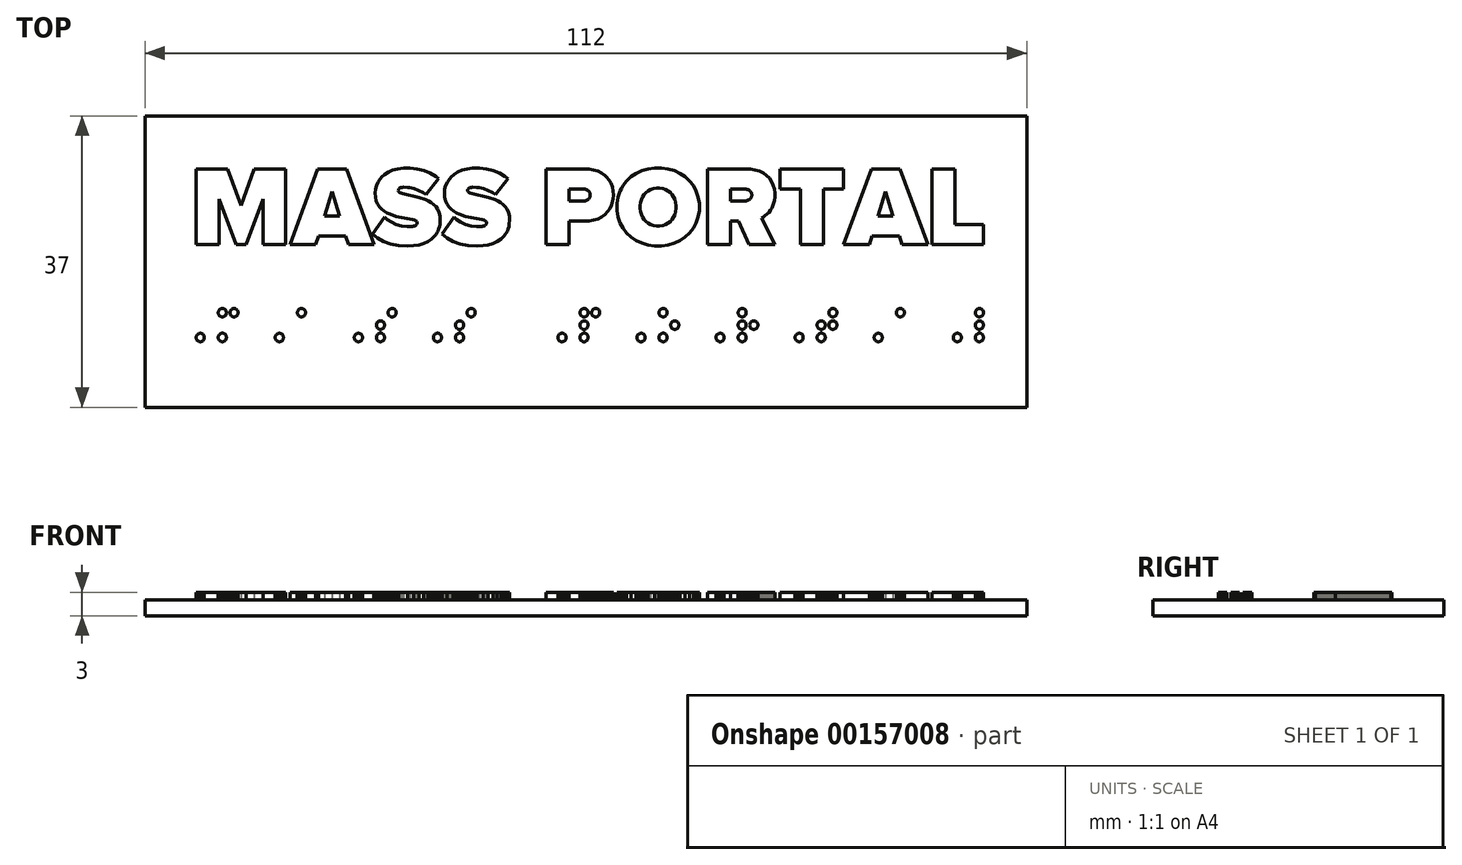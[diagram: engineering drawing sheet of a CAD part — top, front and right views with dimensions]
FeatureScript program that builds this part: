
annotation { "Feature Type Name" : "Feature", "Feature Type Description" : "" }
export const myFeature = defineFeature(function(context is Context, id is Id, definition is map)
    precondition{}
    {
        {
            var Q0;
            Q0=qCreatedBy(makeId("Top.planeOp"),FACE);
            var sketch = newSketch(context, id + "F0", { "sketchPlane" : qUnion([Q0])});
            skLineSegment(sketch, "E0", {"start": v(-10.6, -3.27) * mm, "end": v(-10.74, -3.5) * mm});
            skLineSegment(sketch, "E1", {"start": v(-31.01, -3.66) * mm, "end": v(-30.67, -4.78) * mm});
            skLineSegment(sketch, "E2", {"start": v(-34.46, -3.66) * mm, "end": v(-31.01, -3.66) * mm});
            skLineSegment(sketch, "E3", {"start": v(-45.99, 4.8) * mm, "end": v(-44.3, 0.2) * mm});
            skLineSegment(sketch, "E4", {"start": v(-50, -4.78) * mm, "end": v(-47.1, -4.78) * mm});
            skLineSegment(sketch, "E5", {"start": v(-14.08, 2.45) * mm, "end": v(-14.37, 2.49) * mm});
            skLineSegment(sketch, "E6", {"start": v(-45.99, 4.8) * mm, "end": v(-50, 4.8) * mm});
            skLineSegment(sketch, "E7", {"start": v(-10.74, -3.5) * mm, "end": v(-10.9, -3.7) * mm});
            skLineSegment(sketch, "E8", {"start": v(-17.97, 3.4) * mm, "end": v(-18.1, 3.18) * mm});
            skLineSegment(sketch, "E9", {"start": v(1.93, 4) * mm, "end": v(2.11, 3.84) * mm});
            skLineSegment(sketch, "E10", {"start": v(-47.1, 0.98) * mm, "end": v(-44.95, -4.78) * mm});
            skLineSegment(sketch, "E11", {"start": v(10.46, 1.57) * mm, "end": v(10.66, 1.28) * mm});
            skLineSegment(sketch, "E12", {"start": v(-11.08, -3.9) * mm, "end": v(-11.29, -4.08) * mm});
            skLineSegment(sketch, "E13", {"start": v(-24, 1.76) * mm, "end": v(-23.77, 1.69) * mm});
            skLineSegment(sketch, "E14", {"start": v(-20.87, 0.96) * mm, "end": v(-20.5, 0.79) * mm});
            skLineSegment(sketch, "E15", {"start": v(-20.15, 0.58) * mm, "end": v(-19.83, 0.34) * mm});
            skLineSegment(sketch, "E16", {"start": v(-47.1, 0.98) * mm, "end": v(-47.1, -4.78) * mm});
            skLineSegment(sketch, "E17", {"start": v(-33.69, -1.13) * mm, "end": v(-31.79, -1.13) * mm});
            skLineSegment(sketch, "E18", {"start": v(-20.5, 0.79) * mm, "end": v(-20.15, 0.58) * mm});
            skLineSegment(sketch, "E19", {"start": v(-44.3, 0.2) * mm, "end": v(-42.63, 4.8) * mm});
            skLineSegment(sketch, "E20", {"start": v(19.98, 2.23) * mm, "end": v(20.11, 2.2) * mm});
            skLineSegment(sketch, "E21", {"start": v(-14.37, -2.5) * mm, "end": v(-14.02, -2.5) * mm});
            skLineSegment(sketch, "E22", {"start": v(-26.95, 0.37) * mm, "end": v(-26.72, 0.02) * mm});
            skLineSegment(sketch, "E23", {"start": v(-30.91, 4.8) * mm, "end": v(-34.56, 4.8) * mm});
            skLineSegment(sketch, "E24", {"start": v(-19.83, 0.34) * mm, "end": v(-19.55, 0.05) * mm});
            skLineSegment(sketch, "E25", {"start": v(23.3, 2.79) * mm, "end": v(23.44, 2.3) * mm});
            skLineSegment(sketch, "E26", {"start": v(-32.74, 1.96) * mm, "end": v(-33.69, -1.13) * mm});
            skLineSegment(sketch, "E27", {"start": v(-50, -4.78) * mm, "end": v(-50, 4.8) * mm});
            skLineSegment(sketch, "E28", {"start": v(-32.74, 1.96) * mm, "end": v(-31.79, -1.13) * mm});
            skLineSegment(sketch, "E29", {"start": v(-17.36, -4.36) * mm, "end": v(-16.48, -4.68) * mm});
            skLineSegment(sketch, "E30", {"start": v(-30.91, 4.8) * mm, "end": v(-27.38, -4.78) * mm});
            skLineSegment(sketch, "E31", {"start": v(-38.1, -4.78) * mm, "end": v(-34.56, 4.8) * mm});
            skLineSegment(sketch, "E32", {"start": v(2.11, 3.84) * mm, "end": v(2.43, 3.45) * mm});
            skLineSegment(sketch, "E33", {"start": v(13.77, 1.27) * mm, "end": v(13.9, 0.44) * mm});
            skLineSegment(sketch, "E34", {"start": v(20.23, 2.13) * mm, "end": v(20.34, 2.06) * mm});
            skLineSegment(sketch, "E35", {"start": v(10.81, 0.95) * mm, "end": v(10.91, 0.59) * mm});
            skLineSegment(sketch, "E36", {"start": v(3.58, 1.27) * mm, "end": v(3.45, 0.44) * mm});
            skLineSegment(sketch, "E37", {"start": v(-24.32, 2.18) * mm, "end": v(-24.32, 2.15) * mm});
            skLineSegment(sketch, "E38", {"start": v(-38.1, -4.78) * mm, "end": v(-34.8, -4.78) * mm});
            skLineSegment(sketch, "E39", {"start": v(2.43, 3.45) * mm, "end": v(2.68, 3.02) * mm});
            skLineSegment(sketch, "E40", {"start": v(-27.24, 1.24) * mm, "end": v(-27.12, 0.78) * mm});
            skLineSegment(sketch, "E41", {"start": v(6.89, 1.57) * mm, "end": v(6.69, 1.28) * mm});
            skLineSegment(sketch, "E42", {"start": v(-10.9, -3.7) * mm, "end": v(-11.08, -3.9) * mm});
            skLineSegment(sketch, "E43", {"start": v(-13.7, -2.47) * mm, "end": v(-14.02, -2.5) * mm});
            skLineSegment(sketch, "E44", {"start": v(-24.3, 2.22) * mm, "end": v(-24.32, 2.18) * mm});
            skLineSegment(sketch, "E45", {"start": v(-18.3, 2.73) * mm, "end": v(-18.42, 2.26) * mm});
            skLineSegment(sketch, "E46", {"start": v(20.11, 2.2) * mm, "end": v(20.23, 2.13) * mm});
            skLineSegment(sketch, "E47", {"start": v(-14.37, 2.49) * mm, "end": v(-14.87, 2.5) * mm});
            skLineSegment(sketch, "E48", {"start": v(-0.75, 2.28) * mm, "end": v(-0.61, 2.26) * mm});
            skLineSegment(sketch, "E49", {"start": v(-19.14, -0.67) * mm, "end": v(-19.03, -1.11) * mm});
            skLineSegment(sketch, "E50", {"start": v(-19.03, -1.11) * mm, "end": v(-19, -1.62) * mm});
            skLineSegment(sketch, "E51", {"start": v(-0.25, 2.13) * mm, "end": v(-0.2, 2.1) * mm});
            skLineSegment(sketch, "E52", {"start": v(20.55, 1.74) * mm, "end": v(20.56, 1.68) * mm});
            skLineSegment(sketch, "E53", {"start": v(23.44, 2.3) * mm, "end": v(23.51, 1.78) * mm});
            skLineSegment(sketch, "E54", {"start": v(14.96, -4.78) * mm, "end": v(17.86, -4.78) * mm});
            skLineSegment(sketch, "E55", {"start": v(-25.77, -0.74) * mm, "end": v(-25.4, -0.92) * mm});
            skLineSegment(sketch, "E56", {"start": v(20.56, 1.68) * mm, "end": v(20.57, 1.6) * mm});
            skLineSegment(sketch, "E57", {"start": v(-13.57, -2.43) * mm, "end": v(-13.7, -2.47) * mm});
            skLineSegment(sketch, "E58", {"start": v(-0.16, 2.05) * mm, "end": v(-0.12, 2) * mm});
            skLineSegment(sketch, "E59", {"start": v(-15.1, -2.41) * mm, "end": v(-14.37, -2.5) * mm});
            skLineSegment(sketch, "E60", {"start": v(-26.12, -0.53) * mm, "end": v(-25.77, -0.74) * mm});
            skLineSegment(sketch, "E61", {"start": v(-0.12, 4.8) * mm, "end": v(0.49, 4.71) * mm});
            skLineSegment(sketch, "E62", {"start": v(20.58, 1.53) * mm, "end": v(20.57, 1.45) * mm});
            skLineSegment(sketch, "E63", {"start": v(-15.33, 2.4) * mm, "end": v(-15.37, 2.38) * mm});
            skLineSegment(sketch, "E64", {"start": v(-0.48, 2.23) * mm, "end": v(-0.36, 2.19) * mm});
            skLineSegment(sketch, "E65", {"start": v(-19.55, 0.05) * mm, "end": v(-19.32, -0.29) * mm});
            skLineSegment(sketch, "E66", {"start": v(-15.25, 2.45) * mm, "end": v(-15.33, 2.4) * mm});
            skLineSegment(sketch, "E67", {"start": v(-0.61, 2.26) * mm, "end": v(-0.48, 2.23) * mm});
            skLineSegment(sketch, "E68", {"start": v(0.49, 4.71) * mm, "end": v(1.03, 4.55) * mm});
            skLineSegment(sketch, "E69", {"start": v(-26.72, 0.02) * mm, "end": v(-26.44, -0.28) * mm});
            skLineSegment(sketch, "E70", {"start": v(23.51, 1.78) * mm, "end": v(23.52, 1.27) * mm});
            skLineSegment(sketch, "E71", {"start": v(-24.32, 2.15) * mm, "end": v(-24.33, 2.08) * mm});
            skLineSegment(sketch, "E72", {"start": v(-0.2, 2.1) * mm, "end": v(-0.16, 2.05) * mm});
            skLineSegment(sketch, "E73", {"start": v(-27.38, -4.78) * mm, "end": v(-30.67, -4.78) * mm});
            skLineSegment(sketch, "E74", {"start": v(-27.27, 1.78) * mm, "end": v(-27.24, 1.24) * mm});
            skLineSegment(sketch, "E75", {"start": v(-24.29, 1.95) * mm, "end": v(-24.18, 1.85) * mm});
            skLineSegment(sketch, "E76", {"start": v(-15.45, 2.3) * mm, "end": v(-15.47, 2.28) * mm});
            skLineSegment(sketch, "E77", {"start": v(20.57, 1.6) * mm, "end": v(20.58, 1.53) * mm});
            skLineSegment(sketch, "E78", {"start": v(-10.75, 3.87) * mm, "end": v(-10.41, 3.62) * mm});
            skLineSegment(sketch, "E79", {"start": v(-15.42, 2.33) * mm, "end": v(-15.45, 2.3) * mm});
            skLineSegment(sketch, "E80", {"start": v(1.51, 4.31) * mm, "end": v(1.93, 4) * mm});
            skLineSegment(sketch, "E81", {"start": v(20.55, 1.31) * mm, "end": v(20.52, 1.25) * mm});
            skLineSegment(sketch, "E82", {"start": v(-24.33, 2.08) * mm, "end": v(-24.29, 1.95) * mm});
            skLineSegment(sketch, "E83", {"start": v(21.01, 4.71) * mm, "end": v(21.56, 4.55) * mm});
            skLineSegment(sketch, "E84", {"start": v(-21.1, -4.63) * mm, "end": v(-21.72, -4.8) * mm});
            skLineSegment(sketch, "E85", {"start": v(-24.18, 1.85) * mm, "end": v(-24, 1.76) * mm});
            skLineSegment(sketch, "E86", {"start": v(-15.37, 2.38) * mm, "end": v(-15.4, 2.36) * mm});
            skLineSegment(sketch, "E87", {"start": v(-11.29, -4.08) * mm, "end": v(-11.76, -4.39) * mm});
            skLineSegment(sketch, "E88", {"start": v(-19.32, -0.29) * mm, "end": v(-19.14, -0.67) * mm});
            skLineSegment(sketch, "E89", {"start": v(20.56, 1.38) * mm, "end": v(20.55, 1.31) * mm});
            skLineSegment(sketch, "E90", {"start": v(20.57, 1.45) * mm, "end": v(20.56, 1.38) * mm});
            skLineSegment(sketch, "E91", {"start": v(6.69, 1.28) * mm, "end": v(6.54, 0.95) * mm});
            skLineSegment(sketch, "E92", {"start": v(-18.1, 3.18) * mm, "end": v(-18.3, 2.73) * mm});
            skLineSegment(sketch, "E93", {"start": v(-15.4, 2.36) * mm, "end": v(-15.42, 2.33) * mm});
            skLineSegment(sketch, "E94", {"start": v(-0.36, 2.19) * mm, "end": v(-0.25, 2.13) * mm});
            skLineSegment(sketch, "E95", {"start": v(10.66, 1.28) * mm, "end": v(10.81, 0.95) * mm});
            skLineSegment(sketch, "E96", {"start": v(-18.12, -3.94) * mm, "end": v(-17.36, -4.36) * mm});
            skLineSegment(sketch, "E97", {"start": v(7.73, 2.22) * mm, "end": v(7.4, 2.05) * mm});
            skLineSegment(sketch, "E98", {"start": v(-26.44, -0.28) * mm, "end": v(-26.12, -0.53) * mm});
            skLineSegment(sketch, "E99", {"start": v(-13.5, 2.32) * mm, "end": v(-14.08, 2.45) * mm});
            skLineSegment(sketch, "E100", {"start": v(1.03, 4.55) * mm, "end": v(1.51, 4.31) * mm});
            skLineSegment(sketch, "E101", {"start": v(19.7, 2.28) * mm, "end": v(19.84, 2.26) * mm});
            skLineSegment(sketch, "E102", {"start": v(9.62, 2.22) * mm, "end": v(9.94, 2.05) * mm});
            skLineSegment(sketch, "E103", {"start": v(-25.3, -4.68) * mm, "end": v(-24.28, -4.88) * mm});
            skLineSegment(sketch, "E104", {"start": v(20.4, 4.8) * mm, "end": v(21.01, 4.71) * mm});
            skLineSegment(sketch, "E105", {"start": v(-13.2, -2.23) * mm, "end": v(-13.24, -2.27) * mm});
            skLineSegment(sketch, "E106", {"start": v(-15.78, -2.21) * mm, "end": v(-15.1, -2.41) * mm});
            skLineSegment(sketch, "E107", {"start": v(2.96, 1) * mm, "end": v(2.92, 0.74) * mm});
            skLineSegment(sketch, "E108", {"start": v(3.45, -0.43) * mm, "end": v(3.58, -1.25) * mm});
            skLineSegment(sketch, "E109", {"start": v(6.38, -0.2) * mm, "end": v(6.43, -0.57) * mm});
            skLineSegment(sketch, "E110", {"start": v(-13.15, -2.14) * mm, "end": v(-13.17, -2.19) * mm});
            skLineSegment(sketch, "E111", {"start": v(20.34, 0.99) * mm, "end": v(20.23, 0.92) * mm});
            skLineSegment(sketch, "E112", {"start": v(-17.25, 4.14) * mm, "end": v(-17.65, 3.79) * mm});
            skLineSegment(sketch, "E113", {"start": v(-16.77, 4.45) * mm, "end": v(-17.25, 4.14) * mm});
            skLineSegment(sketch, "E114", {"start": v(11.47, -4.26) * mm, "end": v(10.74, -4.6) * mm});
            skLineSegment(sketch, "E115", {"start": v(-13.13, -2.1) * mm, "end": v(-13.15, -2.14) * mm});
            skLineSegment(sketch, "E116", {"start": v(-5.57, -4.78) * mm, "end": v(-2.67, -4.78) * mm});
            skLineSegment(sketch, "E117", {"start": v(-22.48, -1.6) * mm, "end": v(-22.25, -1.68) * mm});
            skLineSegment(sketch, "E118", {"start": v(-15.47, -4.88) * mm, "end": v(-14.32, -4.95) * mm});
            skLineSegment(sketch, "E119", {"start": v(20.38, 1.03) * mm, "end": v(20.34, 0.99) * mm});
            skLineSegment(sketch, "E120", {"start": v(20.43, 1.08) * mm, "end": v(20.38, 1.03) * mm});
            skLineSegment(sketch, "E121", {"start": v(-23.83, 2.5) * mm, "end": v(-23.95, 2.48) * mm});
            skLineSegment(sketch, "E122", {"start": v(20.23, 0.92) * mm, "end": v(20.11, 0.86) * mm});
            skLineSegment(sketch, "E123", {"start": v(13.9, -0.43) * mm, "end": v(13.77, -1.25) * mm});
            skLineSegment(sketch, "E124", {"start": v(10.97, -0.2) * mm, "end": v(10.91, -0.57) * mm});
            skLineSegment(sketch, "E125", {"start": v(-0.12, 1.04) * mm, "end": v(-0.16, 1) * mm});
            skLineSegment(sketch, "E126", {"start": v(20.52, 1.25) * mm, "end": v(20.5, 1.19) * mm});
            skLineSegment(sketch, "E127", {"start": v(-23.95, 2.48) * mm, "end": v(-24.06, 2.45) * mm});
            skLineSegment(sketch, "E128", {"start": v(12.12, -3.83) * mm, "end": v(11.47, -4.26) * mm});
            skLineSegment(sketch, "E129", {"start": v(-12.9, -4.8) * mm, "end": v(-13.58, -4.92) * mm});
            skLineSegment(sketch, "E130", {"start": v(-13.33, -2.33) * mm, "end": v(-13.44, -2.39) * mm});
            skLineSegment(sketch, "E131", {"start": v(-24.06, 2.45) * mm, "end": v(-24.14, 2.4) * mm});
            skLineSegment(sketch, "E132", {"start": v(-19.1, -2.5) * mm, "end": v(-19.18, -2.77) * mm});
            skLineSegment(sketch, "E133", {"start": v(-27.23, 2.26) * mm, "end": v(-27.27, 1.78) * mm});
            skLineSegment(sketch, "E134", {"start": v(-13.17, -2.19) * mm, "end": v(-13.2, -2.23) * mm});
            skLineSegment(sketch, "E135", {"start": v(-25.4, -0.92) * mm, "end": v(-24.6, -1.18) * mm});
            skLineSegment(sketch, "E136", {"start": v(20.46, 1.13) * mm, "end": v(20.43, 1.08) * mm});
            skLineSegment(sketch, "E137", {"start": v(21.56, 4.55) * mm, "end": v(22.04, 4.31) * mm});
            skLineSegment(sketch, "E138", {"start": v(-0.16, 1) * mm, "end": v(-0.25, 0.92) * mm});
            skLineSegment(sketch, "E139", {"start": v(19.98, 0.81) * mm, "end": v(19.84, 0.79) * mm});
            skLineSegment(sketch, "E140", {"start": v(20.11, 0.86) * mm, "end": v(19.98, 0.81) * mm});
            skLineSegment(sketch, "E141", {"start": v(-13.44, -2.39) * mm, "end": v(-13.57, -2.43) * mm});
            skLineSegment(sketch, "E142", {"start": v(-11.48, 4.3) * mm, "end": v(-10.75, 3.87) * mm});
            skLineSegment(sketch, "E143", {"start": v(23.52, 1.27) * mm, "end": v(23.46, 0.82) * mm});
            skLineSegment(sketch, "E144", {"start": v(5.23, -3.83) * mm, "end": v(5.88, -4.26) * mm});
            skLineSegment(sketch, "E145", {"start": v(-15.14, 2.48) * mm, "end": v(-15.25, 2.45) * mm});
            skLineSegment(sketch, "E146", {"start": v(20.5, 1.19) * mm, "end": v(20.46, 1.13) * mm});
            skLineSegment(sketch, "E147", {"start": v(10.91, -0.57) * mm, "end": v(10.81, -0.93) * mm});
            skLineSegment(sketch, "E148", {"start": v(-24.3, 2.25) * mm, "end": v(-24.3, 2.22) * mm});
            skLineSegment(sketch, "E149", {"start": v(-24.28, 2.28) * mm, "end": v(-24.3, 2.25) * mm});
            skLineSegment(sketch, "E150", {"start": v(-21.72, -4.8) * mm, "end": v(-22.4, -4.92) * mm});
            skLineSegment(sketch, "E151", {"start": v(-24.26, 2.3) * mm, "end": v(-24.28, 2.28) * mm});
            skLineSegment(sketch, "E152", {"start": v(-0.48, 0.82) * mm, "end": v(-0.61, 0.79) * mm});
            skLineSegment(sketch, "E153", {"start": v(13.15, -2.7) * mm, "end": v(12.68, -3.3) * mm});
            skLineSegment(sketch, "E154", {"start": v(7.4, 2.05) * mm, "end": v(7.13, 1.83) * mm});
            skLineSegment(sketch, "E155", {"start": v(-18.14, 0.37) * mm, "end": v(-17.9, 0.02) * mm});
            skLineSegment(sketch, "E156", {"start": v(-0.36, 0.86) * mm, "end": v(-0.48, 0.82) * mm});
            skLineSegment(sketch, "E157", {"start": v(22.04, 4.31) * mm, "end": v(22.46, 4) * mm});
            skLineSegment(sketch, "E158", {"start": v(-12.3, -4.63) * mm, "end": v(-12.9, -4.8) * mm});
            skLineSegment(sketch, "E159", {"start": v(-11.02, 0.34) * mm, "end": v(-10.74, 0.05) * mm});
            skLineSegment(sketch, "E160", {"start": v(9.94, 2.05) * mm, "end": v(10.22, 1.83) * mm});
            skLineSegment(sketch, "E161", {"start": v(-15.02, 2.5) * mm, "end": v(-15.14, 2.48) * mm});
            skLineSegment(sketch, "E162", {"start": v(-17.9, 0.02) * mm, "end": v(-17.63, -0.28) * mm});
            skLineSegment(sketch, "E163", {"start": v(-11.76, -4.39) * mm, "end": v(-12.3, -4.63) * mm});
            skLineSegment(sketch, "E164", {"start": v(6.6, 4.6) * mm, "end": v(5.88, 4.27) * mm});
            skLineSegment(sketch, "E165", {"start": v(-24.18, 2.38) * mm, "end": v(-24.2, 2.36) * mm});
            skLineSegment(sketch, "E166", {"start": v(-24.14, 2.4) * mm, "end": v(-24.18, 2.38) * mm});
            skLineSegment(sketch, "E167", {"start": v(-0.25, 0.92) * mm, "end": v(-0.36, 0.86) * mm});
            skLineSegment(sketch, "E168", {"start": v(-0.61, 0.79) * mm, "end": v(-0.75, 0.77) * mm});
            skLineSegment(sketch, "E169", {"start": v(22.46, 4) * mm, "end": v(22.8, 3.65) * mm});
            skLineSegment(sketch, "E170", {"start": v(23.46, 0.82) * mm, "end": v(23.36, 0.42) * mm});
            skLineSegment(sketch, "E171", {"start": v(-24.6, -1.18) * mm, "end": v(-22.48, -1.6) * mm});
            skLineSegment(sketch, "E172", {"start": v(-17.3, -0.53) * mm, "end": v(-16.96, -0.74) * mm});
            skLineSegment(sketch, "E173", {"start": v(-17.63, -0.28) * mm, "end": v(-17.3, -0.53) * mm});
            skLineSegment(sketch, "E174", {"start": v(-22.52, -2.47) * mm, "end": v(-22.83, -2.5) * mm});
            skLineSegment(sketch, "E175", {"start": v(-16.21, 4.68) * mm, "end": v(-16.77, 4.45) * mm});
            skLineSegment(sketch, "E176", {"start": v(-10.74, 0.05) * mm, "end": v(-10.5, -0.29) * mm});
            skLineSegment(sketch, "E177", {"start": v(4.67, -3.3) * mm, "end": v(5.23, -3.83) * mm});
            skLineSegment(sketch, "E178", {"start": v(6.54, -0.93) * mm, "end": v(6.69, -1.26) * mm});
            skLineSegment(sketch, "E179", {"start": v(6.43, -0.57) * mm, "end": v(6.54, -0.93) * mm});
            skLineSegment(sketch, "E180", {"start": v(-13.29, -2.3) * mm, "end": v(-13.33, -2.33) * mm});
            skLineSegment(sketch, "E181", {"start": v(-13.24, -2.27) * mm, "end": v(-13.29, -2.3) * mm});
            skLineSegment(sketch, "E182", {"start": v(7.13, 1.83) * mm, "end": v(6.89, 1.57) * mm});
            skLineSegment(sketch, "E183", {"start": v(-27.6, -3.43) * mm, "end": v(-26.08, -1.27) * mm});
            skLineSegment(sketch, "E184", {"start": v(-24.2, 2.36) * mm, "end": v(-24.24, 2.33) * mm});
            skLineSegment(sketch, "E185", {"start": v(-14.87, 2.5) * mm, "end": v(-15.02, 2.5) * mm});
            skLineSegment(sketch, "E186", {"start": v(-12.27, 4.62) * mm, "end": v(-11.48, 4.3) * mm});
            skLineSegment(sketch, "E187", {"start": v(12.68, -3.3) * mm, "end": v(12.12, -3.83) * mm});
            skLineSegment(sketch, "E188", {"start": v(23.09, 3.24) * mm, "end": v(23.3, 2.79) * mm});
            skLineSegment(sketch, "E189", {"start": v(-16.48, -4.68) * mm, "end": v(-15.47, -4.88) * mm});
            skLineSegment(sketch, "E190", {"start": v(-22.4, -4.92) * mm, "end": v(-23.13, -4.95) * mm});
            skLineSegment(sketch, "E191", {"start": v(-26.08, -1.27) * mm, "end": v(-25.73, -1.57) * mm});
            skLineSegment(sketch, "E192", {"start": v(4.2, -2.7) * mm, "end": v(4.67, -3.3) * mm});
            skLineSegment(sketch, "E193", {"start": v(22.8, 3.65) * mm, "end": v(23.09, 3.24) * mm});
            skLineSegment(sketch, "E194", {"start": v(10.74, 4.6) * mm, "end": v(11.47, 4.27) * mm});
            skLineSegment(sketch, "E195", {"start": v(-24.28, -4.88) * mm, "end": v(-23.13, -4.95) * mm});
            skLineSegment(sketch, "E196", {"start": v(-10.5, -0.29) * mm, "end": v(-10.33, -0.67) * mm});
            skLineSegment(sketch, "E197", {"start": v(10.81, -0.93) * mm, "end": v(10.66, -1.26) * mm});
            skLineSegment(sketch, "E198", {"start": v(10.22, 1.83) * mm, "end": v(10.46, 1.57) * mm});
            skLineSegment(sketch, "E199", {"start": v(7.4, 4.83) * mm, "end": v(6.6, 4.6) * mm});
            skLineSegment(sketch, "E200", {"start": v(-24.24, 2.33) * mm, "end": v(-24.26, 2.3) * mm});
            skLineSegment(sketch, "E201", {"start": v(-19.56, 3.87) * mm, "end": v(-19.23, 3.62) * mm});
            skLineSegment(sketch, "E202", {"start": v(23.54, -4.78) * mm, "end": v(20.23, -4.78) * mm});
            skLineSegment(sketch, "E203", {"start": v(-22.14, -2.33) * mm, "end": v(-22.25, -2.39) * mm});
            skLineSegment(sketch, "E204", {"start": v(1.51, -1.26) * mm, "end": v(1.03, -1.5) * mm});
            skLineSegment(sketch, "E205", {"start": v(-22.25, -2.39) * mm, "end": v(-22.38, -2.43) * mm});
            skLineSegment(sketch, "E206", {"start": v(1.93, -0.96) * mm, "end": v(1.51, -1.26) * mm});
            skLineSegment(sketch, "E207", {"start": v(18.9, -1.76) * mm, "end": v(20.23, -4.78) * mm});
            skLineSegment(sketch, "E208", {"start": v(-10.33, -0.67) * mm, "end": v(-10.22, -1.11) * mm});
            skLineSegment(sketch, "E209", {"start": v(-22.38, -2.43) * mm, "end": v(-22.52, -2.47) * mm});
            skLineSegment(sketch, "E210", {"start": v(2.28, -0.6) * mm, "end": v(1.93, -0.96) * mm});
            skLineSegment(sketch, "E211", {"start": v(1.03, -1.5) * mm, "end": v(0.49, -1.66) * mm});
            skLineSegment(sketch, "E212", {"start": v(21.8, -1.39) * mm, "end": v(23.54, -4.78) * mm});
            skLineSegment(sketch, "E213", {"start": v(2.92, 0.74) * mm, "end": v(2.77, 0.25) * mm});
            skLineSegment(sketch, "E214", {"start": v(-19.23, 3.62) * mm, "end": v(-20.78, 1.56) * mm});
            skLineSegment(sketch, "E215", {"start": v(-26.06, 4.14) * mm, "end": v(-26.46, 3.79) * mm});
            skLineSegment(sketch, "E216", {"start": v(9.11, 4.95) * mm, "end": v(8.24, 4.95) * mm});
            skLineSegment(sketch, "E217", {"start": v(-23.92, -2.41) * mm, "end": v(-23.18, -2.5) * mm});
            skLineSegment(sketch, "E218", {"start": v(9.96, 4.83) * mm, "end": v(10.74, 4.6) * mm});
            skLineSegment(sketch, "E219", {"start": v(-15.79, -1.18) * mm, "end": v(-13.67, -1.6) * mm});
            skLineSegment(sketch, "E220", {"start": v(46.36, 4.8) * mm, "end": v(43.46, 4.8) * mm});
            skLineSegment(sketch, "E221", {"start": v(-22.02, -2.23) * mm, "end": v(-22.05, -2.27) * mm});
            skLineSegment(sketch, "E222", {"start": v(8.24, 4.95) * mm, "end": v(7.4, 4.83) * mm});
            skLineSegment(sketch, "E223", {"start": v(-16.96, -0.74) * mm, "end": v(-16.58, -0.92) * mm});
            skLineSegment(sketch, "E224", {"start": v(46.36, 4.8) * mm, "end": v(46.36, -2.25) * mm});
            skLineSegment(sketch, "E225", {"start": v(-20.29, 4.3) * mm, "end": v(-19.56, 3.87) * mm});
            skLineSegment(sketch, "E226", {"start": v(-21.99, -2.19) * mm, "end": v(-22.02, -2.23) * mm});
            skLineSegment(sketch, "E227", {"start": v(9.94, -2.04) * mm, "end": v(9.62, -2.2) * mm});
            skLineSegment(sketch, "E228", {"start": v(43.46, -4.78) * mm, "end": v(43.46, 4.8) * mm});
            skLineSegment(sketch, "E229", {"start": v(-10.29, -2.5) * mm, "end": v(-10.37, -2.77) * mm});
            skLineSegment(sketch, "E230", {"start": v(-10.22, -1.11) * mm, "end": v(-10.18, -1.62) * mm});
            skLineSegment(sketch, "E231", {"start": v(7.4, -2.04) * mm, "end": v(7.73, -2.2) * mm});
            skLineSegment(sketch, "E232", {"start": v(22.27, -1.1) * mm, "end": v(22.03, -1.26) * mm});
            skLineSegment(sketch, "E233", {"start": v(-16.58, -0.92) * mm, "end": v(-15.79, -1.18) * mm});
            skLineSegment(sketch, "E234", {"start": v(-22.3, 2.32) * mm, "end": v(-21.72, 2.1) * mm});
            skLineSegment(sketch, "E235", {"start": v(-11.34, 0.58) * mm, "end": v(-11.02, 0.34) * mm});
            skLineSegment(sketch, "E236", {"start": v(-14.87, 4.94) * mm, "end": v(-14.02, 4.94) * mm});
            skLineSegment(sketch, "E237", {"start": v(8.47, -2.39) * mm, "end": v(8.88, -2.39) * mm});
            skLineSegment(sketch, "E238", {"start": v(46.36, -2.25) * mm, "end": v(50, -2.25) * mm});
            skLineSegment(sketch, "E239", {"start": v(-17.27, -1.27) * mm, "end": v(-16.92, -1.57) * mm});
            skLineSegment(sketch, "E240", {"start": v(9.11, 4.95) * mm, "end": v(9.96, 4.83) * mm});
            skLineSegment(sketch, "E241", {"start": v(-10.23, -2.22) * mm, "end": v(-10.29, -2.5) * mm});
            skLineSegment(sketch, "E242", {"start": v(43.46, -4.78) * mm, "end": v(50, -4.78) * mm});
            skLineSegment(sketch, "E243", {"start": v(22.03, -1.26) * mm, "end": v(21.8, -1.39) * mm});
            skLineSegment(sketch, "E244", {"start": v(17.86, 2.28) * mm, "end": v(19.7, 2.28) * mm});
            skLineSegment(sketch, "E245", {"start": v(-12.06, 0.96) * mm, "end": v(-11.69, 0.79) * mm});
            skLineSegment(sketch, "E246", {"start": v(10.66, -1.26) * mm, "end": v(10.46, -1.56) * mm});
            skLineSegment(sketch, "E247", {"start": v(-25.02, 4.68) * mm, "end": v(-25.58, 4.45) * mm});
            skLineSegment(sketch, "E248", {"start": v(-14.87, 4.94) * mm, "end": v(-15.58, 4.85) * mm});
            skLineSegment(sketch, "E249", {"start": v(-11.69, 0.79) * mm, "end": v(-11.34, 0.58) * mm});
            skLineSegment(sketch, "E250", {"start": v(37.58, 1.96) * mm, "end": v(38.53, -1.13) * mm});
            skLineSegment(sketch, "E251", {"start": v(32.22, -4.78) * mm, "end": v(35.76, 4.8) * mm});
            skLineSegment(sketch, "E252", {"start": v(-19.18, -2.77) * mm, "end": v(-19.28, -3.03) * mm});
            skLineSegment(sketch, "E253", {"start": v(-15.58, 4.85) * mm, "end": v(-16.21, 4.68) * mm});
            skLineSegment(sketch, "E254", {"start": v(10.46, -1.56) * mm, "end": v(10.22, -1.82) * mm});
            skLineSegment(sketch, "E255", {"start": v(11.47, 4.27) * mm, "end": v(12.12, 3.84) * mm});
            skLineSegment(sketch, "E256", {"start": v(37.58, 1.96) * mm, "end": v(36.63, -1.13) * mm});
            skLineSegment(sketch, "E257", {"start": v(-23.18, -2.5) * mm, "end": v(-22.83, -2.5) * mm});
            skLineSegment(sketch, "E258", {"start": v(6.89, -1.56) * mm, "end": v(7.13, -1.82) * mm});
            skLineSegment(sketch, "E259", {"start": v(-13.12, 4.83) * mm, "end": v(-12.27, 4.62) * mm});
            skLineSegment(sketch, "E260", {"start": v(-26.46, 3.79) * mm, "end": v(-26.78, 3.4) * mm});
            skLineSegment(sketch, "E261", {"start": v(-10.18, -1.62) * mm, "end": v(-10.23, -2.22) * mm});
            skLineSegment(sketch, "E262", {"start": v(-19.55, -3.5) * mm, "end": v(-19.71, -3.7) * mm});
            skLineSegment(sketch, "E263", {"start": v(42.94, -4.78) * mm, "end": v(39.65, -4.78) * mm});
            skLineSegment(sketch, "E264", {"start": v(39.4, 4.8) * mm, "end": v(35.76, 4.8) * mm});
            skLineSegment(sketch, "E265", {"start": v(23.3, 0.23) * mm, "end": v(23.14, -0.11) * mm});
            skLineSegment(sketch, "E266", {"start": v(50, -2.25) * mm, "end": v(50, -4.78) * mm});
            skLineSegment(sketch, "E267", {"start": v(-14.02, 4.94) * mm, "end": v(-13.12, 4.83) * mm});
            skLineSegment(sketch, "E268", {"start": v(17.86, 2.28) * mm, "end": v(17.86, 0.77) * mm});
            skLineSegment(sketch, "E269", {"start": v(-21.17, 1.82) * mm, "end": v(-20.78, 1.56) * mm});
            skLineSegment(sketch, "E270", {"start": v(-13.12, -2) * mm, "end": v(-13.12, -2.04) * mm});
            skLineSegment(sketch, "E271", {"start": v(36.63, -1.13) * mm, "end": v(38.53, -1.13) * mm});
            skLineSegment(sketch, "E272", {"start": v(5.88, 4.27) * mm, "end": v(5.23, 3.84) * mm});
            skLineSegment(sketch, "E273", {"start": v(-18.31, 0.78) * mm, "end": v(-18.14, 0.37) * mm});
            skLineSegment(sketch, "E274", {"start": v(23.36, 0.42) * mm, "end": v(23.3, 0.23) * mm});
            skLineSegment(sketch, "E275", {"start": v(-2.67, 2.28) * mm, "end": v(-2.67, 0.77) * mm});
            skLineSegment(sketch, "E276", {"start": v(-0.08, 1.08) * mm, "end": v(-0.12, 1.04) * mm});
            skLineSegment(sketch, "E277", {"start": v(9.62, -2.2) * mm, "end": v(9.27, -2.32) * mm});
            skLineSegment(sketch, "E278", {"start": v(13.77, -1.25) * mm, "end": v(13.52, -2.01) * mm});
            skLineSegment(sketch, "E279", {"start": v(7.73, -2.2) * mm, "end": v(8.08, -2.32) * mm});
            skLineSegment(sketch, "E280", {"start": v(12.12, 3.84) * mm, "end": v(12.68, 3.32) * mm});
            skLineSegment(sketch, "E281", {"start": v(-22.05, -2.27) * mm, "end": v(-22.1, -2.3) * mm});
            skLineSegment(sketch, "E282", {"start": v(2.77, 0.25) * mm, "end": v(2.56, -0.2) * mm});
            skLineSegment(sketch, "E283", {"start": v(9.27, -2.32) * mm, "end": v(8.88, -2.39) * mm});
            skLineSegment(sketch, "E284", {"start": v(-2.67, -1.76) * mm, "end": v(-2.67, -4.78) * mm});
            skLineSegment(sketch, "E285", {"start": v(-0.05, 1.13) * mm, "end": v(-0.08, 1.08) * mm});
            skLineSegment(sketch, "E286", {"start": v(-25.58, 4.45) * mm, "end": v(-26.06, 4.14) * mm});
            skLineSegment(sketch, "E287", {"start": v(-21.08, 4.62) * mm, "end": v(-20.29, 4.3) * mm});
            skLineSegment(sketch, "E288", {"start": v(-22.25, -1.68) * mm, "end": v(-22.08, -1.76) * mm});
            skLineSegment(sketch, "E289", {"start": v(19.84, 0.79) * mm, "end": v(19.7, 0.77) * mm});
            skLineSegment(sketch, "E290", {"start": v(-18.78, -3.43) * mm, "end": v(-17.27, -1.27) * mm});
            skLineSegment(sketch, "E291", {"start": v(32.22, -4.78) * mm, "end": v(35.51, -4.78) * mm});
            skLineSegment(sketch, "E292", {"start": v(-22.1, -2.3) * mm, "end": v(-22.14, -2.33) * mm});
            skLineSegment(sketch, "E293", {"start": v(39.4, 4.8) * mm, "end": v(42.94, -4.78) * mm});
            skLineSegment(sketch, "E294", {"start": v(5.23, 3.84) * mm, "end": v(4.67, 3.32) * mm});
            skLineSegment(sketch, "E295", {"start": v(-19.4, -3.27) * mm, "end": v(-19.55, -3.5) * mm});
            skLineSegment(sketch, "E296", {"start": v(-24.6, -2.21) * mm, "end": v(-23.92, -2.41) * mm});
            skLineSegment(sketch, "E297", {"start": v(-12.85, 1.23) * mm, "end": v(-12.06, 0.96) * mm});
            skLineSegment(sketch, "E298", {"start": v(3.58, -1.25) * mm, "end": v(3.83, -2.01) * mm});
            skLineSegment(sketch, "E299", {"start": v(-0.02, 1.19) * mm, "end": v(-0.05, 1.13) * mm});
            skLineSegment(sketch, "E300", {"start": v(6.69, -1.26) * mm, "end": v(6.89, -1.56) * mm});
            skLineSegment(sketch, "E301", {"start": v(-13.12, -2.04) * mm, "end": v(-13.13, -2.1) * mm});
            skLineSegment(sketch, "E302", {"start": v(-21.72, 2.1) * mm, "end": v(-21.17, 1.82) * mm});
            skLineSegment(sketch, "E303", {"start": v(2.56, -0.2) * mm, "end": v(2.28, -0.6) * mm});
            skLineSegment(sketch, "E304", {"start": v(-19, -1.62) * mm, "end": v(-19.04, -2.22) * mm});
            skLineSegment(sketch, "E305", {"start": v(8.08, -2.32) * mm, "end": v(8.47, -2.39) * mm});
            skLineSegment(sketch, "E306", {"start": v(-18.46, 1.78) * mm, "end": v(-18.42, 1.24) * mm});
            skLineSegment(sketch, "E307", {"start": v(-19.28, -3.03) * mm, "end": v(-19.4, -3.27) * mm});
            skLineSegment(sketch, "E308", {"start": v(-15.48, 1.95) * mm, "end": v(-15.37, 1.85) * mm});
            skLineSegment(sketch, "E309", {"start": v(-15.52, 2.08) * mm, "end": v(-15.48, 1.95) * mm});
            skLineSegment(sketch, "E310", {"start": v(-18.42, 1.24) * mm, "end": v(-18.31, 0.78) * mm});
            skLineSegment(sketch, "E311", {"start": v(5.88, -4.26) * mm, "end": v(6.6, -4.6) * mm});
            skLineSegment(sketch, "E312", {"start": v(-13.58, -4.92) * mm, "end": v(-14.32, -4.95) * mm});
            skLineSegment(sketch, "E313", {"start": v(26.76, -4.78) * mm, "end": v(29.66, -4.78) * mm});
            skLineSegment(sketch, "E314", {"start": v(8.47, 2.4) * mm, "end": v(8.88, 2.4) * mm});
            skLineSegment(sketch, "E315", {"start": v(-23.68, 2.5) * mm, "end": v(-23.83, 2.5) * mm});
            skLineSegment(sketch, "E316", {"start": v(-15.5, 2.18) * mm, "end": v(-15.51, 2.15) * mm});
            skLineSegment(sketch, "E317", {"start": v(0, 1.25) * mm, "end": v(-0.02, 1.19) * mm});
            skLineSegment(sketch, "E318", {"start": v(4.2, 2.71) * mm, "end": v(4, 2.38) * mm});
            skLineSegment(sketch, "E319", {"start": v(17.86, -1.76) * mm, "end": v(18.9, -1.76) * mm});
            skLineSegment(sketch, "E320", {"start": v(-23.18, 2.49) * mm, "end": v(-23.68, 2.5) * mm});
            skLineSegment(sketch, "E321", {"start": v(10.74, -4.6) * mm, "end": v(9.96, -4.82) * mm});
            skLineSegment(sketch, "E322", {"start": v(0.05, 1.6) * mm, "end": v(0.05, 1.44) * mm});
            skLineSegment(sketch, "E323", {"start": v(29.66, 2.28) * mm, "end": v(29.66, -4.78) * mm});
            skLineSegment(sketch, "E324", {"start": v(17.86, -1.76) * mm, "end": v(17.86, -4.78) * mm});
            skLineSegment(sketch, "E325", {"start": v(-15.2, 1.76) * mm, "end": v(-14.96, 1.69) * mm});
            skLineSegment(sketch, "E326", {"start": v(-15.37, 1.85) * mm, "end": v(-15.2, 1.76) * mm});
            skLineSegment(sketch, "E327", {"start": v(3.83, 2.03) * mm, "end": v(3.58, 1.27) * mm});
            skLineSegment(sketch, "E328", {"start": v(-27.6, -3.43) * mm, "end": v(-26.93, -3.94) * mm});
            skLineSegment(sketch, "E329", {"start": v(12.68, 3.32) * mm, "end": v(13.15, 2.71) * mm});
            skLineSegment(sketch, "E330", {"start": v(14.96, -4.78) * mm, "end": v(14.96, 4.8) * mm});
            skLineSegment(sketch, "E331", {"start": v(-2.67, 0.77) * mm, "end": v(-0.75, 0.77) * mm});
            skLineSegment(sketch, "E332", {"start": v(-15.51, 2.15) * mm, "end": v(-15.52, 2.08) * mm});
            skLineSegment(sketch, "E333", {"start": v(-17.65, 3.79) * mm, "end": v(-17.97, 3.4) * mm});
            skLineSegment(sketch, "E334", {"start": v(32.22, 2.28) * mm, "end": v(29.66, 2.28) * mm});
            skLineSegment(sketch, "E335", {"start": v(14.96, 4.8) * mm, "end": v(20.4, 4.8) * mm});
            skLineSegment(sketch, "E336", {"start": v(-10.41, 3.62) * mm, "end": v(-11.97, 1.56) * mm});
            skLineSegment(sketch, "E337", {"start": v(-2.67, 2.28) * mm, "end": v(-0.75, 2.28) * mm});
            skLineSegment(sketch, "E338", {"start": v(-15.47, 2.28) * mm, "end": v(-15.48, 2.25) * mm});
            skLineSegment(sketch, "E339", {"start": v(0.03, 1.3) * mm, "end": v(0, 1.25) * mm});
            skLineSegment(sketch, "E340", {"start": v(26.76, 2.28) * mm, "end": v(26.76, -4.78) * mm});
            skLineSegment(sketch, "E341", {"start": v(-26.93, -3.94) * mm, "end": v(-26.17, -4.36) * mm});
            skLineSegment(sketch, "E342", {"start": v(-22.08, -1.76) * mm, "end": v(-21.97, -1.87) * mm});
            skLineSegment(sketch, "E343", {"start": v(13.52, 2.03) * mm, "end": v(13.77, 1.27) * mm});
            skLineSegment(sketch, "E344", {"start": v(-19.9, -3.9) * mm, "end": v(-20.1, -4.08) * mm});
            skLineSegment(sketch, "E345", {"start": v(-18.42, 2.26) * mm, "end": v(-18.46, 1.78) * mm});
            skLineSegment(sketch, "E346", {"start": v(8.08, 2.34) * mm, "end": v(7.73, 2.22) * mm});
            skLineSegment(sketch, "E347", {"start": v(-16.39, -1.93) * mm, "end": v(-15.78, -2.21) * mm});
            skLineSegment(sketch, "E348", {"start": v(-25.73, -1.57) * mm, "end": v(-25.2, -1.93) * mm});
            skLineSegment(sketch, "E349", {"start": v(-15.48, 2.25) * mm, "end": v(-15.5, 2.22) * mm});
            skLineSegment(sketch, "E350", {"start": v(-0.08, 1.96) * mm, "end": v(-0.05, 1.9) * mm});
            skLineSegment(sketch, "E351", {"start": v(6.38, 0.2) * mm, "end": v(6.38, -0.2) * mm});
            skLineSegment(sketch, "E352", {"start": v(9.27, 2.34) * mm, "end": v(9.62, 2.22) * mm});
            skLineSegment(sketch, "E353", {"start": v(-20.57, -4.39) * mm, "end": v(-21.1, -4.63) * mm});
            skLineSegment(sketch, "E354", {"start": v(-13.16, -1.87) * mm, "end": v(-13.12, -2) * mm});
            skLineSegment(sketch, "E355", {"start": v(-15.5, 2.22) * mm, "end": v(-15.5, 2.18) * mm});
            skLineSegment(sketch, "E356", {"start": v(39.3, -3.66) * mm, "end": v(39.65, -4.78) * mm});
            skLineSegment(sketch, "E357", {"start": v(-23.68, 4.94) * mm, "end": v(-22.83, 4.94) * mm});
            skLineSegment(sketch, "E358", {"start": v(-26.17, -4.36) * mm, "end": v(-25.3, -4.68) * mm});
            skLineSegment(sketch, "E359", {"start": v(-21.97, -1.87) * mm, "end": v(-21.93, -2) * mm});
            skLineSegment(sketch, "E360", {"start": v(-0.12, 2) * mm, "end": v(-0.08, 1.96) * mm});
            skLineSegment(sketch, "E361", {"start": v(6.6, -4.6) * mm, "end": v(7.4, -4.82) * mm});
            skLineSegment(sketch, "E362", {"start": v(-19.71, -3.7) * mm, "end": v(-19.9, -3.9) * mm});
            skLineSegment(sketch, "E363", {"start": v(-23.68, 4.94) * mm, "end": v(-24.4, 4.85) * mm});
            skLineSegment(sketch, "E364", {"start": v(-27.11, 2.73) * mm, "end": v(-27.23, 2.26) * mm});
            skLineSegment(sketch, "E365", {"start": v(-14.96, 1.69) * mm, "end": v(-12.85, 1.23) * mm});
            skLineSegment(sketch, "E366", {"start": v(9.96, -4.82) * mm, "end": v(9.11, -4.94) * mm});
            skLineSegment(sketch, "E367", {"start": v(4.67, 3.32) * mm, "end": v(4.2, 2.71) * mm});
            skLineSegment(sketch, "E368", {"start": v(0.05, 1.44) * mm, "end": v(0.03, 1.3) * mm});
            skLineSegment(sketch, "E369", {"start": v(35.86, -3.66) * mm, "end": v(35.51, -4.78) * mm});
            skLineSegment(sketch, "E370", {"start": v(-26.78, 3.4) * mm, "end": v(-26.91, 3.18) * mm});
            skLineSegment(sketch, "E371", {"start": v(35.86, -3.66) * mm, "end": v(39.3, -3.66) * mm});
            skLineSegment(sketch, "E372", {"start": v(10.97, 0.2) * mm, "end": v(10.97, -0.2) * mm});
            skLineSegment(sketch, "E373", {"start": v(-21.93, -2.04) * mm, "end": v(-21.94, -2.1) * mm});
            skLineSegment(sketch, "E374", {"start": v(2.96, 2.05) * mm, "end": v(3, 1.52) * mm});
            skLineSegment(sketch, "E375", {"start": v(-5.57, 4.8) * mm, "end": v(-0.12, 4.8) * mm});
            skLineSegment(sketch, "E376", {"start": v(13.52, -2.01) * mm, "end": v(13.15, -2.7) * mm});
            skLineSegment(sketch, "E377", {"start": v(-13.27, -1.76) * mm, "end": v(-13.16, -1.87) * mm});
            skLineSegment(sketch, "E378", {"start": v(6.43, 0.59) * mm, "end": v(6.38, 0.2) * mm});
            skLineSegment(sketch, "E379", {"start": v(-13.44, -1.68) * mm, "end": v(-13.27, -1.76) * mm});
            skLineSegment(sketch, "E380", {"start": v(-22.3, 2.32) * mm, "end": v(-22.89, 2.45) * mm});
            skLineSegment(sketch, "E381", {"start": v(10.91, 0.59) * mm, "end": v(10.97, 0.2) * mm});
            skLineSegment(sketch, "E382", {"start": v(-21.94, -2.1) * mm, "end": v(-21.96, -2.14) * mm});
            skLineSegment(sketch, "E383", {"start": v(23.14, -0.11) * mm, "end": v(22.95, -0.41) * mm});
            skLineSegment(sketch, "E384", {"start": v(-21.96, -2.14) * mm, "end": v(-21.99, -2.19) * mm});
            skLineSegment(sketch, "E385", {"start": v(20.52, 1.8) * mm, "end": v(20.55, 1.74) * mm});
            skLineSegment(sketch, "E386", {"start": v(-21.93, -2) * mm, "end": v(-21.93, -2.04) * mm});
            skLineSegment(sketch, "E387", {"start": v(-21.93, 4.83) * mm, "end": v(-21.08, 4.62) * mm});
            skLineSegment(sketch, "E388", {"start": v(20.5, 1.87) * mm, "end": v(20.52, 1.8) * mm});
            skLineSegment(sketch, "E389", {"start": v(3, 1.52) * mm, "end": v(2.96, 1) * mm});
            skLineSegment(sketch, "E390", {"start": v(-13.5, 2.32) * mm, "end": v(-12.91, 2.1) * mm});
            skLineSegment(sketch, "E391", {"start": v(-0.05, 1.9) * mm, "end": v(-0.02, 1.85) * mm});
            skLineSegment(sketch, "E392", {"start": v(-25.2, -1.93) * mm, "end": v(-24.6, -2.21) * mm});
            skLineSegment(sketch, "E393", {"start": v(20.46, 1.92) * mm, "end": v(20.5, 1.87) * mm});
            skLineSegment(sketch, "E394", {"start": v(3.83, -2.01) * mm, "end": v(4.2, -2.7) * mm});
            skLineSegment(sketch, "E395", {"start": v(17.86, 0.77) * mm, "end": v(19.7, 0.77) * mm});
            skLineSegment(sketch, "E396", {"start": v(-38.62, 4.8) * mm, "end": v(-42.63, 4.8) * mm});
            skLineSegment(sketch, "E397", {"start": v(-12.36, 1.82) * mm, "end": v(-11.97, 1.56) * mm});
            skLineSegment(sketch, "E398", {"start": v(-5.57, -4.78) * mm, "end": v(-5.57, 4.8) * mm});
            skLineSegment(sketch, "E399", {"start": v(6.54, 0.95) * mm, "end": v(6.43, 0.59) * mm});
            skLineSegment(sketch, "E400", {"start": v(-44.95, -4.78) * mm, "end": v(-43.66, -4.78) * mm});
            skLineSegment(sketch, "E401", {"start": v(0.03, 1.73) * mm, "end": v(0.05, 1.6) * mm});
            skLineSegment(sketch, "E402", {"start": v(0, 1.8) * mm, "end": v(0.03, 1.73) * mm});
            skLineSegment(sketch, "E403", {"start": v(-24.4, 4.85) * mm, "end": v(-25.02, 4.68) * mm});
            skLineSegment(sketch, "E404", {"start": v(-41.52, 0.98) * mm, "end": v(-41.52, -4.78) * mm});
            skLineSegment(sketch, "E405", {"start": v(-38.62, 4.8) * mm, "end": v(-38.62, -4.78) * mm});
            skLineSegment(sketch, "E406", {"start": v(22.95, -0.41) * mm, "end": v(22.73, -0.68) * mm});
            skLineSegment(sketch, "E407", {"start": v(-22.89, 2.45) * mm, "end": v(-23.18, 2.49) * mm});
            skLineSegment(sketch, "E408", {"start": v(-0.02, 1.85) * mm, "end": v(0, 1.8) * mm});
            skLineSegment(sketch, "E409", {"start": v(7.4, -4.82) * mm, "end": v(8.24, -4.94) * mm});
            skLineSegment(sketch, "E410", {"start": v(-19.04, -2.22) * mm, "end": v(-19.1, -2.5) * mm});
            skLineSegment(sketch, "E411", {"start": v(-41.52, 0.98) * mm, "end": v(-43.66, -4.78) * mm});
            skLineSegment(sketch, "E412", {"start": v(-22.83, 4.94) * mm, "end": v(-21.93, 4.83) * mm});
            skLineSegment(sketch, "E413", {"start": v(20.38, 2.02) * mm, "end": v(20.43, 1.97) * mm});
            skLineSegment(sketch, "E414", {"start": v(20.34, 2.06) * mm, "end": v(20.38, 2.02) * mm});
            skLineSegment(sketch, "E415", {"start": v(32.22, 4.8) * mm, "end": v(32.22, 2.28) * mm});
            skLineSegment(sketch, "E416", {"start": v(-38.62, -4.78) * mm, "end": v(-41.52, -4.78) * mm});
            skLineSegment(sketch, "E417", {"start": v(-13.67, -1.6) * mm, "end": v(-13.44, -1.68) * mm});
            skLineSegment(sketch, "E418", {"start": v(-20.1, -4.08) * mm, "end": v(-20.57, -4.39) * mm});
            skLineSegment(sketch, "E419", {"start": v(-16.92, -1.57) * mm, "end": v(-16.39, -1.93) * mm});
            skLineSegment(sketch, "E420", {"start": v(-2.67, -1.76) * mm, "end": v(-0.12, -1.75) * mm});
            skLineSegment(sketch, "E421", {"start": v(7.13, -1.82) * mm, "end": v(7.4, -2.04) * mm});
            skLineSegment(sketch, "E422", {"start": v(20.43, 1.97) * mm, "end": v(20.46, 1.92) * mm});
            skLineSegment(sketch, "E423", {"start": v(32.22, 4.8) * mm, "end": v(24.18, 4.8) * mm});
            skLineSegment(sketch, "E424", {"start": v(-10.37, -2.77) * mm, "end": v(-10.47, -3.03) * mm});
            skLineSegment(sketch, "E425", {"start": v(-26.91, 3.18) * mm, "end": v(-27.11, 2.73) * mm});
            skLineSegment(sketch, "E426", {"start": v(9.11, -4.94) * mm, "end": v(8.24, -4.94) * mm});
            skLineSegment(sketch, "E427", {"start": v(13.15, 2.71) * mm, "end": v(13.52, 2.03) * mm});
            skLineSegment(sketch, "E428", {"start": v(10.22, -1.82) * mm, "end": v(9.94, -2.04) * mm});
            skLineSegment(sketch, "E429", {"start": v(13.9, 0.44) * mm, "end": v(13.9, -0.43) * mm});
            skLineSegment(sketch, "E430", {"start": v(-10.47, -3.03) * mm, "end": v(-10.6, -3.27) * mm});
            skLineSegment(sketch, "E431", {"start": v(22.5, -0.9) * mm, "end": v(22.27, -1.1) * mm});
            skLineSegment(sketch, "E432", {"start": v(-12.91, 2.1) * mm, "end": v(-12.36, 1.82) * mm});
            skLineSegment(sketch, "E433", {"start": v(0.49, -1.66) * mm, "end": v(-0.12, -1.75) * mm});
            skLineSegment(sketch, "E434", {"start": v(8.88, 2.4) * mm, "end": v(9.27, 2.34) * mm});
            skLineSegment(sketch, "E435", {"start": v(24.18, 2.28) * mm, "end": v(24.18, 4.8) * mm});
            skLineSegment(sketch, "E436", {"start": v(-21.66, 1.23) * mm, "end": v(-20.87, 0.96) * mm});
            skLineSegment(sketch, "E437", {"start": v(22.73, -0.68) * mm, "end": v(22.5, -0.9) * mm});
            skLineSegment(sketch, "E438", {"start": v(24.18, 2.28) * mm, "end": v(26.76, 2.28) * mm});
            skLineSegment(sketch, "E439", {"start": v(3.45, 0.44) * mm, "end": v(3.45, -0.43) * mm});
            skLineSegment(sketch, "E440", {"start": v(4, 2.38) * mm, "end": v(3.83, 2.03) * mm});
            skLineSegment(sketch, "E441", {"start": v(2.68, 3.02) * mm, "end": v(2.85, 2.55) * mm});
            skLineSegment(sketch, "E442", {"start": v(24.18, 2.28) * mm, "end": v(32.22, 2.28) * mm});
            skLineSegment(sketch, "E443", {"start": v(8.47, 2.4) * mm, "end": v(8.08, 2.34) * mm});
            skLineSegment(sketch, "E444", {"start": v(-34.46, -3.66) * mm, "end": v(-34.8, -4.78) * mm});
            skLineSegment(sketch, "E445", {"start": v(-27.12, 0.78) * mm, "end": v(-26.95, 0.37) * mm});
            skLineSegment(sketch, "E446", {"start": v(-23.77, 1.69) * mm, "end": v(-21.66, 1.23) * mm});
            skLineSegment(sketch, "E447", {"start": v(2.85, 2.55) * mm, "end": v(2.96, 2.05) * mm});
            skLineSegment(sketch, "E448", {"start": v(19.84, 2.26) * mm, "end": v(19.98, 2.23) * mm});
            skLineSegment(sketch, "E449", {"start": v(-18.78, -3.43) * mm, "end": v(-18.12, -3.94) * mm});
            skSolve(sketch);
        }
        {
            var Q0;
            Q0=qCreatedBy(makeId("Top.planeOp"),FACE);
            var sketch = newSketch(context, id + "F1", { "sketchPlane" : qUnion([Q0])});
            skLineSegment(sketch, "E450.bottom", {"start": v(-56.49, 11.56) * mm, "end": v(55.51, 11.56) * mm});
            skLineSegment(sketch, "E450.top", {"start": v(-56.49, -25.44) * mm, "end": v(55.51, -25.44) * mm});
            skLineSegment(sketch, "E450.left", {"start": v(-56.49, 11.56) * mm, "end": v(-56.49, -25.44) * mm});
            skLineSegment(sketch, "E450.right", {"start": v(55.51, 11.56) * mm, "end": v(55.51, -25.44) * mm});
            skSolve(sketch);
        }
        {
            var Q0;
            Q0=makeQuery(id+"F1.imprint","IMPRINT",FACE,{"disambiguationData":[TD([[makeQuery(id+"F1.imprint","IMPRINT",EDGE,{"derivedFrom":sQuery(id+"F1.wireOp",EDGE,"E450.bottom")}),-1.0]])]});
            extrude(context, id + "F2", {"entities" : qUnion([Q0]), "depth" : 2 * mm});
        }
        {
            var Q0;
            Q0 = qSketchRegion(id + "F0", true);
            extrude(context, id + "F3", {"entities" : qUnion([Q0]), "operationType" : NewBodyOperationType.ADD, "depth" : 3 * mm});
        }
        {
            var Q0;
            {var subQ0=sQuery(id+"F1.wireOp",EDGE,"E450.left");var subQ1=sQuery(id+"F1.wireOp",EDGE,"E450.right");var subQ2=sQuery(id+"F1.wireOp",EDGE,"E450.bottom");var subQ4=sQuery(id+"F1.wireOp",EDGE,"E450.top");Q0=makeQuery(id+"F3.boolean.opBoolean","SPLIT",FACE,{"disambiguationData":[TD([makeQuery(id+"F2.opExtrude","SWEPT_FACE",FACE,{"disambiguationData":[OSD([subQ2])]})])],"derivedFrom":makeQuery(id+"F2.opExtrude","CAP_FACE",FACE,{"disambiguationData":[OSD([subQ2,subQ4,subQ0,subQ1])],"isStart":false})});}
            var sketch = newSketch(context, id + "F4", { "sketchPlane" : qUnion([Q0])});
            skLineSegment(sketch, "E451", {"start": v(9.79, -16.78) * mm, "end": v(9.77, -16.82) * mm});
            skLineSegment(sketch, "E452", {"start": v(-46.22, -13.66) * mm, "end": v(-46.23, -13.7) * mm});
            skLineSegment(sketch, "E453", {"start": v(-14.84, -13.91) * mm, "end": v(-14.87, -13.92) * mm});
            skLineSegment(sketch, "E454", {"start": v(6.08, -16.28) * mm, "end": v(6.04, -16.34) * mm});
            skLineSegment(sketch, "E455", {"start": v(49.15, -13.83) * mm, "end": v(49.2, -13.87) * mm});
            skLineSegment(sketch, "E456", {"start": v(-3.63, -16.04) * mm, "end": v(-3.7, -16.06) * mm});
            skLineSegment(sketch, "E457", {"start": v(-0.3, -16.26) * mm, "end": v(-0.28, -16.3) * mm});
            skLineSegment(sketch, "E458", {"start": v(39.5, -12.88) * mm, "end": v(39.56, -12.89) * mm});
            skLineSegment(sketch, "E459", {"start": v(48.96, -15.03) * mm, "end": v(48.97, -15.1) * mm});
            skLineSegment(sketch, "E460", {"start": v(46.73, -16.03) * mm, "end": v(46.8, -16.04) * mm});
            skLineSegment(sketch, "E461", {"start": v(49.88, -16.2) * mm, "end": v(49.92, -16.26) * mm});
            skLineSegment(sketch, "E462", {"start": v(6.97, -16.33) * mm, "end": v(7, -16.39) * mm});
            skLineSegment(sketch, "E463", {"start": v(49.8, -13.86) * mm, "end": v(49.74, -13.9) * mm});
            skLineSegment(sketch, "E464", {"start": v(29.91, -16.6) * mm, "end": v(29.9, -16.68) * mm});
            skLineSegment(sketch, "E465", {"start": v(-26.47, -16.03) * mm, "end": v(-26.41, -16.05) * mm});
            skLineSegment(sketch, "E466", {"start": v(50, -15.07) * mm, "end": v(49.98, -15.14) * mm});
            skLineSegment(sketch, "E467", {"start": v(-46.16, -16.53) * mm, "end": v(-46.16, -16.6) * mm});
            skLineSegment(sketch, "E468", {"start": v(46.66, -16.03) * mm, "end": v(46.73, -16.03) * mm});
            skLineSegment(sketch, "E469", {"start": v(-16.12, -15.3) * mm, "end": v(-16.16, -15.36) * mm});
            skLineSegment(sketch, "E470", {"start": v(30.93, -12.88) * mm, "end": v(31, -12.89) * mm});
            skLineSegment(sketch, "E471", {"start": v(-44.97, -13.91) * mm, "end": v(-45, -13.92) * mm});
            skLineSegment(sketch, "E472", {"start": v(9.62, -13.86) * mm, "end": v(9.56, -13.9) * mm});
            skLineSegment(sketch, "E473", {"start": v(28.89, -16.68) * mm, "end": v(28.9, -16.75) * mm});
            skLineSegment(sketch, "E474", {"start": v(30.79, -12.89) * mm, "end": v(30.72, -12.9) * mm});
            skLineSegment(sketch, "E475", {"start": v(21.07, -14.5) * mm, "end": v(21.12, -14.54) * mm});
            skLineSegment(sketch, "E476", {"start": v(39.35, -12.89) * mm, "end": v(39.29, -12.9) * mm});
            skLineSegment(sketch, "E477", {"start": v(31, -12.89) * mm, "end": v(31.05, -12.9) * mm});
            skLineSegment(sketch, "E478", {"start": v(-0.83, -13.95) * mm, "end": v(-0.77, -13.96) * mm});
            skLineSegment(sketch, "E479", {"start": v(9.56, -13.9) * mm, "end": v(9.5, -13.92) * mm});
            skLineSegment(sketch, "E480", {"start": v(-24.68, -13.72) * mm, "end": v(-24.73, -13.78) * mm});
            skLineSegment(sketch, "E481", {"start": v(-0.34, -16.2) * mm, "end": v(-0.3, -16.26) * mm});
            skLineSegment(sketch, "E482", {"start": v(28.88, -16.61) * mm, "end": v(28.89, -16.68) * mm});
            skLineSegment(sketch, "E483", {"start": v(-26.68, -16.03) * mm, "end": v(-26.74, -16.05) * mm});
            skLineSegment(sketch, "E484", {"start": v(49.92, -16.26) * mm, "end": v(49.94, -16.3) * mm});
            skLineSegment(sketch, "E485", {"start": v(-39.67, -17.07) * mm, "end": v(-39.61, -17.1) * mm});
            skLineSegment(sketch, "E486", {"start": v(-1.02, -13.87) * mm, "end": v(-0.96, -13.9) * mm});
            skLineSegment(sketch, "E487", {"start": v(-17.05, -15.14) * mm, "end": v(-17.03, -15.2) * mm});
            skLineSegment(sketch, "E488", {"start": v(-19.44, -16.04) * mm, "end": v(-19.5, -16.06) * mm});
            skLineSegment(sketch, "E489", {"start": v(-19.12, -16.08) * mm, "end": v(-19.06, -16.12) * mm});
            skLineSegment(sketch, "E490", {"start": v(-25.55, -13.72) * mm, "end": v(-25.5, -13.77) * mm});
            skLineSegment(sketch, "E491", {"start": v(-16.15, -16.2) * mm, "end": v(-16.11, -16.26) * mm});
            skLineSegment(sketch, "E492", {"start": v(-15.2, -13.95) * mm, "end": v(-15.15, -13.96) * mm});
            skLineSegment(sketch, "E493", {"start": v(-47.17, -13.6) * mm, "end": v(-47.15, -13.66) * mm});
            skLineSegment(sketch, "E494", {"start": v(16.09, -16.34) * mm, "end": v(16.06, -16.4) * mm});
            skLineSegment(sketch, "E495", {"start": v(-47.2, -16.54) * mm, "end": v(-47.2, -16.61) * mm});
            skLineSegment(sketch, "E496", {"start": v(29, -15.35) * mm, "end": v(29.06, -15.4) * mm});
            skLineSegment(sketch, "E497", {"start": v(-39.16, -17.03) * mm, "end": v(-39.22, -17.07) * mm});
            skLineSegment(sketch, "E498", {"start": v(-14.79, -13.88) * mm, "end": v(-14.84, -13.91) * mm});
            skLineSegment(sketch, "E499", {"start": v(-15.36, -13.87) * mm, "end": v(-15.3, -13.9) * mm});
            skLineSegment(sketch, "E500", {"start": v(-44.92, -13.88) * mm, "end": v(-44.97, -13.91) * mm});
            skLineSegment(sketch, "E501", {"start": v(17.01, -16.33) * mm, "end": v(17.04, -16.39) * mm});
            skLineSegment(sketch, "E502", {"start": v(19.87, -16.57) * mm, "end": v(19.87, -16.64) * mm});
            skLineSegment(sketch, "E503", {"start": v(-49.1, -16.2) * mm, "end": v(-49.05, -16.27) * mm});
            skLineSegment(sketch, "E504", {"start": v(26.13, -16.34) * mm, "end": v(26.1, -16.4) * mm});
            skLineSegment(sketch, "E505", {"start": v(-0.48, -13.9) * mm, "end": v(-0.54, -13.92) * mm});
            skLineSegment(sketch, "E506", {"start": v(6.9, -16.2) * mm, "end": v(6.94, -16.27) * mm});
            skLineSegment(sketch, "E507", {"start": v(9.2, -13.95) * mm, "end": v(9.28, -13.96) * mm});
            skLineSegment(sketch, "E508", {"start": v(-25.6, -13.6) * mm, "end": v(-25.58, -13.66) * mm});
            skLineSegment(sketch, "E509", {"start": v(20.62, -14.5) * mm, "end": v(20.56, -14.54) * mm});
            skLineSegment(sketch, "E510", {"start": v(18.83, -16.54) * mm, "end": v(18.83, -16.61) * mm});
            skLineSegment(sketch, "E511", {"start": v(-1.2, -16.34) * mm, "end": v(-1.23, -16.4) * mm});
            skLineSegment(sketch, "E512", {"start": v(16.06, -16.4) * mm, "end": v(16.05, -16.44) * mm});
            skLineSegment(sketch, "E513", {"start": v(-26.08, -14.96) * mm, "end": v(-26.08, -15.03) * mm});
            skLineSegment(sketch, "E514", {"start": v(-47.14, -16.34) * mm, "end": v(-47.17, -16.4) * mm});
            skLineSegment(sketch, "E515", {"start": v(49.96, -15.2) * mm, "end": v(49.95, -15.24) * mm});
            skLineSegment(sketch, "E516", {"start": v(19.25, -15.53) * mm, "end": v(19.32, -15.54) * mm});
            skLineSegment(sketch, "E517", {"start": v(8.8, -16.54) * mm, "end": v(8.8, -16.61) * mm});
            skLineSegment(sketch, "E518", {"start": v(6.02, -16.4) * mm, "end": v(6, -16.44) * mm});
            skLineSegment(sketch, "E519", {"start": v(19.83, -16.78) * mm, "end": v(19.82, -16.82) * mm});
            skLineSegment(sketch, "E520", {"start": v(-16.93, -16.22) * mm, "end": v(-16.98, -16.28) * mm});
            skLineSegment(sketch, "E521", {"start": v(16.94, -16.2) * mm, "end": v(16.98, -16.27) * mm});
            skLineSegment(sketch, "E522", {"start": v(-3.75, -16.09) * mm, "end": v(-3.81, -16.12) * mm});
            skLineSegment(sketch, "E523", {"start": v(-14.94, -13.95) * mm, "end": v(-15, -13.96) * mm});
            skLineSegment(sketch, "E524", {"start": v(49, -15.17) * mm, "end": v(49.02, -15.24) * mm});
            skLineSegment(sketch, "E525", {"start": v(-46.27, -13.75) * mm, "end": v(-46.32, -13.8) * mm});
            skLineSegment(sketch, "E526", {"start": v(-49.37, -16.04) * mm, "end": v(-49.3, -16.06) * mm});
            skLineSegment(sketch, "E527", {"start": v(29.78, -15.36) * mm, "end": v(29.73, -15.41) * mm});
            skLineSegment(sketch, "E528", {"start": v(-0.63, -13.95) * mm, "end": v(-0.7, -13.96) * mm});
            skLineSegment(sketch, "E529", {"start": v(-0.23, -15.14) * mm, "end": v(-0.26, -15.2) * mm});
            skLineSegment(sketch, "E530", {"start": v(49.9, -13.75) * mm, "end": v(49.85, -13.8) * mm});
            skLineSegment(sketch, "E531", {"start": v(49.2, -13.87) * mm, "end": v(49.26, -13.9) * mm});
            skLineSegment(sketch, "E532", {"start": v(-3.42, -16.04) * mm, "end": v(-3.36, -16.06) * mm});
            skLineSegment(sketch, "E533", {"start": v(-16.03, -14.96) * mm, "end": v(-16.03, -15.03) * mm});
            skLineSegment(sketch, "E534", {"start": v(-1.12, -16.22) * mm, "end": v(-1.16, -16.28) * mm});
            skLineSegment(sketch, "E535", {"start": v(29.89, -16.75) * mm, "end": v(29.86, -16.82) * mm});
            skLineSegment(sketch, "E536", {"start": v(26.98, -16.2) * mm, "end": v(27.02, -16.27) * mm});
            skLineSegment(sketch, "E537", {"start": v(-47.07, -13.77) * mm, "end": v(-47.02, -13.83) * mm});
            skLineSegment(sketch, "E538", {"start": v(-39.34, -17.11) * mm, "end": v(-39.41, -17.12) * mm});
            skLineSegment(sketch, "E539", {"start": v(9.83, -16.57) * mm, "end": v(9.82, -16.64) * mm});
            skLineSegment(sketch, "E540", {"start": v(6.04, -16.34) * mm, "end": v(6.02, -16.4) * mm});
            skLineSegment(sketch, "E541", {"start": v(18.96, -15.35) * mm, "end": v(19.02, -15.4) * mm});
            skLineSegment(sketch, "E542", {"start": v(9.72, -13.75) * mm, "end": v(9.67, -13.8) * mm});
            skLineSegment(sketch, "E543", {"start": v(-24.63, -13.6) * mm, "end": v(-24.65, -13.66) * mm});
            skLineSegment(sketch, "E544", {"start": v(9.03, -13.87) * mm, "end": v(9.09, -13.9) * mm});
            skLineSegment(sketch, "E545", {"start": v(-3.3, -16.08) * mm, "end": v(-3.25, -16.12) * mm});
            skLineSegment(sketch, "E546", {"start": v(36.53, -17.11) * mm, "end": v(36.6, -17.12) * mm});
            skLineSegment(sketch, "E547", {"start": v(49.96, -16.36) * mm, "end": v(49.98, -16.42) * mm});
            skLineSegment(sketch, "E548", {"start": v(28.88, -16.54) * mm, "end": v(28.88, -16.61) * mm});
            skLineSegment(sketch, "E549", {"start": v(-26.98, -16.22) * mm, "end": v(-27.02, -16.28) * mm});
            skLineSegment(sketch, "E550", {"start": v(29.91, -16.53) * mm, "end": v(29.91, -16.6) * mm});
            skLineSegment(sketch, "E551", {"start": v(-46.19, -13.6) * mm, "end": v(-46.22, -13.66) * mm});
            skLineSegment(sketch, "E552", {"start": v(46.8, -16.04) * mm, "end": v(46.86, -16.06) * mm});
            skLineSegment(sketch, "E553", {"start": v(29.68, -15.45) * mm, "end": v(29.62, -15.49) * mm});
            skLineSegment(sketch, "E554", {"start": v(7, -16.39) * mm, "end": v(7, -16.46) * mm});
            skLineSegment(sketch, "E555", {"start": v(30.66, -12.93) * mm, "end": v(30.6, -12.97) * mm});
            skLineSegment(sketch, "E556", {"start": v(31.11, -12.93) * mm, "end": v(31.17, -12.96) * mm});
            skLineSegment(sketch, "E557", {"start": v(49.74, -13.9) * mm, "end": v(49.68, -13.92) * mm});
            skLineSegment(sketch, "E558", {"start": v(-16.03, -16.6) * mm, "end": v(-16.04, -16.68) * mm});
            skLineSegment(sketch, "E559", {"start": v(-26.2, -16.2) * mm, "end": v(-26.16, -16.26) * mm});
            skLineSegment(sketch, "E560", {"start": v(18.86, -16.75) * mm, "end": v(18.89, -16.82) * mm});
            skLineSegment(sketch, "E561", {"start": v(-26.2, -14.63) * mm, "end": v(-26.16, -14.69) * mm});
            skLineSegment(sketch, "E562", {"start": v(-29.35, -16.03) * mm, "end": v(-29.28, -16.04) * mm});
            skLineSegment(sketch, "E563", {"start": v(39.23, -12.93) * mm, "end": v(39.17, -12.97) * mm});
            skLineSegment(sketch, "E564", {"start": v(16.17, -16.22) * mm, "end": v(16.12, -16.28) * mm});
            skLineSegment(sketch, "E565", {"start": v(0.67, -13.96) * mm, "end": v(0.74, -13.96) * mm});
            skLineSegment(sketch, "E566", {"start": v(8.82, -16.75) * mm, "end": v(8.84, -16.82) * mm});
            skLineSegment(sketch, "E567", {"start": v(-1.17, -13.72) * mm, "end": v(-1.12, -13.77) * mm});
            skLineSegment(sketch, "E568", {"start": v(46.66, -16.03) * mm, "end": v(46.6, -16.04) * mm});
            skLineSegment(sketch, "E569", {"start": v(-1.07, -15.4) * mm, "end": v(-1.02, -15.45) * mm});
            skLineSegment(sketch, "E570", {"start": v(0.8, -13.96) * mm, "end": v(0.74, -13.96) * mm});
            skLineSegment(sketch, "E571", {"start": v(6.12, -16.22) * mm, "end": v(6.08, -16.28) * mm});
            skLineSegment(sketch, "E572", {"start": v(49.1, -13.77) * mm, "end": v(49.15, -13.83) * mm});
            skLineSegment(sketch, "E573", {"start": v(-17.06, -16.65) * mm, "end": v(-17.05, -16.72) * mm});
            skLineSegment(sketch, "E574", {"start": v(-0.44, -16.11) * mm, "end": v(-0.39, -16.16) * mm});
            skLineSegment(sketch, "E575", {"start": v(-17.06, -14.92) * mm, "end": v(-17.07, -15) * mm});
            skLineSegment(sketch, "E576", {"start": v(39.56, -12.89) * mm, "end": v(39.62, -12.9) * mm});
            skLineSegment(sketch, "E577", {"start": v(-26.92, -14.59) * mm, "end": v(-26.98, -14.64) * mm});
            skLineSegment(sketch, "E578", {"start": v(28.9, -16.75) * mm, "end": v(28.93, -16.82) * mm});
            skLineSegment(sketch, "E579", {"start": v(26.2, -16.22) * mm, "end": v(26.16, -16.28) * mm});
            skLineSegment(sketch, "E580", {"start": v(48.96, -14.96) * mm, "end": v(48.96, -15.03) * mm});
            skLineSegment(sketch, "E581", {"start": v(50, -15) * mm, "end": v(50, -15.07) * mm});
            skLineSegment(sketch, "E582", {"start": v(-19.37, -16.03) * mm, "end": v(-19.44, -16.04) * mm});
            skLineSegment(sketch, "E583", {"start": v(-45.54, -13.83) * mm, "end": v(-45.49, -13.87) * mm});
            skLineSegment(sketch, "E584", {"start": v(-0.35, -15.36) * mm, "end": v(-0.4, -15.41) * mm});
            skLineSegment(sketch, "E585", {"start": v(36.73, -17.11) * mm, "end": v(36.66, -17.12) * mm});
            skLineSegment(sketch, "E586", {"start": v(26.83, -16.08) * mm, "end": v(26.88, -16.12) * mm});
            skLineSegment(sketch, "E587", {"start": v(-47.19, -16.68) * mm, "end": v(-47.17, -16.75) * mm});
            skLineSegment(sketch, "E588", {"start": v(-49.5, -16.03) * mm, "end": v(-49.57, -16.04) * mm});
            skLineSegment(sketch, "E589", {"start": v(49.98, -15.14) * mm, "end": v(49.96, -15.2) * mm});
            skLineSegment(sketch, "E590", {"start": v(-49.5, -16.03) * mm, "end": v(-49.43, -16.03) * mm});
            skLineSegment(sketch, "E591", {"start": v(49.1, -16.22) * mm, "end": v(49.06, -16.28) * mm});
            skLineSegment(sketch, "E592", {"start": v(-14.68, -13.78) * mm, "end": v(-14.73, -13.83) * mm});
            skLineSegment(sketch, "E593", {"start": v(-44.81, -13.78) * mm, "end": v(-44.86, -13.83) * mm});
            skLineSegment(sketch, "E594", {"start": v(-46.16, -16.6) * mm, "end": v(-46.17, -16.68) * mm});
            skLineSegment(sketch, "E595", {"start": v(49.96, -14.78) * mm, "end": v(49.98, -14.85) * mm});
            skLineSegment(sketch, "E596", {"start": v(-15.46, -13.77) * mm, "end": v(-15.41, -13.83) * mm});
            skLineSegment(sketch, "E597", {"start": v(-49.43, -16.03) * mm, "end": v(-49.37, -16.04) * mm});
            skLineSegment(sketch, "E598", {"start": v(-36.67, -13.96) * mm, "end": v(-36.6, -13.96) * mm});
            skLineSegment(sketch, "E599", {"start": v(29.5, -15.53) * mm, "end": v(29.43, -15.54) * mm});
            skLineSegment(sketch, "E600", {"start": v(-24.6, -13.45) * mm, "end": v(-24.6, -13.53) * mm});
            skLineSegment(sketch, "E601", {"start": v(-45.49, -13.87) * mm, "end": v(-45.43, -13.9) * mm});
            skLineSegment(sketch, "E602", {"start": v(19.82, -15.24) * mm, "end": v(19.78, -15.3) * mm});
            skLineSegment(sketch, "E603", {"start": v(20.5, -14.59) * mm, "end": v(20.45, -14.64) * mm});
            skLineSegment(sketch, "E604", {"start": v(-1.06, -16.16) * mm, "end": v(-1.12, -16.22) * mm});
            skLineSegment(sketch, "E605", {"start": v(-46.9, -13.9) * mm, "end": v(-46.84, -13.94) * mm});
            skLineSegment(sketch, "E606", {"start": v(29.83, -16.88) * mm, "end": v(29.78, -16.93) * mm});
            skLineSegment(sketch, "E607", {"start": v(16.04, -16.5) * mm, "end": v(16.03, -16.58) * mm});
            skLineSegment(sketch, "E608", {"start": v(-47.06, -16.22) * mm, "end": v(-47.1, -16.28) * mm});
            skLineSegment(sketch, "E609", {"start": v(29.3, -15.53) * mm, "end": v(29.36, -15.54) * mm});
            skLineSegment(sketch, "E610", {"start": v(-1.12, -15.35) * mm, "end": v(-1.07, -15.4) * mm});
            skLineSegment(sketch, "E611", {"start": v(8.82, -16.4) * mm, "end": v(8.8, -16.47) * mm});
            skLineSegment(sketch, "E612", {"start": v(-36.72, -12.89) * mm, "end": v(-36.79, -12.9) * mm});
            skLineSegment(sketch, "E613", {"start": v(29.36, -15.54) * mm, "end": v(29.43, -15.54) * mm});
            skLineSegment(sketch, "E614", {"start": v(18.92, -15.3) * mm, "end": v(18.96, -15.35) * mm});
            skLineSegment(sketch, "E615", {"start": v(21.12, -14.54) * mm, "end": v(21.18, -14.58) * mm});
            skLineSegment(sketch, "E616", {"start": v(30.77, -15.53) * mm, "end": v(30.83, -15.54) * mm});
            skLineSegment(sketch, "E617", {"start": v(18.89, -15.24) * mm, "end": v(18.92, -15.3) * mm});
            skLineSegment(sketch, "E618", {"start": v(-24.73, -13.78) * mm, "end": v(-24.78, -13.83) * mm});
            skLineSegment(sketch, "E619", {"start": v(10.77, -14.45) * mm, "end": v(10.84, -14.45) * mm});
            skLineSegment(sketch, "E620", {"start": v(-17.07, -16.57) * mm, "end": v(-17.06, -16.65) * mm});
            skLineSegment(sketch, "E621", {"start": v(16.84, -16.12) * mm, "end": v(16.9, -16.16) * mm});
            skLineSegment(sketch, "E622", {"start": v(-36.52, -12.89) * mm, "end": v(-36.45, -12.9) * mm});
            skLineSegment(sketch, "E623", {"start": v(39.74, -12.96) * mm, "end": v(39.79, -13) * mm});
            skLineSegment(sketch, "E624", {"start": v(18.96, -16.93) * mm, "end": v(19.02, -16.99) * mm});
            skLineSegment(sketch, "E625", {"start": v(26.38, -16.09) * mm, "end": v(26.32, -16.12) * mm});
            skLineSegment(sketch, "E626", {"start": v(7.02, -16.6) * mm, "end": v(7, -16.68) * mm});
            skLineSegment(sketch, "E627", {"start": v(9.82, -16.5) * mm, "end": v(9.83, -16.57) * mm});
            skLineSegment(sketch, "E628", {"start": v(-25.5, -13.77) * mm, "end": v(-25.45, -13.83) * mm});
            skLineSegment(sketch, "E629", {"start": v(10.84, -14.45) * mm, "end": v(10.9, -14.46) * mm});
            skLineSegment(sketch, "E630", {"start": v(31.04, -15.52) * mm, "end": v(30.97, -15.53) * mm});
            skLineSegment(sketch, "E631", {"start": v(19.83, -15.2) * mm, "end": v(19.82, -15.24) * mm});
            skLineSegment(sketch, "E632", {"start": v(-0.22, -15) * mm, "end": v(-0.22, -15.07) * mm});
            skLineSegment(sketch, "E633", {"start": v(9.28, -13.96) * mm, "end": v(9.35, -13.96) * mm});
            skLineSegment(sketch, "E634", {"start": v(49.95, -13.66) * mm, "end": v(49.93, -13.7) * mm});
            skLineSegment(sketch, "E635", {"start": v(19.46, -13.95) * mm, "end": v(19.39, -13.96) * mm});
            skLineSegment(sketch, "E636", {"start": v(-15.15, -13.96) * mm, "end": v(-15.08, -13.96) * mm});
            skLineSegment(sketch, "E637", {"start": v(-1, -16.12) * mm, "end": v(-1.06, -16.16) * mm});
            skLineSegment(sketch, "E638", {"start": v(49, -16.4) * mm, "end": v(48.97, -16.47) * mm});
            skLineSegment(sketch, "E639", {"start": v(-19.06, -16.12) * mm, "end": v(-19, -16.16) * mm});
            skLineSegment(sketch, "E640", {"start": v(-1.25, -15.03) * mm, "end": v(-1.24, -15.1) * mm});
            skLineSegment(sketch, "E641", {"start": v(-16.32, -15.49) * mm, "end": v(-16.38, -15.52) * mm});
            skLineSegment(sketch, "E642", {"start": v(17.04, -16.39) * mm, "end": v(17.05, -16.46) * mm});
            skLineSegment(sketch, "E643", {"start": v(9.41, -13.95) * mm, "end": v(9.35, -13.96) * mm});
            skLineSegment(sketch, "E644", {"start": v(9.8, -16.42) * mm, "end": v(9.82, -16.5) * mm});
            skLineSegment(sketch, "E645", {"start": v(-0.23, -16.42) * mm, "end": v(-0.22, -16.5) * mm});
            skLineSegment(sketch, "E646", {"start": v(-27.1, -14.92) * mm, "end": v(-27.11, -15) * mm});
            skLineSegment(sketch, "E647", {"start": v(50, -16.5) * mm, "end": v(50, -16.57) * mm});
            skLineSegment(sketch, "E648", {"start": v(28.9, -16.4) * mm, "end": v(28.89, -16.47) * mm});
            skLineSegment(sketch, "E649", {"start": v(-46.42, -13.9) * mm, "end": v(-46.48, -13.92) * mm});
            skLineSegment(sketch, "E650", {"start": v(-46.24, -16.26) * mm, "end": v(-46.21, -16.32) * mm});
            skLineSegment(sketch, "E651", {"start": v(46.92, -16.08) * mm, "end": v(46.97, -16.12) * mm});
            skLineSegment(sketch, "E652", {"start": v(8.92, -13.77) * mm, "end": v(8.97, -13.83) * mm});
            skLineSegment(sketch, "E653", {"start": v(-16.98, -15.3) * mm, "end": v(-16.94, -15.35) * mm});
            skLineSegment(sketch, "E654", {"start": v(-19.63, -16.12) * mm, "end": v(-19.68, -16.17) * mm});
            skLineSegment(sketch, "E655", {"start": v(19.74, -16.93) * mm, "end": v(19.7, -16.99) * mm});
            skLineSegment(sketch, "E656", {"start": v(29.89, -16.39) * mm, "end": v(29.9, -16.46) * mm});
            skLineSegment(sketch, "E657", {"start": v(19.78, -15.3) * mm, "end": v(19.74, -15.36) * mm});
            skLineSegment(sketch, "E658", {"start": v(-25.62, -13.53) * mm, "end": v(-25.6, -13.6) * mm});
            skLineSegment(sketch, "E659", {"start": v(-1.23, -16.4) * mm, "end": v(-1.24, -16.47) * mm});
            skLineSegment(sketch, "E660", {"start": v(39.1, -13.01) * mm, "end": v(39.06, -13.07) * mm});
            skLineSegment(sketch, "E661", {"start": v(-15, -13.96) * mm, "end": v(-15.08, -13.96) * mm});
            skLineSegment(sketch, "E662", {"start": v(0.92, -12.9) * mm, "end": v(0.98, -12.93) * mm});
            skLineSegment(sketch, "E663", {"start": v(8.88, -16.88) * mm, "end": v(8.92, -16.93) * mm});
            skLineSegment(sketch, "E664", {"start": v(5.99, -16.58) * mm, "end": v(6, -16.65) * mm});
            skLineSegment(sketch, "E665", {"start": v(-19.3, -16.03) * mm, "end": v(-19.24, -16.04) * mm});
            skLineSegment(sketch, "E666", {"start": v(49.98, -16.42) * mm, "end": v(50, -16.5) * mm});
            skLineSegment(sketch, "E667", {"start": v(-0.22, -16.5) * mm, "end": v(-0.22, -16.57) * mm});
            skLineSegment(sketch, "E668", {"start": v(-29.42, -16.03) * mm, "end": v(-29.49, -16.04) * mm});
            skLineSegment(sketch, "E669", {"start": v(28.96, -16.88) * mm, "end": v(29, -16.93) * mm});
            skLineSegment(sketch, "E670", {"start": v(-46.21, -16.32) * mm, "end": v(-46.19, -16.39) * mm});
            skLineSegment(sketch, "E671", {"start": v(-39.87, -16.88) * mm, "end": v(-39.83, -16.93) * mm});
            skLineSegment(sketch, "E672", {"start": v(9.77, -16.82) * mm, "end": v(9.74, -16.88) * mm});
            skLineSegment(sketch, "E673", {"start": v(-15.41, -13.83) * mm, "end": v(-15.36, -13.87) * mm});
            skLineSegment(sketch, "E674", {"start": v(-0.27, -13.66) * mm, "end": v(-0.29, -13.7) * mm});
            skLineSegment(sketch, "E675", {"start": v(-19.68, -16.17) * mm, "end": v(-19.74, -16.22) * mm});
            skLineSegment(sketch, "E676", {"start": v(-0.22, -15.07) * mm, "end": v(-0.23, -15.14) * mm});
            skLineSegment(sketch, "E677", {"start": v(-45.14, -13.96) * mm, "end": v(-45.2, -13.96) * mm});
            skLineSegment(sketch, "E678", {"start": v(-16.04, -14.88) * mm, "end": v(-16.03, -14.96) * mm});
            skLineSegment(sketch, "E679", {"start": v(-16.11, -16.26) * mm, "end": v(-16.08, -16.32) * mm});
            skLineSegment(sketch, "E680", {"start": v(-3.1, -16.27) * mm, "end": v(-3.07, -16.33) * mm});
            skLineSegment(sketch, "E681", {"start": v(-26.09, -14.88) * mm, "end": v(-26.08, -14.96) * mm});
            skLineSegment(sketch, "E682", {"start": v(-46.17, -13.3) * mm, "end": v(-46.16, -13.38) * mm});
            skLineSegment(sketch, "E683", {"start": v(39.17, -12.97) * mm, "end": v(39.1, -13.01) * mm});
            skLineSegment(sketch, "E684", {"start": v(-47.1, -16.28) * mm, "end": v(-47.14, -16.34) * mm});
            skLineSegment(sketch, "E685", {"start": v(-26.16, -16.26) * mm, "end": v(-26.13, -16.32) * mm});
            skLineSegment(sketch, "E686", {"start": v(49.02, -14.76) * mm, "end": v(49, -14.82) * mm});
            skLineSegment(sketch, "E687", {"start": v(-49.81, -16.17) * mm, "end": v(-49.87, -16.22) * mm});
            skLineSegment(sketch, "E688", {"start": v(-38.98, -16.82) * mm, "end": v(-39.01, -16.88) * mm});
            skLineSegment(sketch, "E689", {"start": v(-16.37, -16.05) * mm, "end": v(-16.3, -16.08) * mm});
            skLineSegment(sketch, "E690", {"start": v(-1.2, -13.66) * mm, "end": v(-1.17, -13.72) * mm});
            skLineSegment(sketch, "E691", {"start": v(49.26, -13.9) * mm, "end": v(49.32, -13.94) * mm});
            skLineSegment(sketch, "E692", {"start": v(20.88, -14.45) * mm, "end": v(20.95, -14.46) * mm});
            skLineSegment(sketch, "E693", {"start": v(-0.28, -14.72) * mm, "end": v(-0.25, -14.78) * mm});
            skLineSegment(sketch, "E694", {"start": v(19.32, -13.96) * mm, "end": v(19.39, -13.96) * mm});
            skLineSegment(sketch, "E695", {"start": v(-16.98, -16.28) * mm, "end": v(-17.01, -16.34) * mm});
            skLineSegment(sketch, "E696", {"start": v(19.8, -16.3) * mm, "end": v(19.83, -16.36) * mm});
            skLineSegment(sketch, "E697", {"start": v(-26.87, -14.54) * mm, "end": v(-26.92, -14.59) * mm});
            skLineSegment(sketch, "E698", {"start": v(-29.42, -16.03) * mm, "end": v(-29.35, -16.03) * mm});
            skLineSegment(sketch, "E699", {"start": v(49.78, -16.11) * mm, "end": v(49.83, -16.16) * mm});
            skLineSegment(sketch, "E700", {"start": v(-27.02, -16.28) * mm, "end": v(-27.06, -16.34) * mm});
            skLineSegment(sketch, "E701", {"start": v(49.92, -14.69) * mm, "end": v(49.94, -14.72) * mm});
            skLineSegment(sketch, "E702", {"start": v(26.08, -16.62) * mm, "end": v(26.08, -16.69) * mm});
            skLineSegment(sketch, "E703", {"start": v(9.74, -16.88) * mm, "end": v(9.7, -16.93) * mm});
            skLineSegment(sketch, "E704", {"start": v(-36.45, -12.9) * mm, "end": v(-36.4, -12.93) * mm});
            skLineSegment(sketch, "E705", {"start": v(-0.29, -13.7) * mm, "end": v(-0.32, -13.75) * mm});
            skLineSegment(sketch, "E706", {"start": v(6.68, -16.06) * mm, "end": v(6.74, -16.08) * mm});
            skLineSegment(sketch, "E707", {"start": v(19.52, -15.52) * mm, "end": v(19.46, -15.53) * mm});
            skLineSegment(sketch, "E708", {"start": v(-19.37, -16.03) * mm, "end": v(-19.3, -16.03) * mm});
            skLineSegment(sketch, "E709", {"start": v(8.97, -13.83) * mm, "end": v(9.03, -13.87) * mm});
            skLineSegment(sketch, "E710", {"start": v(20.81, -14.45) * mm, "end": v(20.74, -14.46) * mm});
            skLineSegment(sketch, "E711", {"start": v(49.68, -13.92) * mm, "end": v(49.65, -13.94) * mm});
            skLineSegment(sketch, "E712", {"start": v(-25.45, -13.83) * mm, "end": v(-25.4, -13.87) * mm});
            skLineSegment(sketch, "E713", {"start": v(-27.06, -15.24) * mm, "end": v(-27.02, -15.3) * mm});
            skLineSegment(sketch, "E714", {"start": v(-16.04, -16.68) * mm, "end": v(-16.06, -16.75) * mm});
            skLineSegment(sketch, "E715", {"start": v(20.81, -14.45) * mm, "end": v(20.88, -14.45) * mm});
            skLineSegment(sketch, "E716", {"start": v(18.92, -16.28) * mm, "end": v(18.89, -16.34) * mm});
            skLineSegment(sketch, "E717", {"start": v(-26.25, -14.58) * mm, "end": v(-26.2, -14.63) * mm});
            skLineSegment(sketch, "E718", {"start": v(16.22, -16.17) * mm, "end": v(16.17, -16.22) * mm});
            skLineSegment(sketch, "E719", {"start": v(-29.57, -17.1) * mm, "end": v(-29.5, -17.11) * mm});
            skLineSegment(sketch, "E720", {"start": v(27.06, -16.33) * mm, "end": v(27.08, -16.39) * mm});
            skLineSegment(sketch, "E721", {"start": v(-47.2, -16.61) * mm, "end": v(-47.19, -16.68) * mm});
            skLineSegment(sketch, "E722", {"start": v(-49.76, -16.12) * mm, "end": v(-49.81, -16.17) * mm});
            skLineSegment(sketch, "E723", {"start": v(49.21, -16.12) * mm, "end": v(49.15, -16.16) * mm});
            skLineSegment(sketch, "E724", {"start": v(8.84, -16.82) * mm, "end": v(8.88, -16.88) * mm});
            skLineSegment(sketch, "E725", {"start": v(-39.22, -17.07) * mm, "end": v(-39.28, -17.1) * mm});
            skLineSegment(sketch, "E726", {"start": v(46.6, -16.04) * mm, "end": v(46.53, -16.06) * mm});
            skLineSegment(sketch, "E727", {"start": v(-19, -16.16) * mm, "end": v(-18.96, -16.2) * mm});
            skLineSegment(sketch, "E728", {"start": v(-14.73, -13.83) * mm, "end": v(-14.79, -13.88) * mm});
            skLineSegment(sketch, "E729", {"start": v(49.15, -15.4) * mm, "end": v(49.2, -15.45) * mm});
            skLineSegment(sketch, "E730", {"start": v(49.05, -13.72) * mm, "end": v(49.1, -13.77) * mm});
            skLineSegment(sketch, "E731", {"start": v(-26.13, -15.24) * mm, "end": v(-26.16, -15.3) * mm});
            skLineSegment(sketch, "E732", {"start": v(-24.6, -13.53) * mm, "end": v(-24.63, -13.6) * mm});
            skLineSegment(sketch, "E733", {"start": v(-25.63, -13.46) * mm, "end": v(-25.62, -13.53) * mm});
            skLineSegment(sketch, "E734", {"start": v(-3.97, -16.28) * mm, "end": v(-4, -16.34) * mm});
            skLineSegment(sketch, "E735", {"start": v(10.95, -15.52) * mm, "end": v(10.89, -15.53) * mm});
            skLineSegment(sketch, "E736", {"start": v(19.02, -16.99) * mm, "end": v(19.07, -17.03) * mm});
            skLineSegment(sketch, "E737", {"start": v(-0.39, -16.16) * mm, "end": v(-0.34, -16.2) * mm});
            skLineSegment(sketch, "E738", {"start": v(-17.05, -14.85) * mm, "end": v(-17.06, -14.92) * mm});
            skLineSegment(sketch, "E739", {"start": v(17.05, -16.46) * mm, "end": v(17.06, -16.53) * mm});
            skLineSegment(sketch, "E740", {"start": v(-27.1, -14.85) * mm, "end": v(-27.1, -14.92) * mm});
            skLineSegment(sketch, "E741", {"start": v(36.6, -17.12) * mm, "end": v(36.66, -17.12) * mm});
            skLineSegment(sketch, "E742", {"start": v(-46.17, -16.68) * mm, "end": v(-46.19, -16.75) * mm});
            skLineSegment(sketch, "E743", {"start": v(-46.48, -13.92) * mm, "end": v(-46.51, -13.94) * mm});
            skLineSegment(sketch, "E744", {"start": v(-49.14, -16.16) * mm, "end": v(-49.1, -16.2) * mm});
            skLineSegment(sketch, "E745", {"start": v(46.86, -16.06) * mm, "end": v(46.92, -16.08) * mm});
            skLineSegment(sketch, "E746", {"start": v(-16.7, -16.05) * mm, "end": v(-16.76, -16.08) * mm});
            skLineSegment(sketch, "E747", {"start": v(19.58, -15.49) * mm, "end": v(19.52, -15.52) * mm});
            skLineSegment(sketch, "E748", {"start": v(-15.58, -13.53) * mm, "end": v(-15.56, -13.6) * mm});
            skLineSegment(sketch, "E749", {"start": v(-0.4, -15.41) * mm, "end": v(-0.45, -15.45) * mm});
            skLineSegment(sketch, "E750", {"start": v(49.65, -13.94) * mm, "end": v(49.59, -13.95) * mm});
            skLineSegment(sketch, "E751", {"start": v(20.56, -14.54) * mm, "end": v(20.5, -14.59) * mm});
            skLineSegment(sketch, "E752", {"start": v(18.83, -16.61) * mm, "end": v(18.84, -16.68) * mm});
            skLineSegment(sketch, "E753", {"start": v(39.42, -12.88) * mm, "end": v(39.35, -12.89) * mm});
            skLineSegment(sketch, "E754", {"start": v(-1.24, -16.47) * mm, "end": v(-1.25, -16.54) * mm});
            skLineSegment(sketch, "E755", {"start": v(29.9, -16.46) * mm, "end": v(29.91, -16.53) * mm});
            skLineSegment(sketch, "E756", {"start": v(16.27, -16.12) * mm, "end": v(16.22, -16.17) * mm});
            skLineSegment(sketch, "E757", {"start": v(26.77, -16.06) * mm, "end": v(26.83, -16.08) * mm});
            skLineSegment(sketch, "E758", {"start": v(-46.84, -13.94) * mm, "end": v(-46.78, -13.95) * mm});
            skLineSegment(sketch, "E759", {"start": v(29.86, -16.82) * mm, "end": v(29.83, -16.88) * mm});
            skLineSegment(sketch, "E760", {"start": v(29.06, -15.4) * mm, "end": v(29.11, -15.45) * mm});
            skLineSegment(sketch, "E761", {"start": v(49.15, -16.16) * mm, "end": v(49.1, -16.22) * mm});
            skLineSegment(sketch, "E762", {"start": v(-36.79, -12.9) * mm, "end": v(-36.85, -12.93) * mm});
            skLineSegment(sketch, "E763", {"start": v(6, -16.65) * mm, "end": v(6, -16.72) * mm});
            skLineSegment(sketch, "E764", {"start": v(19.19, -15.52) * mm, "end": v(19.25, -15.53) * mm});
            skLineSegment(sketch, "E765", {"start": v(31.05, -12.9) * mm, "end": v(31.11, -12.93) * mm});
            skLineSegment(sketch, "E766", {"start": v(21.18, -14.58) * mm, "end": v(21.22, -14.63) * mm});
            skLineSegment(sketch, "E767", {"start": v(31.3, -13.11) * mm, "end": v(31.34, -13.17) * mm});
            skLineSegment(sketch, "E768", {"start": v(-44.86, -13.83) * mm, "end": v(-44.92, -13.88) * mm});
            skLineSegment(sketch, "E769", {"start": v(49.02, -13.66) * mm, "end": v(49.05, -13.72) * mm});
            skLineSegment(sketch, "E770", {"start": v(-24.78, -13.83) * mm, "end": v(-24.83, -13.88) * mm});
            skLineSegment(sketch, "E771", {"start": v(19.87, -16.64) * mm, "end": v(19.85, -16.72) * mm});
            skLineSegment(sketch, "E772", {"start": v(36.3, -16.99) * mm, "end": v(36.35, -17.03) * mm});
            skLineSegment(sketch, "E773", {"start": v(16.9, -16.16) * mm, "end": v(16.94, -16.2) * mm});
            skLineSegment(sketch, "E774", {"start": v(28.93, -16.82) * mm, "end": v(28.96, -16.88) * mm});
            skLineSegment(sketch, "E775", {"start": v(26.16, -16.28) * mm, "end": v(26.13, -16.34) * mm});
            skLineSegment(sketch, "E776", {"start": v(-47.19, -13.31) * mm, "end": v(-47.2, -13.38) * mm});
            skLineSegment(sketch, "E777", {"start": v(49.94, -14.72) * mm, "end": v(49.96, -14.78) * mm});
            skLineSegment(sketch, "E778", {"start": v(7, -16.68) * mm, "end": v(7, -16.75) * mm});
            skLineSegment(sketch, "E779", {"start": v(30.86, -14.45) * mm, "end": v(30.93, -14.45) * mm});
            skLineSegment(sketch, "E780", {"start": v(30.45, -13.12) * mm, "end": v(30.41, -13.18) * mm});
            skLineSegment(sketch, "E781", {"start": v(31.1, -15.49) * mm, "end": v(31.04, -15.52) * mm});
            skLineSegment(sketch, "E782", {"start": v(49.93, -13.7) * mm, "end": v(49.9, -13.75) * mm});
            skLineSegment(sketch, "E783", {"start": v(10.62, -15.52) * mm, "end": v(10.68, -15.53) * mm});
            skLineSegment(sketch, "E784", {"start": v(19.7, -16.99) * mm, "end": v(19.64, -17.03) * mm});
            skLineSegment(sketch, "E785", {"start": v(-29.1, -16.12) * mm, "end": v(-29.05, -16.16) * mm});
            skLineSegment(sketch, "E786", {"start": v(39.42, -12.88) * mm, "end": v(39.5, -12.88) * mm});
            skLineSegment(sketch, "E787", {"start": v(16.05, -16.44) * mm, "end": v(16.04, -16.5) * mm});
            skLineSegment(sketch, "E788", {"start": v(-26.09, -16.46) * mm, "end": v(-26.08, -16.53) * mm});
            skLineSegment(sketch, "E789", {"start": v(49.06, -14.7) * mm, "end": v(49.02, -14.76) * mm});
            skLineSegment(sketch, "E790", {"start": v(1.04, -12.96) * mm, "end": v(1.09, -13) * mm});
            skLineSegment(sketch, "E791", {"start": v(28.89, -15.1) * mm, "end": v(28.9, -15.17) * mm});
            skLineSegment(sketch, "E792", {"start": v(49.47, -16.03) * mm, "end": v(49.54, -16.03) * mm});
            skLineSegment(sketch, "E793", {"start": v(8.8, -16.47) * mm, "end": v(8.8, -16.54) * mm});
            skLineSegment(sketch, "E794", {"start": v(-0.83, -15.53) * mm, "end": v(-0.77, -15.54) * mm});
            skLineSegment(sketch, "E795", {"start": v(30.7, -15.52) * mm, "end": v(30.77, -15.53) * mm});
            skLineSegment(sketch, "E796", {"start": v(6.35, -16.06) * mm, "end": v(6.29, -16.09) * mm});
            skLineSegment(sketch, "E797", {"start": v(49.32, -13.94) * mm, "end": v(49.38, -13.95) * mm});
            skLineSegment(sketch, "E798", {"start": v(9.67, -13.8) * mm, "end": v(9.62, -13.86) * mm});
            skLineSegment(sketch, "E799", {"start": v(-3.7, -16.06) * mm, "end": v(-3.75, -16.09) * mm});
            skLineSegment(sketch, "E800", {"start": v(9.15, -17.1) * mm, "end": v(9.2, -17.11) * mm});
            skLineSegment(sketch, "E801", {"start": v(-0.68, -16.03) * mm, "end": v(-0.62, -16.03) * mm});
            skLineSegment(sketch, "E802", {"start": v(39.79, -13) * mm, "end": v(39.83, -13.06) * mm});
            skLineSegment(sketch, "E803", {"start": v(-36.86, -13.9) * mm, "end": v(-36.8, -13.94) * mm});
            skLineSegment(sketch, "E804", {"start": v(28.89, -16.47) * mm, "end": v(28.88, -16.54) * mm});
            skLineSegment(sketch, "E805", {"start": v(48.97, -15.1) * mm, "end": v(49, -15.17) * mm});
            skLineSegment(sketch, "E806", {"start": v(26.44, -16.06) * mm, "end": v(26.38, -16.09) * mm});
            skLineSegment(sketch, "E807", {"start": v(49.83, -16.16) * mm, "end": v(49.88, -16.2) * mm});
            skLineSegment(sketch, "E808", {"start": v(29.73, -15.41) * mm, "end": v(29.68, -15.45) * mm});
            skLineSegment(sketch, "E809", {"start": v(0.53, -12.93) * mm, "end": v(0.47, -12.97) * mm});
            skLineSegment(sketch, "E810", {"start": v(30.72, -12.9) * mm, "end": v(30.66, -12.93) * mm});
            skLineSegment(sketch, "E811", {"start": v(-27.02, -15.3) * mm, "end": v(-26.98, -15.35) * mm});
            skLineSegment(sketch, "E812", {"start": v(-0.57, -15.52) * mm, "end": v(-0.63, -15.53) * mm});
            skLineSegment(sketch, "E813", {"start": v(36.97, -17) * mm, "end": v(36.92, -17.03) * mm});
            skLineSegment(sketch, "E814", {"start": v(48.97, -16.47) * mm, "end": v(48.96, -16.54) * mm});
            skLineSegment(sketch, "E815", {"start": v(-38.95, -16.75) * mm, "end": v(-38.98, -16.82) * mm});
            skLineSegment(sketch, "E816", {"start": v(-39.95, -16.69) * mm, "end": v(-39.93, -16.75) * mm});
            skLineSegment(sketch, "E817", {"start": v(-16.5, -16.03) * mm, "end": v(-16.43, -16.03) * mm});
            skLineSegment(sketch, "E818", {"start": v(46.53, -16.06) * mm, "end": v(46.46, -16.09) * mm});
            skLineSegment(sketch, "E819", {"start": v(18.83, -15.03) * mm, "end": v(18.84, -15.1) * mm});
            skLineSegment(sketch, "E820", {"start": v(19.75, -16.2) * mm, "end": v(19.79, -16.26) * mm});
            skLineSegment(sketch, "E821", {"start": v(-0.27, -16.82) * mm, "end": v(-0.3, -16.88) * mm});
            skLineSegment(sketch, "E822", {"start": v(-46.25, -16.88) * mm, "end": v(-46.3, -16.93) * mm});
            skLineSegment(sketch, "E823", {"start": v(-47.07, -16.93) * mm, "end": v(-47.02, -16.99) * mm});
            skLineSegment(sketch, "E824", {"start": v(-39.9, -16.82) * mm, "end": v(-39.87, -16.88) * mm});
            skLineSegment(sketch, "E825", {"start": v(-16.63, -16.03) * mm, "end": v(-16.7, -16.05) * mm});
            skLineSegment(sketch, "E826", {"start": v(0.6, -12.9) * mm, "end": v(0.53, -12.93) * mm});
            skLineSegment(sketch, "E827", {"start": v(6.03, -16.79) * mm, "end": v(6.04, -16.82) * mm});
            skLineSegment(sketch, "E828", {"start": v(18.83, -14.96) * mm, "end": v(18.83, -15.03) * mm});
            skLineSegment(sketch, "E829", {"start": v(9.82, -13.45) * mm, "end": v(9.82, -13.53) * mm});
            skLineSegment(sketch, "E830", {"start": v(-24.68, -13.11) * mm, "end": v(-24.65, -13.17) * mm});
            skLineSegment(sketch, "E831", {"start": v(20.34, -14.82) * mm, "end": v(20.33, -14.85) * mm});
            skLineSegment(sketch, "E832", {"start": v(10.45, -15.4) * mm, "end": v(10.5, -15.45) * mm});
            skLineSegment(sketch, "E833", {"start": v(-16.11, -14.69) * mm, "end": v(-16.08, -14.75) * mm});
            skLineSegment(sketch, "E834", {"start": v(19.02, -16.16) * mm, "end": v(18.97, -16.22) * mm});
            skLineSegment(sketch, "E835", {"start": v(-16.43, -16.03) * mm, "end": v(-16.37, -16.05) * mm});
            skLineSegment(sketch, "E836", {"start": v(-0.82, -16.03) * mm, "end": v(-0.88, -16.05) * mm});
            skLineSegment(sketch, "E837", {"start": v(29.17, -17.07) * mm, "end": v(29.23, -17.1) * mm});
            skLineSegment(sketch, "E838", {"start": v(-46.83, -16.05) * mm, "end": v(-46.9, -16.08) * mm});
            skLineSegment(sketch, "E839", {"start": v(-36.33, -13.86) * mm, "end": v(-36.38, -13.9) * mm});
            skLineSegment(sketch, "E840", {"start": v(31.05, -14.48) * mm, "end": v(31.11, -14.5) * mm});
            skLineSegment(sketch, "E841", {"start": v(9.47, -17.1) * mm, "end": v(9.41, -17.11) * mm});
            skLineSegment(sketch, "E842", {"start": v(31.34, -13.17) * mm, "end": v(31.36, -13.23) * mm});
            skLineSegment(sketch, "E843", {"start": v(49.26, -15.49) * mm, "end": v(49.32, -15.52) * mm});
            skLineSegment(sketch, "E844", {"start": v(21.3, -14.75) * mm, "end": v(21.32, -14.81) * mm});
            skLineSegment(sketch, "E845", {"start": v(-26.2, -15.36) * mm, "end": v(-26.26, -15.41) * mm});
            skLineSegment(sketch, "E846", {"start": v(19.79, -16.26) * mm, "end": v(19.8, -16.3) * mm});
            skLineSegment(sketch, "E847", {"start": v(49.96, -16.78) * mm, "end": v(49.95, -16.82) * mm});
            skLineSegment(sketch, "E848", {"start": v(-29.67, -16.12) * mm, "end": v(-29.73, -16.17) * mm});
            skLineSegment(sketch, "E849", {"start": v(29.07, -16.16) * mm, "end": v(29.01, -16.22) * mm});
            skLineSegment(sketch, "E850", {"start": v(30.39, -13.25) * mm, "end": v(30.38, -13.28) * mm});
            skLineSegment(sketch, "E851", {"start": v(-46.3, -16.93) * mm, "end": v(-46.34, -16.99) * mm});
            skLineSegment(sketch, "E852", {"start": v(49.77, -15.45) * mm, "end": v(49.7, -15.49) * mm});
            skLineSegment(sketch, "E853", {"start": v(-16.06, -14.81) * mm, "end": v(-16.04, -14.88) * mm});
            skLineSegment(sketch, "E854", {"start": v(-26.13, -16.32) * mm, "end": v(-26.1, -16.39) * mm});
            skLineSegment(sketch, "E855", {"start": v(48.97, -16.68) * mm, "end": v(49, -16.75) * mm});
            skLineSegment(sketch, "E856", {"start": v(-46.71, -13.96) * mm, "end": v(-46.64, -13.96) * mm});
            skLineSegment(sketch, "E857", {"start": v(-47.11, -16.88) * mm, "end": v(-47.07, -16.93) * mm});
            skLineSegment(sketch, "E858", {"start": v(30.94, -13.96) * mm, "end": v(30.87, -13.96) * mm});
            skLineSegment(sketch, "E859", {"start": v(-36.38, -13.9) * mm, "end": v(-36.44, -13.92) * mm});
            skLineSegment(sketch, "E860", {"start": v(21.32, -14.81) * mm, "end": v(21.34, -14.88) * mm});
            skLineSegment(sketch, "E861", {"start": v(0.35, -13.77) * mm, "end": v(0.4, -13.83) * mm});
            skLineSegment(sketch, "E862", {"start": v(-26.16, -15.3) * mm, "end": v(-26.2, -15.36) * mm});
            skLineSegment(sketch, "E863", {"start": v(-17.01, -14.76) * mm, "end": v(-17.04, -14.82) * mm});
            skLineSegment(sketch, "E864", {"start": v(36.2, -16.88) * mm, "end": v(36.25, -16.93) * mm});
            skLineSegment(sketch, "E865", {"start": v(-27.06, -16.34) * mm, "end": v(-27.08, -16.4) * mm});
            skLineSegment(sketch, "E866", {"start": v(-29.23, -17.1) * mm, "end": v(-29.3, -17.11) * mm});
            skLineSegment(sketch, "E867", {"start": v(-49, -16.39) * mm, "end": v(-48.98, -16.46) * mm});
            skLineSegment(sketch, "E868", {"start": v(47.11, -16.27) * mm, "end": v(47.14, -16.33) * mm});
            skLineSegment(sketch, "E869", {"start": v(6.04, -16.82) * mm, "end": v(6.07, -16.88) * mm});
            skLineSegment(sketch, "E870", {"start": v(-16.77, -15.49) * mm, "end": v(-16.71, -15.52) * mm});
            skLineSegment(sketch, "E871", {"start": v(-1.2, -14.76) * mm, "end": v(-1.23, -14.82) * mm});
            skLineSegment(sketch, "E872", {"start": v(-16.08, -14.75) * mm, "end": v(-16.06, -14.81) * mm});
            skLineSegment(sketch, "E873", {"start": v(20.37, -14.76) * mm, "end": v(20.34, -14.82) * mm});
            skLineSegment(sketch, "E874", {"start": v(49.82, -15.41) * mm, "end": v(49.77, -15.45) * mm});
            skLineSegment(sketch, "E875", {"start": v(37.02, -16.94) * mm, "end": v(36.97, -17) * mm});
            skLineSegment(sketch, "E876", {"start": v(39.4, -13.96) * mm, "end": v(39.48, -13.96) * mm});
            skLineSegment(sketch, "E877", {"start": v(1.14, -13.06) * mm, "end": v(1.18, -13.11) * mm});
            skLineSegment(sketch, "E878", {"start": v(19.47, -12.89) * mm, "end": v(19.53, -12.9) * mm});
            skLineSegment(sketch, "E879", {"start": v(-39.46, -16.03) * mm, "end": v(-39.53, -16.04) * mm});
            skLineSegment(sketch, "E880", {"start": v(36.25, -16.93) * mm, "end": v(36.3, -16.99) * mm});
            skLineSegment(sketch, "E881", {"start": v(49.98, -16.72) * mm, "end": v(49.96, -16.78) * mm});
            skLineSegment(sketch, "E882", {"start": v(-0.26, -16.78) * mm, "end": v(-0.27, -16.82) * mm});
            skLineSegment(sketch, "E883", {"start": v(8.8, -13.46) * mm, "end": v(8.8, -13.53) * mm});
            skLineSegment(sketch, "E884", {"start": v(11.01, -15.49) * mm, "end": v(10.95, -15.52) * mm});
            skLineSegment(sketch, "E885", {"start": v(-17.04, -14.82) * mm, "end": v(-17.05, -14.85) * mm});
            skLineSegment(sketch, "E886", {"start": v(-36.74, -13.95) * mm, "end": v(-36.67, -13.96) * mm});
            skLineSegment(sketch, "E887", {"start": v(29.62, -17.07) * mm, "end": v(29.56, -17.1) * mm});
            skLineSegment(sketch, "E888", {"start": v(-29.16, -16.08) * mm, "end": v(-29.1, -16.12) * mm});
            skLineSegment(sketch, "E889", {"start": v(-27.08, -16.4) * mm, "end": v(-27.1, -16.47) * mm});
            skLineSegment(sketch, "E890", {"start": v(-45.22, -12.88) * mm, "end": v(-45.29, -12.89) * mm});
            skLineSegment(sketch, "E891", {"start": v(-46.51, -13.94) * mm, "end": v(-46.58, -13.95) * mm});
            skLineSegment(sketch, "E892", {"start": v(-26.08, -16.53) * mm, "end": v(-26.08, -16.6) * mm});
            skLineSegment(sketch, "E893", {"start": v(-15.56, -13.6) * mm, "end": v(-15.54, -13.66) * mm});
            skLineSegment(sketch, "E894", {"start": v(-19.87, -16.54) * mm, "end": v(-19.87, -16.62) * mm});
            skLineSegment(sketch, "E895", {"start": v(1.13, -13.78) * mm, "end": v(1.08, -13.83) * mm});
            skLineSegment(sketch, "E896", {"start": v(-24.72, -13.06) * mm, "end": v(-24.68, -13.11) * mm});
            skLineSegment(sketch, "E897", {"start": v(30.41, -13.18) * mm, "end": v(30.39, -13.25) * mm});
            skLineSegment(sketch, "E898", {"start": v(-0.45, -15.45) * mm, "end": v(-0.5, -15.49) * mm});
            skLineSegment(sketch, "E899", {"start": v(-16.15, -14.63) * mm, "end": v(-16.11, -14.69) * mm});
            skLineSegment(sketch, "E900", {"start": v(-29.5, -17.11) * mm, "end": v(-29.44, -17.12) * mm});
            skLineSegment(sketch, "E901", {"start": v(-45.15, -12.88) * mm, "end": v(-45.08, -12.89) * mm});
            skLineSegment(sketch, "E902", {"start": v(37.06, -16.88) * mm, "end": v(37.02, -16.94) * mm});
            skLineSegment(sketch, "E903", {"start": v(16.98, -16.88) * mm, "end": v(16.94, -16.94) * mm});
            skLineSegment(sketch, "E904", {"start": v(26.7, -16.04) * mm, "end": v(26.77, -16.06) * mm});
            skLineSegment(sketch, "E905", {"start": v(-46.9, -16.08) * mm, "end": v(-46.95, -16.12) * mm});
            skLineSegment(sketch, "E906", {"start": v(30.93, -14.45) * mm, "end": v(31, -14.46) * mm});
            skLineSegment(sketch, "E907", {"start": v(-49.97, -16.4) * mm, "end": v(-50, -16.47) * mm});
            skLineSegment(sketch, "E908", {"start": v(-39.96, -16.54) * mm, "end": v(-39.96, -16.62) * mm});
            skLineSegment(sketch, "E909", {"start": v(6.93, -16.88) * mm, "end": v(6.9, -16.94) * mm});
            skLineSegment(sketch, "E910", {"start": v(18.86, -15.17) * mm, "end": v(18.89, -15.24) * mm});
            skLineSegment(sketch, "E911", {"start": v(49.97, -13.23) * mm, "end": v(50, -13.3) * mm});
            skLineSegment(sketch, "E912", {"start": v(-46.19, -16.75) * mm, "end": v(-46.22, -16.82) * mm});
            skLineSegment(sketch, "E913", {"start": v(-29.61, -16.09) * mm, "end": v(-29.67, -16.12) * mm});
            skLineSegment(sketch, "E914", {"start": v(30.8, -13.96) * mm, "end": v(30.87, -13.96) * mm});
            skLineSegment(sketch, "E915", {"start": v(49.54, -16.03) * mm, "end": v(49.6, -16.03) * mm});
            skLineSegment(sketch, "E916", {"start": v(-27.11, -16.54) * mm, "end": v(-27.11, -16.61) * mm});
            skLineSegment(sketch, "E917", {"start": v(26.57, -16.03) * mm, "end": v(26.5, -16.04) * mm});
            skLineSegment(sketch, "E918", {"start": v(6.07, -16.88) * mm, "end": v(6.11, -16.93) * mm});
            skLineSegment(sketch, "E919", {"start": v(30.86, -14.45) * mm, "end": v(30.79, -14.46) * mm});
            skLineSegment(sketch, "E920", {"start": v(29.9, -15.1) * mm, "end": v(29.89, -15.17) * mm});
            skLineSegment(sketch, "E921", {"start": v(0.98, -12.93) * mm, "end": v(1.04, -12.96) * mm});
            skLineSegment(sketch, "E922", {"start": v(19.27, -12.89) * mm, "end": v(19.2, -12.9) * mm});
            skLineSegment(sketch, "E923", {"start": v(-18.84, -16.53) * mm, "end": v(-18.84, -16.6) * mm});
            skLineSegment(sketch, "E924", {"start": v(-1.02, -15.45) * mm, "end": v(-0.96, -15.49) * mm});
            skLineSegment(sketch, "E925", {"start": v(19.66, -13.86) * mm, "end": v(19.6, -13.9) * mm});
            skLineSegment(sketch, "E926", {"start": v(10.56, -15.49) * mm, "end": v(10.62, -15.52) * mm});
            skLineSegment(sketch, "E927", {"start": v(19.14, -16.08) * mm, "end": v(19.08, -16.12) * mm});
            skLineSegment(sketch, "E928", {"start": v(-0.95, -16.08) * mm, "end": v(-1, -16.12) * mm});
            skLineSegment(sketch, "E929", {"start": v(26.64, -16.03) * mm, "end": v(26.7, -16.04) * mm});
            skLineSegment(sketch, "E930", {"start": v(-46.78, -13.95) * mm, "end": v(-46.71, -13.96) * mm});
            skLineSegment(sketch, "E931", {"start": v(-26.1, -16.39) * mm, "end": v(-26.09, -16.46) * mm});
            skLineSegment(sketch, "E932", {"start": v(27.1, -16.6) * mm, "end": v(27.1, -16.68) * mm});
            skLineSegment(sketch, "E933", {"start": v(-46.44, -16.08) * mm, "end": v(-46.38, -16.11) * mm});
            skLineSegment(sketch, "E934", {"start": v(7, -16.75) * mm, "end": v(6.97, -16.82) * mm});
            skLineSegment(sketch, "E935", {"start": v(49.47, -16.03) * mm, "end": v(49.4, -16.03) * mm});
            skLineSegment(sketch, "E936", {"start": v(-36.92, -13.87) * mm, "end": v(-36.86, -13.9) * mm});
            skLineSegment(sketch, "E937", {"start": v(-14.58, -13.6) * mm, "end": v(-14.6, -13.66) * mm});
            skLineSegment(sketch, "E938", {"start": v(21.22, -14.63) * mm, "end": v(21.26, -14.69) * mm});
            skLineSegment(sketch, "E939", {"start": v(-0.25, -14.78) * mm, "end": v(-0.23, -14.85) * mm});
            skLineSegment(sketch, "E940", {"start": v(49.38, -15.53) * mm, "end": v(49.45, -15.54) * mm});
            skLineSegment(sketch, "E941", {"start": v(-26.3, -15.45) * mm, "end": v(-26.37, -15.49) * mm});
            skLineSegment(sketch, "E942", {"start": v(9.82, -13.38) * mm, "end": v(9.82, -13.45) * mm});
            skLineSegment(sketch, "E943", {"start": v(11.18, -15.36) * mm, "end": v(11.13, -15.41) * mm});
            skLineSegment(sketch, "E944", {"start": v(-0.62, -16.03) * mm, "end": v(-0.55, -16.05) * mm});
            skLineSegment(sketch, "E945", {"start": v(-16.93, -14.64) * mm, "end": v(-16.98, -14.7) * mm});
            skLineSegment(sketch, "E946", {"start": v(10.5, -15.45) * mm, "end": v(10.56, -15.49) * mm});
            skLineSegment(sketch, "E947", {"start": v(9.2, -17.11) * mm, "end": v(9.28, -17.12) * mm});
            skLineSegment(sketch, "E948", {"start": v(29.11, -17.03) * mm, "end": v(29.17, -17.07) * mm});
            skLineSegment(sketch, "E949", {"start": v(26.5, -16.04) * mm, "end": v(26.44, -16.06) * mm});
            skLineSegment(sketch, "E950", {"start": v(47.07, -16.2) * mm, "end": v(47.11, -16.27) * mm});
            skLineSegment(sketch, "E951", {"start": v(-46.16, -13.38) * mm, "end": v(-46.16, -13.45) * mm});
            skLineSegment(sketch, "E952", {"start": v(30.79, -14.46) * mm, "end": v(30.72, -14.48) * mm});
            skLineSegment(sketch, "E953", {"start": v(11.18, -14.63) * mm, "end": v(11.22, -14.69) * mm});
            skLineSegment(sketch, "E954", {"start": v(31.11, -14.5) * mm, "end": v(31.17, -14.54) * mm});
            skLineSegment(sketch, "E955", {"start": v(-26.98, -15.35) * mm, "end": v(-26.93, -15.4) * mm});
            skLineSegment(sketch, "E956", {"start": v(-0.63, -15.53) * mm, "end": v(-0.7, -15.54) * mm});
            skLineSegment(sketch, "E957", {"start": v(49, -13.25) * mm, "end": v(48.97, -13.31) * mm});
            skLineSegment(sketch, "E958", {"start": v(19.07, -13.87) * mm, "end": v(19.13, -13.9) * mm});
            skLineSegment(sketch, "E959", {"start": v(29.8, -16.2) * mm, "end": v(29.83, -16.26) * mm});
            skLineSegment(sketch, "E960", {"start": v(36.42, -16.09) * mm, "end": v(36.36, -16.12) * mm});
            skLineSegment(sketch, "E961", {"start": v(-1.23, -16.75) * mm, "end": v(-1.2, -16.82) * mm});
            skLineSegment(sketch, "E962", {"start": v(39.34, -13.95) * mm, "end": v(39.4, -13.96) * mm});
            skLineSegment(sketch, "E963", {"start": v(48.96, -16.54) * mm, "end": v(48.96, -16.61) * mm});
            skLineSegment(sketch, "E964", {"start": v(28.9, -15.17) * mm, "end": v(28.93, -15.24) * mm});
            skLineSegment(sketch, "E965", {"start": v(-36.53, -13.95) * mm, "end": v(-36.6, -13.96) * mm});
            skLineSegment(sketch, "E966", {"start": v(-39.93, -16.75) * mm, "end": v(-39.9, -16.82) * mm});
            skLineSegment(sketch, "E967", {"start": v(6.74, -16.08) * mm, "end": v(6.8, -16.12) * mm});
            skLineSegment(sketch, "E968", {"start": v(19.87, -15) * mm, "end": v(19.87, -15.07) * mm});
            skLineSegment(sketch, "E969", {"start": v(8.8, -13.38) * mm, "end": v(8.8, -13.46) * mm});
            skLineSegment(sketch, "E970", {"start": v(-25.5, -13.07) * mm, "end": v(-25.54, -13.12) * mm});
            skLineSegment(sketch, "E971", {"start": v(11.07, -15.45) * mm, "end": v(11.01, -15.49) * mm});
            skLineSegment(sketch, "E972", {"start": v(-0.22, -16.57) * mm, "end": v(-0.22, -16.64) * mm});
            skLineSegment(sketch, "E973", {"start": v(29.68, -17.03) * mm, "end": v(29.62, -17.07) * mm});
            skLineSegment(sketch, "E974", {"start": v(-46.28, -16.2) * mm, "end": v(-46.24, -16.26) * mm});
            skLineSegment(sketch, "E975", {"start": v(-46.58, -13.95) * mm, "end": v(-46.64, -13.96) * mm});
            skLineSegment(sketch, "E976", {"start": v(30.66, -14.5) * mm, "end": v(30.6, -14.54) * mm});
            skLineSegment(sketch, "E977", {"start": v(-16.89, -15.4) * mm, "end": v(-16.83, -15.45) * mm});
            skLineSegment(sketch, "E978", {"start": v(-16.77, -17.07) * mm, "end": v(-16.71, -17.1) * mm});
            skLineSegment(sketch, "E979", {"start": v(19.85, -15.14) * mm, "end": v(19.83, -15.2) * mm});
            skLineSegment(sketch, "E980", {"start": v(10.4, -15.35) * mm, "end": v(10.45, -15.4) * mm});
            skLineSegment(sketch, "E981", {"start": v(49.2, -15.45) * mm, "end": v(49.26, -15.49) * mm});
            skLineSegment(sketch, "E982", {"start": v(18.97, -16.22) * mm, "end": v(18.92, -16.28) * mm});
            skLineSegment(sketch, "E983", {"start": v(-1.25, -16.54) * mm, "end": v(-1.25, -16.61) * mm});
            skLineSegment(sketch, "E984", {"start": v(36.87, -16.08) * mm, "end": v(36.93, -16.12) * mm});
            skLineSegment(sketch, "E985", {"start": v(50, -16.57) * mm, "end": v(50, -16.64) * mm});
            skLineSegment(sketch, "E986", {"start": v(31, -13.95) * mm, "end": v(30.94, -13.96) * mm});
            skLineSegment(sketch, "E987", {"start": v(31, -14.46) * mm, "end": v(31.05, -14.48) * mm});
            skLineSegment(sketch, "E988", {"start": v(9.41, -17.11) * mm, "end": v(9.35, -17.12) * mm});
            skLineSegment(sketch, "E989", {"start": v(6, -16.72) * mm, "end": v(6.03, -16.79) * mm});
            skLineSegment(sketch, "E990", {"start": v(-16.27, -15.45) * mm, "end": v(-16.32, -15.49) * mm});
            skLineSegment(sketch, "E991", {"start": v(31.36, -13.23) * mm, "end": v(31.38, -13.3) * mm});
            skLineSegment(sketch, "E992", {"start": v(19.25, -13.95) * mm, "end": v(19.32, -13.96) * mm});
            skLineSegment(sketch, "E993", {"start": v(-3.92, -16.22) * mm, "end": v(-3.97, -16.28) * mm});
            skLineSegment(sketch, "E994", {"start": v(-26.43, -17.1) * mm, "end": v(-26.5, -17.11) * mm});
            skLineSegment(sketch, "E995", {"start": v(-26.6, -16.03) * mm, "end": v(-26.68, -16.03) * mm});
            skLineSegment(sketch, "E996", {"start": v(29.01, -16.22) * mm, "end": v(28.97, -16.28) * mm});
            skLineSegment(sketch, "E997", {"start": v(-16.94, -15.35) * mm, "end": v(-16.89, -15.4) * mm});
            skLineSegment(sketch, "E998", {"start": v(39.54, -13.95) * mm, "end": v(39.48, -13.96) * mm});
            skLineSegment(sketch, "E999", {"start": v(-47.2, -13.38) * mm, "end": v(-47.2, -13.46) * mm});
            skLineSegment(sketch, "E1000", {"start": v(-39.26, -16.06) * mm, "end": v(-39.2, -16.08) * mm});
            skLineSegment(sketch, "E1001", {"start": v(-15.5, -13.72) * mm, "end": v(-15.46, -13.77) * mm});
            skLineSegment(sketch, "E1002", {"start": v(-0.32, -13.75) * mm, "end": v(-0.37, -13.8) * mm});
            skLineSegment(sketch, "E1003", {"start": v(-19.86, -16.69) * mm, "end": v(-19.84, -16.75) * mm});
            skLineSegment(sketch, "E1004", {"start": v(-29.28, -16.04) * mm, "end": v(-29.22, -16.06) * mm});
            skLineSegment(sketch, "E1005", {"start": v(-24.82, -12.96) * mm, "end": v(-24.77, -13) * mm});
            skLineSegment(sketch, "E1006", {"start": v(-1.25, -14.96) * mm, "end": v(-1.25, -15.03) * mm});
            skLineSegment(sketch, "E1007", {"start": v(-3.15, -16.2) * mm, "end": v(-3.1, -16.27) * mm});
            skLineSegment(sketch, "E1008", {"start": v(-1.12, -13.77) * mm, "end": v(-1.07, -13.83) * mm});
            skLineSegment(sketch, "E1009", {"start": v(-46.16, -13.45) * mm, "end": v(-46.17, -13.53) * mm});
            skLineSegment(sketch, "E1010", {"start": v(36.14, -16.75) * mm, "end": v(36.17, -16.82) * mm});
            skLineSegment(sketch, "E1011", {"start": v(-26.54, -16.03) * mm, "end": v(-26.47, -16.03) * mm});
            skLineSegment(sketch, "E1012", {"start": v(49, -16.75) * mm, "end": v(49.02, -16.82) * mm});
            skLineSegment(sketch, "E1013", {"start": v(-47, -16.16) * mm, "end": v(-47.06, -16.22) * mm});
            skLineSegment(sketch, "E1014", {"start": v(-44.7, -13.3) * mm, "end": v(-44.69, -13.38) * mm});
            skLineSegment(sketch, "E1015", {"start": v(-0.23, -14.85) * mm, "end": v(-0.22, -14.92) * mm});
            skLineSegment(sketch, "E1016", {"start": v(46.3, -16.22) * mm, "end": v(46.25, -16.28) * mm});
            skLineSegment(sketch, "E1017", {"start": v(0.31, -13.72) * mm, "end": v(0.35, -13.77) * mm});
            skLineSegment(sketch, "E1018", {"start": v(-0.27, -13.17) * mm, "end": v(-0.24, -13.23) * mm});
            skLineSegment(sketch, "E1019", {"start": v(-16.16, -15.36) * mm, "end": v(-16.21, -15.41) * mm});
            skLineSegment(sketch, "E1020", {"start": v(6.29, -16.09) * mm, "end": v(6.23, -16.12) * mm});
            skLineSegment(sketch, "E1021", {"start": v(16.2, -16.99) * mm, "end": v(16.26, -17.03) * mm});
            skLineSegment(sketch, "E1022", {"start": v(-39.32, -16.04) * mm, "end": v(-39.26, -16.06) * mm});
            skLineSegment(sketch, "E1023", {"start": v(-26.98, -14.64) * mm, "end": v(-27.02, -14.7) * mm});
            skLineSegment(sketch, "E1024", {"start": v(-29.49, -16.04) * mm, "end": v(-29.55, -16.06) * mm});
            skLineSegment(sketch, "E1025", {"start": v(30.64, -13.9) * mm, "end": v(30.7, -13.94) * mm});
            skLineSegment(sketch, "E1026", {"start": v(-29.3, -17.11) * mm, "end": v(-29.37, -17.12) * mm});
            skLineSegment(sketch, "E1027", {"start": v(-49.02, -16.33) * mm, "end": v(-49, -16.39) * mm});
            skLineSegment(sketch, "E1028", {"start": v(9.5, -16.05) * mm, "end": v(9.55, -16.08) * mm});
            skLineSegment(sketch, "E1029", {"start": v(-45.72, -13.38) * mm, "end": v(-45.72, -13.46) * mm});
            skLineSegment(sketch, "E1030", {"start": v(-36.58, -12.88) * mm, "end": v(-36.52, -12.89) * mm});
            skLineSegment(sketch, "E1031", {"start": v(-19.26, -17.11) * mm, "end": v(-19.32, -17.12) * mm});
            skLineSegment(sketch, "E1032", {"start": v(6.8, -16.12) * mm, "end": v(6.85, -16.16) * mm});
            skLineSegment(sketch, "E1033", {"start": v(19.34, -12.88) * mm, "end": v(19.27, -12.89) * mm});
            skLineSegment(sketch, "E1034", {"start": v(-16.83, -15.45) * mm, "end": v(-16.77, -15.49) * mm});
            skLineSegment(sketch, "E1035", {"start": v(-1.23, -14.82) * mm, "end": v(-1.24, -14.89) * mm});
            skLineSegment(sketch, "E1036", {"start": v(19.52, -13.94) * mm, "end": v(19.46, -13.95) * mm});
            skLineSegment(sketch, "E1037", {"start": v(-16.03, -16.53) * mm, "end": v(-16.03, -16.6) * mm});
            skLineSegment(sketch, "E1038", {"start": v(-29.44, -17.12) * mm, "end": v(-29.37, -17.12) * mm});
            skLineSegment(sketch, "E1039", {"start": v(39.96, -13.45) * mm, "end": v(39.95, -13.53) * mm});
            skLineSegment(sketch, "E1040", {"start": v(27.1, -16.46) * mm, "end": v(27.1, -16.53) * mm});
            skLineSegment(sketch, "E1041", {"start": v(-47.17, -16.75) * mm, "end": v(-47.15, -16.82) * mm});
            skLineSegment(sketch, "E1042", {"start": v(-37.13, -13.25) * mm, "end": v(-37.15, -13.31) * mm});
            skLineSegment(sketch, "E1043", {"start": v(-49.87, -16.22) * mm, "end": v(-49.91, -16.28) * mm});
            skLineSegment(sketch, "E1044", {"start": v(9.1, -16.08) * mm, "end": v(9.04, -16.12) * mm});
            skLineSegment(sketch, "E1045", {"start": v(46.46, -16.09) * mm, "end": v(46.4, -16.12) * mm});
            skLineSegment(sketch, "E1046", {"start": v(19.4, -12.88) * mm, "end": v(19.47, -12.89) * mm});
            skLineSegment(sketch, "E1047", {"start": v(-39.53, -16.04) * mm, "end": v(-39.6, -16.06) * mm});
            skLineSegment(sketch, "E1048", {"start": v(0.28, -13.66) * mm, "end": v(0.31, -13.72) * mm});
            skLineSegment(sketch, "E1049", {"start": v(-14.64, -13.72) * mm, "end": v(-14.68, -13.78) * mm});
            skLineSegment(sketch, "E1050", {"start": v(-0.23, -16.72) * mm, "end": v(-0.26, -16.78) * mm});
            skLineSegment(sketch, "E1051", {"start": v(16.16, -16.93) * mm, "end": v(16.2, -16.99) * mm});
            skLineSegment(sketch, "E1052", {"start": v(-0.22, -14.92) * mm, "end": v(-0.22, -15) * mm});
            skLineSegment(sketch, "E1053", {"start": v(-3.87, -16.17) * mm, "end": v(-3.92, -16.22) * mm});
            skLineSegment(sketch, "E1054", {"start": v(19.78, -16.88) * mm, "end": v(19.74, -16.93) * mm});
            skLineSegment(sketch, "E1055", {"start": v(-0.5, -16.08) * mm, "end": v(-0.44, -16.11) * mm});
            skLineSegment(sketch, "E1056", {"start": v(26.08, -16.54) * mm, "end": v(26.08, -16.62) * mm});
            skLineSegment(sketch, "E1057", {"start": v(-49.05, -16.27) * mm, "end": v(-49.02, -16.33) * mm});
            skLineSegment(sketch, "E1058", {"start": v(46.97, -16.12) * mm, "end": v(47.02, -16.16) * mm});
            skLineSegment(sketch, "E1059", {"start": v(49.66, -16.05) * mm, "end": v(49.72, -16.08) * mm});
            skLineSegment(sketch, "E1060", {"start": v(9.36, -12.88) * mm, "end": v(9.43, -12.89) * mm});
            skLineSegment(sketch, "E1061", {"start": v(9.8, -13.23) * mm, "end": v(9.82, -13.3) * mm});
            skLineSegment(sketch, "E1062", {"start": v(19.46, -15.53) * mm, "end": v(19.39, -15.54) * mm});
            skLineSegment(sketch, "E1063", {"start": v(1.17, -13.72) * mm, "end": v(1.13, -13.78) * mm});
            skLineSegment(sketch, "E1064", {"start": v(-15.54, -13.66) * mm, "end": v(-15.5, -13.72) * mm});
            skLineSegment(sketch, "E1065", {"start": v(-1.2, -13.18) * mm, "end": v(-1.23, -13.25) * mm});
            skLineSegment(sketch, "E1066", {"start": v(31.38, -15.1) * mm, "end": v(31.36, -15.17) * mm});
            skLineSegment(sketch, "E1067", {"start": v(-26.87, -15.45) * mm, "end": v(-26.82, -15.49) * mm});
            skLineSegment(sketch, "E1068", {"start": v(27.08, -16.39) * mm, "end": v(27.1, -16.46) * mm});
            skLineSegment(sketch, "E1069", {"start": v(20.45, -14.64) * mm, "end": v(20.4, -14.7) * mm});
            skLineSegment(sketch, "E1070", {"start": v(36.3, -16.17) * mm, "end": v(36.25, -16.22) * mm});
            skLineSegment(sketch, "E1071", {"start": v(19.27, -14.46) * mm, "end": v(19.2, -14.48) * mm});
            skLineSegment(sketch, "E1072", {"start": v(29.86, -16.32) * mm, "end": v(29.89, -16.39) * mm});
            skLineSegment(sketch, "E1073", {"start": v(16.94, -16.94) * mm, "end": v(16.89, -17) * mm});
            skLineSegment(sketch, "E1074", {"start": v(-26.16, -14.69) * mm, "end": v(-26.13, -14.75) * mm});
            skLineSegment(sketch, "E1075", {"start": v(-44.69, -13.38) * mm, "end": v(-44.69, -13.45) * mm});
            skLineSegment(sketch, "E1076", {"start": v(-49.95, -16.34) * mm, "end": v(-49.97, -16.4) * mm});
            skLineSegment(sketch, "E1077", {"start": v(28.96, -15.3) * mm, "end": v(29, -15.35) * mm});
            skLineSegment(sketch, "E1078", {"start": v(49.27, -16.08) * mm, "end": v(49.21, -16.12) * mm});
            skLineSegment(sketch, "E1079", {"start": v(19.32, -15.54) * mm, "end": v(19.39, -15.54) * mm});
            skLineSegment(sketch, "E1080", {"start": v(-19.4, -17.12) * mm, "end": v(-19.32, -17.12) * mm});
            skLineSegment(sketch, "E1081", {"start": v(10.4, -14.64) * mm, "end": v(10.36, -14.7) * mm});
            skLineSegment(sketch, "E1082", {"start": v(49.95, -13.17) * mm, "end": v(49.97, -13.23) * mm});
            skLineSegment(sketch, "E1083", {"start": v(8.82, -13.25) * mm, "end": v(8.8, -13.31) * mm});
            skLineSegment(sketch, "E1084", {"start": v(30.74, -13.95) * mm, "end": v(30.8, -13.96) * mm});
            skLineSegment(sketch, "E1085", {"start": v(-17.06, -16.5) * mm, "end": v(-17.07, -16.57) * mm});
            skLineSegment(sketch, "E1086", {"start": v(49.6, -16.03) * mm, "end": v(49.66, -16.05) * mm});
            skLineSegment(sketch, "E1087", {"start": v(49.54, -14.45) * mm, "end": v(49.6, -14.46) * mm});
            skLineSegment(sketch, "E1088", {"start": v(26.1, -16.4) * mm, "end": v(26.08, -16.47) * mm});
            skLineSegment(sketch, "E1089", {"start": v(-46.22, -16.82) * mm, "end": v(-46.25, -16.88) * mm});
            skLineSegment(sketch, "E1090", {"start": v(9.55, -16.08) * mm, "end": v(9.6, -16.11) * mm});
            skLineSegment(sketch, "E1091", {"start": v(29.89, -15.17) * mm, "end": v(29.86, -15.24) * mm});
            skLineSegment(sketch, "E1092", {"start": v(-39.48, -17.12) * mm, "end": v(-39.41, -17.12) * mm});
            skLineSegment(sketch, "E1093", {"start": v(-0.42, -13.86) * mm, "end": v(-0.48, -13.9) * mm});
            skLineSegment(sketch, "E1094", {"start": v(11.22, -14.69) * mm, "end": v(11.25, -14.75) * mm});
            skLineSegment(sketch, "E1095", {"start": v(30.97, -15.53) * mm, "end": v(30.9, -15.54) * mm});
            skLineSegment(sketch, "E1096", {"start": v(19.6, -13.9) * mm, "end": v(19.55, -13.92) * mm});
            skLineSegment(sketch, "E1097", {"start": v(-16.04, -16.46) * mm, "end": v(-16.03, -16.53) * mm});
            skLineSegment(sketch, "E1098", {"start": v(18.92, -16.88) * mm, "end": v(18.96, -16.93) * mm});
            skLineSegment(sketch, "E1099", {"start": v(-29.22, -16.06) * mm, "end": v(-29.16, -16.08) * mm});
            skLineSegment(sketch, "E1100", {"start": v(29, -16.93) * mm, "end": v(29.06, -16.99) * mm});
            skLineSegment(sketch, "E1101", {"start": v(27.1, -16.53) * mm, "end": v(27.1, -16.6) * mm});
            skLineSegment(sketch, "E1102", {"start": v(30.38, -15.14) * mm, "end": v(30.4, -15.2) * mm});
            skLineSegment(sketch, "E1103", {"start": v(49, -14.82) * mm, "end": v(48.97, -14.89) * mm});
            skLineSegment(sketch, "E1104", {"start": v(31.1, -13.91) * mm, "end": v(31.07, -13.92) * mm});
            skLineSegment(sketch, "E1105", {"start": v(28.93, -15.24) * mm, "end": v(28.96, -15.3) * mm});
            skLineSegment(sketch, "E1106", {"start": v(49.4, -16.03) * mm, "end": v(49.33, -16.05) * mm});
            skLineSegment(sketch, "E1107", {"start": v(-18.84, -16.6) * mm, "end": v(-18.85, -16.68) * mm});
            skLineSegment(sketch, "E1108", {"start": v(-1.07, -13.83) * mm, "end": v(-1.02, -13.87) * mm});
            skLineSegment(sketch, "E1109", {"start": v(-0.96, -15.49) * mm, "end": v(-0.9, -15.52) * mm});
            skLineSegment(sketch, "E1110", {"start": v(31.39, -13.38) * mm, "end": v(31.39, -13.45) * mm});
            skLineSegment(sketch, "E1111", {"start": v(29.78, -16.93) * mm, "end": v(29.73, -16.99) * mm});
            skLineSegment(sketch, "E1112", {"start": v(49.92, -13.11) * mm, "end": v(49.95, -13.17) * mm});
            skLineSegment(sketch, "E1113", {"start": v(21.26, -14.69) * mm, "end": v(21.3, -14.75) * mm});
            skLineSegment(sketch, "E1114", {"start": v(-0.55, -16.05) * mm, "end": v(-0.5, -16.08) * mm});
            skLineSegment(sketch, "E1115", {"start": v(39.68, -12.93) * mm, "end": v(39.74, -12.96) * mm});
            skLineSegment(sketch, "E1116", {"start": v(-46.38, -16.11) * mm, "end": v(-46.33, -16.16) * mm});
            skLineSegment(sketch, "E1117", {"start": v(19.82, -16.82) * mm, "end": v(19.78, -16.88) * mm});
            skLineSegment(sketch, "E1118", {"start": v(28.93, -16.34) * mm, "end": v(28.9, -16.4) * mm});
            skLineSegment(sketch, "E1119", {"start": v(-36.13, -13.3) * mm, "end": v(-36.12, -13.38) * mm});
            skLineSegment(sketch, "E1120", {"start": v(-38.93, -16.6) * mm, "end": v(-38.94, -16.68) * mm});
            skLineSegment(sketch, "E1121", {"start": v(49.72, -16.08) * mm, "end": v(49.78, -16.11) * mm});
            skLineSegment(sketch, "E1122", {"start": v(-16.57, -16.03) * mm, "end": v(-16.63, -16.03) * mm});
            skLineSegment(sketch, "E1123", {"start": v(9.28, -17.12) * mm, "end": v(9.35, -17.12) * mm});
            skLineSegment(sketch, "E1124", {"start": v(29.83, -15.3) * mm, "end": v(29.78, -15.36) * mm});
            skLineSegment(sketch, "E1125", {"start": v(0.41, -13.01) * mm, "end": v(0.36, -13.07) * mm});
            skLineSegment(sketch, "E1126", {"start": v(-45.43, -13.9) * mm, "end": v(-45.37, -13.94) * mm});
            skLineSegment(sketch, "E1127", {"start": v(-26.93, -15.4) * mm, "end": v(-26.87, -15.45) * mm});
            skLineSegment(sketch, "E1128", {"start": v(49.02, -13.18) * mm, "end": v(49, -13.25) * mm});
            skLineSegment(sketch, "E1129", {"start": v(-16.71, -17.1) * mm, "end": v(-16.65, -17.11) * mm});
            skLineSegment(sketch, "E1130", {"start": v(-4, -16.82) * mm, "end": v(-3.97, -16.88) * mm});
            skLineSegment(sketch, "E1131", {"start": v(-26.76, -17.1) * mm, "end": v(-26.7, -17.11) * mm});
            skLineSegment(sketch, "E1132", {"start": v(-1.24, -16.68) * mm, "end": v(-1.23, -16.75) * mm});
            skLineSegment(sketch, "E1133", {"start": v(-46.5, -12.9) * mm, "end": v(-46.44, -12.93) * mm});
            skLineSegment(sketch, "E1134", {"start": v(29.83, -16.26) * mm, "end": v(29.86, -16.32) * mm});
            skLineSegment(sketch, "E1135", {"start": v(-47.19, -13.53) * mm, "end": v(-47.17, -13.6) * mm});
            skLineSegment(sketch, "E1136", {"start": v(-36.47, -13.94) * mm, "end": v(-36.53, -13.95) * mm});
            skLineSegment(sketch, "E1137", {"start": v(-36.65, -12.88) * mm, "end": v(-36.72, -12.89) * mm});
            skLineSegment(sketch, "E1138", {"start": v(1.09, -13) * mm, "end": v(1.14, -13.06) * mm});
            skLineSegment(sketch, "E1139", {"start": v(-18.85, -16.68) * mm, "end": v(-18.87, -16.75) * mm});
            skLineSegment(sketch, "E1140", {"start": v(-14.6, -13.66) * mm, "end": v(-14.64, -13.72) * mm});
            skLineSegment(sketch, "E1141", {"start": v(19.13, -13.9) * mm, "end": v(19.19, -13.94) * mm});
            skLineSegment(sketch, "E1142", {"start": v(-0.9, -15.52) * mm, "end": v(-0.83, -15.53) * mm});
            skLineSegment(sketch, "E1143", {"start": v(30.83, -15.54) * mm, "end": v(30.9, -15.54) * mm});
            skLineSegment(sketch, "E1144", {"start": v(19.65, -16.11) * mm, "end": v(19.7, -16.16) * mm});
            skLineSegment(sketch, "E1145", {"start": v(-25.44, -13.01) * mm, "end": v(-25.5, -13.07) * mm});
            skLineSegment(sketch, "E1146", {"start": v(-16.32, -17.07) * mm, "end": v(-16.38, -17.1) * mm});
            skLineSegment(sketch, "E1147", {"start": v(19.53, -14.48) * mm, "end": v(19.6, -14.5) * mm});
            skLineSegment(sketch, "E1148", {"start": v(-0.22, -16.64) * mm, "end": v(-0.23, -16.72) * mm});
            skLineSegment(sketch, "E1149", {"start": v(-16.98, -14.7) * mm, "end": v(-17.01, -14.76) * mm});
            skLineSegment(sketch, "E1150", {"start": v(50, -14.92) * mm, "end": v(50, -15) * mm});
            skLineSegment(sketch, "E1151", {"start": v(-27.02, -14.7) * mm, "end": v(-27.06, -14.76) * mm});
            skLineSegment(sketch, "E1152", {"start": v(-26.37, -17.07) * mm, "end": v(-26.43, -17.1) * mm});
            skLineSegment(sketch, "E1153", {"start": v(36.17, -16.82) * mm, "end": v(36.2, -16.88) * mm});
            skLineSegment(sketch, "E1154", {"start": v(-46.33, -16.16) * mm, "end": v(-46.28, -16.2) * mm});
            skLineSegment(sketch, "E1155", {"start": v(-26.6, -16.03) * mm, "end": v(-26.54, -16.03) * mm});
            skLineSegment(sketch, "E1156", {"start": v(-36.8, -13.94) * mm, "end": v(-36.74, -13.95) * mm});
            skLineSegment(sketch, "E1157", {"start": v(-38.94, -16.68) * mm, "end": v(-38.95, -16.75) * mm});
            skLineSegment(sketch, "E1158", {"start": v(-16.57, -16.03) * mm, "end": v(-16.5, -16.03) * mm});
            skLineSegment(sketch, "E1159", {"start": v(0.47, -12.97) * mm, "end": v(0.41, -13.01) * mm});
            skLineSegment(sketch, "E1160", {"start": v(-19.87, -16.62) * mm, "end": v(-19.86, -16.69) * mm});
            skLineSegment(sketch, "E1161", {"start": v(1.2, -13.66) * mm, "end": v(1.17, -13.72) * mm});
            skLineSegment(sketch, "E1162", {"start": v(20.5, -15.4) * mm, "end": v(20.54, -15.45) * mm});
            skLineSegment(sketch, "E1163", {"start": v(-1.16, -13.12) * mm, "end": v(-1.2, -13.18) * mm});
            skLineSegment(sketch, "E1164", {"start": v(30.36, -13.35) * mm, "end": v(30.36, -13.42) * mm});
            skLineSegment(sketch, "E1165", {"start": v(-45.37, -13.94) * mm, "end": v(-45.34, -13.95) * mm});
            skLineSegment(sketch, "E1166", {"start": v(-0.5, -15.49) * mm, "end": v(-0.57, -15.52) * mm});
            skLineSegment(sketch, "E1167", {"start": v(-3.25, -16.12) * mm, "end": v(-3.2, -16.16) * mm});
            skLineSegment(sketch, "E1168", {"start": v(9.82, -13.3) * mm, "end": v(9.82, -13.38) * mm});
            skLineSegment(sketch, "E1169", {"start": v(-24.77, -13) * mm, "end": v(-24.72, -13.06) * mm});
            skLineSegment(sketch, "E1170", {"start": v(-1.25, -16.61) * mm, "end": v(-1.24, -16.68) * mm});
            skLineSegment(sketch, "E1171", {"start": v(29.06, -16.99) * mm, "end": v(29.11, -17.03) * mm});
            skLineSegment(sketch, "E1172", {"start": v(-0.75, -14.45) * mm, "end": v(-0.68, -14.45) * mm});
            skLineSegment(sketch, "E1173", {"start": v(-47.15, -16.82) * mm, "end": v(-47.11, -16.88) * mm});
            skLineSegment(sketch, "E1174", {"start": v(-46.95, -16.12) * mm, "end": v(-47, -16.16) * mm});
            skLineSegment(sketch, "E1175", {"start": v(-49.91, -16.28) * mm, "end": v(-49.95, -16.34) * mm});
            skLineSegment(sketch, "E1176", {"start": v(-36.44, -13.92) * mm, "end": v(-36.47, -13.94) * mm});
            skLineSegment(sketch, "E1177", {"start": v(9.3, -12.88) * mm, "end": v(9.22, -12.89) * mm});
            skLineSegment(sketch, "E1178", {"start": v(38.93, -13.53) * mm, "end": v(38.95, -13.6) * mm});
            skLineSegment(sketch, "E1179", {"start": v(-36.65, -12.88) * mm, "end": v(-36.58, -12.88) * mm});
            skLineSegment(sketch, "E1180", {"start": v(-39.96, -16.62) * mm, "end": v(-39.95, -16.69) * mm});
            skLineSegment(sketch, "E1181", {"start": v(-16.21, -15.41) * mm, "end": v(-16.27, -15.45) * mm});
            skLineSegment(sketch, "E1182", {"start": v(31.38, -13.3) * mm, "end": v(31.39, -13.38) * mm});
            skLineSegment(sketch, "E1183", {"start": v(6.17, -16.17) * mm, "end": v(6.12, -16.22) * mm});
            skLineSegment(sketch, "E1184", {"start": v(18.84, -15.1) * mm, "end": v(18.86, -15.17) * mm});
            skLineSegment(sketch, "E1185", {"start": v(19.19, -13.94) * mm, "end": v(19.25, -13.95) * mm});
            skLineSegment(sketch, "E1186", {"start": v(-45, -13.92) * mm, "end": v(-45.07, -13.95) * mm});
            skLineSegment(sketch, "E1187", {"start": v(36.93, -16.12) * mm, "end": v(36.98, -16.16) * mm});
            skLineSegment(sketch, "E1188", {"start": v(9.47, -13.94) * mm, "end": v(9.41, -13.95) * mm});
            skLineSegment(sketch, "E1189", {"start": v(-24.65, -13.66) * mm, "end": v(-24.68, -13.72) * mm});
            skLineSegment(sketch, "E1190", {"start": v(-25.39, -12.97) * mm, "end": v(-25.44, -13.01) * mm});
            skLineSegment(sketch, "E1191", {"start": v(-17.05, -16.43) * mm, "end": v(-17.06, -16.5) * mm});
            skLineSegment(sketch, "E1192", {"start": v(19.7, -16.16) * mm, "end": v(19.75, -16.2) * mm});
            skLineSegment(sketch, "E1193", {"start": v(39.62, -12.9) * mm, "end": v(39.68, -12.93) * mm});
            skLineSegment(sketch, "E1194", {"start": v(-29.55, -16.06) * mm, "end": v(-29.61, -16.09) * mm});
            skLineSegment(sketch, "E1195", {"start": v(-27.1, -16.47) * mm, "end": v(-27.11, -16.54) * mm});
            skLineSegment(sketch, "E1196", {"start": v(49.98, -14.85) * mm, "end": v(50, -14.92) * mm});
            skLineSegment(sketch, "E1197", {"start": v(-46.17, -13.53) * mm, "end": v(-46.19, -13.6) * mm});
            skLineSegment(sketch, "E1198", {"start": v(30.7, -13.94) * mm, "end": v(30.74, -13.95) * mm});
            skLineSegment(sketch, "E1199", {"start": v(-45.22, -12.88) * mm, "end": v(-45.15, -12.88) * mm});
            skLineSegment(sketch, "E1200", {"start": v(-47.2, -13.46) * mm, "end": v(-47.19, -13.53) * mm});
            skLineSegment(sketch, "E1201", {"start": v(9.82, -16.64) * mm, "end": v(9.8, -16.72) * mm});
            skLineSegment(sketch, "E1202", {"start": v(-0.37, -13.8) * mm, "end": v(-0.42, -13.86) * mm});
            skLineSegment(sketch, "E1203", {"start": v(19.34, -12.88) * mm, "end": v(19.4, -12.88) * mm});
            skLineSegment(sketch, "E1204", {"start": v(6.85, -16.16) * mm, "end": v(6.9, -16.2) * mm});
            skLineSegment(sketch, "E1205", {"start": v(30.86, -12.88) * mm, "end": v(30.79, -12.89) * mm});
            skLineSegment(sketch, "E1206", {"start": v(19.87, -15.07) * mm, "end": v(19.85, -15.14) * mm});
            skLineSegment(sketch, "E1207", {"start": v(-1.24, -14.89) * mm, "end": v(-1.25, -14.96) * mm});
            skLineSegment(sketch, "E1208", {"start": v(9.15, -13.94) * mm, "end": v(9.2, -13.95) * mm});
            skLineSegment(sketch, "E1209", {"start": v(20.4, -14.7) * mm, "end": v(20.37, -14.76) * mm});
            skLineSegment(sketch, "E1210", {"start": v(19.55, -13.92) * mm, "end": v(19.52, -13.94) * mm});
            skLineSegment(sketch, "E1211", {"start": v(-3.2, -16.16) * mm, "end": v(-3.15, -16.2) * mm});
            skLineSegment(sketch, "E1212", {"start": v(49.65, -15.52) * mm, "end": v(49.59, -15.53) * mm});
            skLineSegment(sketch, "E1213", {"start": v(18.89, -16.82) * mm, "end": v(18.92, -16.88) * mm});
            skLineSegment(sketch, "E1214", {"start": v(19.08, -16.12) * mm, "end": v(19.02, -16.16) * mm});
            skLineSegment(sketch, "E1215", {"start": v(-0.88, -16.05) * mm, "end": v(-0.95, -16.08) * mm});
            skLineSegment(sketch, "E1216", {"start": v(16.12, -16.28) * mm, "end": v(16.09, -16.34) * mm});
            skLineSegment(sketch, "E1217", {"start": v(49.47, -14.45) * mm, "end": v(49.4, -14.46) * mm});
            skLineSegment(sketch, "E1218", {"start": v(-37.15, -13.31) * mm, "end": v(-37.15, -13.38) * mm});
            skLineSegment(sketch, "E1219", {"start": v(31.07, -13.92) * mm, "end": v(31, -13.95) * mm});
            skLineSegment(sketch, "E1220", {"start": v(9.3, -12.88) * mm, "end": v(9.36, -12.88) * mm});
            skLineSegment(sketch, "E1221", {"start": v(8.8, -16.61) * mm, "end": v(8.8, -16.68) * mm});
            skLineSegment(sketch, "E1222", {"start": v(46.35, -16.17) * mm, "end": v(46.3, -16.22) * mm});
            skLineSegment(sketch, "E1223", {"start": v(6.97, -16.82) * mm, "end": v(6.93, -16.88) * mm});
            skLineSegment(sketch, "E1224", {"start": v(-39.6, -16.06) * mm, "end": v(-39.66, -16.09) * mm});
            skLineSegment(sketch, "E1225", {"start": v(30.36, -15.07) * mm, "end": v(30.38, -15.14) * mm});
            skLineSegment(sketch, "E1226", {"start": v(10.36, -14.7) * mm, "end": v(10.33, -14.76) * mm});
            skLineSegment(sketch, "E1227", {"start": v(6.23, -16.12) * mm, "end": v(6.17, -16.17) * mm});
            skLineSegment(sketch, "E1228", {"start": v(-26.26, -15.41) * mm, "end": v(-26.3, -15.45) * mm});
            skLineSegment(sketch, "E1229", {"start": v(49.32, -15.52) * mm, "end": v(49.38, -15.53) * mm});
            skLineSegment(sketch, "E1230", {"start": v(9.5, -13.92) * mm, "end": v(9.47, -13.94) * mm});
            skLineSegment(sketch, "E1231", {"start": v(36.98, -16.16) * mm, "end": v(37.03, -16.2) * mm});
            skLineSegment(sketch, "E1232", {"start": v(-3.08, -16.82) * mm, "end": v(-3.1, -16.88) * mm});
            skLineSegment(sketch, "E1233", {"start": v(-3.81, -16.12) * mm, "end": v(-3.87, -16.17) * mm});
            skLineSegment(sketch, "E1234", {"start": v(50, -16.64) * mm, "end": v(49.98, -16.72) * mm});
            skLineSegment(sketch, "E1235", {"start": v(28.97, -16.28) * mm, "end": v(28.93, -16.34) * mm});
            skLineSegment(sketch, "E1236", {"start": v(26.57, -16.03) * mm, "end": v(26.64, -16.03) * mm});
            skLineSegment(sketch, "E1237", {"start": v(-46.83, -12.9) * mm, "end": v(-46.9, -12.93) * mm});
            skLineSegment(sketch, "E1238", {"start": v(38.92, -13.46) * mm, "end": v(38.93, -13.53) * mm});
            skLineSegment(sketch, "E1239", {"start": v(-45.7, -13.31) * mm, "end": v(-45.72, -13.38) * mm});
            skLineSegment(sketch, "E1240", {"start": v(-14.68, -13.06) * mm, "end": v(-14.64, -13.11) * mm});
            skLineSegment(sketch, "E1241", {"start": v(47.02, -16.16) * mm, "end": v(47.07, -16.2) * mm});
            skLineSegment(sketch, "E1242", {"start": v(29.86, -15.24) * mm, "end": v(29.83, -15.3) * mm});
            skLineSegment(sketch, "E1243", {"start": v(30.86, -12.88) * mm, "end": v(30.93, -12.88) * mm});
            skLineSegment(sketch, "E1244", {"start": v(31.39, -15.03) * mm, "end": v(31.38, -15.1) * mm});
            skLineSegment(sketch, "E1245", {"start": v(49.06, -13.12) * mm, "end": v(49.02, -13.18) * mm});
            skLineSegment(sketch, "E1246", {"start": v(49.7, -15.49) * mm, "end": v(49.65, -15.52) * mm});
            skLineSegment(sketch, "E1247", {"start": v(-28.88, -16.6) * mm, "end": v(-28.9, -16.68) * mm});
            skLineSegment(sketch, "E1248", {"start": v(36.36, -16.12) * mm, "end": v(36.3, -16.17) * mm});
            skLineSegment(sketch, "E1249", {"start": v(-26.93, -16.99) * mm, "end": v(-26.87, -17.03) * mm});
            skLineSegment(sketch, "E1250", {"start": v(19.2, -14.48) * mm, "end": v(19.14, -14.5) * mm});
            skLineSegment(sketch, "E1251", {"start": v(37.1, -16.82) * mm, "end": v(37.06, -16.88) * mm});
            skLineSegment(sketch, "E1252", {"start": v(16.89, -17) * mm, "end": v(16.83, -17.03) * mm});
            skLineSegment(sketch, "E1253", {"start": v(48.96, -16.61) * mm, "end": v(48.97, -16.68) * mm});
            skLineSegment(sketch, "E1254", {"start": v(49.47, -14.45) * mm, "end": v(49.54, -14.45) * mm});
            skLineSegment(sketch, "E1255", {"start": v(-49.15, -17) * mm, "end": v(-49.2, -17.03) * mm});
            skLineSegment(sketch, "E1256", {"start": v(9.16, -16.05) * mm, "end": v(9.1, -16.08) * mm});
            skLineSegment(sketch, "E1257", {"start": v(46.4, -16.12) * mm, "end": v(46.35, -16.17) * mm});
            skLineSegment(sketch, "E1258", {"start": v(-15.4, -13.01) * mm, "end": v(-15.45, -13.07) * mm});
            skLineSegment(sketch, "E1259", {"start": v(21.17, -15.41) * mm, "end": v(21.12, -15.45) * mm});
            skLineSegment(sketch, "E1260", {"start": v(8.8, -13.31) * mm, "end": v(8.8, -13.38) * mm});
            skLineSegment(sketch, "E1261", {"start": v(11.13, -15.41) * mm, "end": v(11.07, -15.45) * mm});
            skLineSegment(sketch, "E1262", {"start": v(-49.83, -16.99) * mm, "end": v(-49.77, -17.03) * mm});
            skLineSegment(sketch, "E1263", {"start": v(-16.57, -14.45) * mm, "end": v(-16.5, -14.45) * mm});
            skLineSegment(sketch, "E1264", {"start": v(-29.91, -16.54) * mm, "end": v(-29.91, -16.62) * mm});
            skLineSegment(sketch, "E1265", {"start": v(29.73, -16.99) * mm, "end": v(29.68, -17.03) * mm});
            skLineSegment(sketch, "E1266", {"start": v(-36.12, -13.45) * mm, "end": v(-36.13, -13.53) * mm});
            skLineSegment(sketch, "E1267", {"start": v(-26.98, -16.93) * mm, "end": v(-26.93, -16.99) * mm});
            skLineSegment(sketch, "E1268", {"start": v(26.08, -16.47) * mm, "end": v(26.08, -16.54) * mm});
            skLineSegment(sketch, "E1269", {"start": v(30.72, -14.48) * mm, "end": v(30.66, -14.5) * mm});
            skLineSegment(sketch, "E1270", {"start": v(-39.05, -16.2) * mm, "end": v(-39, -16.27) * mm});
            skLineSegment(sketch, "E1271", {"start": v(-18.97, -16.94) * mm, "end": v(-19.02, -17) * mm});
            skLineSegment(sketch, "E1272", {"start": v(-25.06, -12.88) * mm, "end": v(-25, -12.89) * mm});
            skLineSegment(sketch, "E1273", {"start": v(-1.06, -13.01) * mm, "end": v(-1.12, -13.07) * mm});
            skLineSegment(sketch, "E1274", {"start": v(30.38, -13.28) * mm, "end": v(30.36, -13.35) * mm});
            skLineSegment(sketch, "E1275", {"start": v(49.85, -13.8) * mm, "end": v(49.8, -13.86) * mm});
            skLineSegment(sketch, "E1276", {"start": v(-16.5, -14.45) * mm, "end": v(-16.43, -14.46) * mm});
            skLineSegment(sketch, "E1277", {"start": v(18.84, -13.31) * mm, "end": v(18.83, -13.38) * mm});
            skLineSegment(sketch, "E1278", {"start": v(-16.58, -17.12) * mm, "end": v(-16.51, -17.12) * mm});
            skLineSegment(sketch, "E1279", {"start": v(39.29, -12.9) * mm, "end": v(39.23, -12.93) * mm});
            skLineSegment(sketch, "E1280", {"start": v(-46.63, -12.88) * mm, "end": v(-46.56, -12.89) * mm});
            skLineSegment(sketch, "E1281", {"start": v(48.97, -14.89) * mm, "end": v(48.96, -14.96) * mm});
            skLineSegment(sketch, "E1282", {"start": v(49.33, -16.05) * mm, "end": v(49.27, -16.08) * mm});
            skLineSegment(sketch, "E1283", {"start": v(1.26, -13.45) * mm, "end": v(1.25, -13.53) * mm});
            skLineSegment(sketch, "E1284", {"start": v(19.86, -13.3) * mm, "end": v(19.87, -13.38) * mm});
            skLineSegment(sketch, "E1285", {"start": v(19.65, -14.54) * mm, "end": v(19.7, -14.58) * mm});
            skLineSegment(sketch, "E1286", {"start": v(20.4, -15.3) * mm, "end": v(20.44, -15.35) * mm});
            skLineSegment(sketch, "E1287", {"start": v(-25.13, -12.88) * mm, "end": v(-25.06, -12.88) * mm});
            skLineSegment(sketch, "E1288", {"start": v(16.44, -17.11) * mm, "end": v(16.5, -17.12) * mm});
            skLineSegment(sketch, "E1289", {"start": v(-14.73, -13) * mm, "end": v(-14.68, -13.06) * mm});
            skLineSegment(sketch, "E1290", {"start": v(30.44, -13.72) * mm, "end": v(30.49, -13.77) * mm});
            skLineSegment(sketch, "E1291", {"start": v(6.46, -17.12) * mm, "end": v(6.53, -17.12) * mm});
            skLineSegment(sketch, "E1292", {"start": v(0.23, -13.35) * mm, "end": v(0.23, -13.42) * mm});
            skLineSegment(sketch, "E1293", {"start": v(-28.9, -16.68) * mm, "end": v(-28.9, -16.75) * mm});
            skLineSegment(sketch, "E1294", {"start": v(26.48, -17.11) * mm, "end": v(26.55, -17.12) * mm});
            skLineSegment(sketch, "E1295", {"start": v(-36.13, -13.53) * mm, "end": v(-36.15, -13.6) * mm});
            skLineSegment(sketch, "E1296", {"start": v(29.7, -14.54) * mm, "end": v(29.74, -14.58) * mm});
            skLineSegment(sketch, "E1297", {"start": v(1.26, -13.38) * mm, "end": v(1.26, -13.45) * mm});
            skLineSegment(sketch, "E1298", {"start": v(31.38, -14.88) * mm, "end": v(31.39, -14.96) * mm});
            skLineSegment(sketch, "E1299", {"start": v(-0.3, -13.11) * mm, "end": v(-0.27, -13.17) * mm});
            skLineSegment(sketch, "E1300", {"start": v(-15.34, -12.97) * mm, "end": v(-15.4, -13.01) * mm});
            skLineSegment(sketch, "E1301", {"start": v(10.28, -14.92) * mm, "end": v(10.27, -15) * mm});
            skLineSegment(sketch, "E1302", {"start": v(26.76, -17.1) * mm, "end": v(26.7, -17.11) * mm});
            skLineSegment(sketch, "E1303", {"start": v(-0.77, -17.12) * mm, "end": v(-0.7, -17.12) * mm});
            skLineSegment(sketch, "E1304", {"start": v(-29.91, -16.62) * mm, "end": v(-29.9, -16.69) * mm});
            skLineSegment(sketch, "E1305", {"start": v(-46.76, -12.89) * mm, "end": v(-46.83, -12.9) * mm});
            skLineSegment(sketch, "E1306", {"start": v(9.6, -12.96) * mm, "end": v(9.66, -13) * mm});
            skLineSegment(sketch, "E1307", {"start": v(39.9, -13.66) * mm, "end": v(39.89, -13.7) * mm});
            skLineSegment(sketch, "E1308", {"start": v(-19.64, -17.03) * mm, "end": v(-19.58, -17.07) * mm});
            skLineSegment(sketch, "E1309", {"start": v(-14.78, -12.96) * mm, "end": v(-14.73, -13) * mm});
            skLineSegment(sketch, "E1310", {"start": v(0.23, -13.42) * mm, "end": v(0.23, -13.5) * mm});
            skLineSegment(sketch, "E1311", {"start": v(29.18, -14.5) * mm, "end": v(29.12, -14.54) * mm});
            skLineSegment(sketch, "E1312", {"start": v(30.39, -14.82) * mm, "end": v(30.38, -14.85) * mm});
            skLineSegment(sketch, "E1313", {"start": v(-26.63, -15.54) * mm, "end": v(-26.56, -15.54) * mm});
            skLineSegment(sketch, "E1314", {"start": v(19.02, -14.59) * mm, "end": v(18.97, -14.64) * mm});
            skLineSegment(sketch, "E1315", {"start": v(21.22, -15.36) * mm, "end": v(21.17, -15.41) * mm});
            skLineSegment(sketch, "E1316", {"start": v(-3.97, -16.88) * mm, "end": v(-3.93, -16.93) * mm});
            skLineSegment(sketch, "E1317", {"start": v(49.27, -12.93) * mm, "end": v(49.21, -12.97) * mm});
            skLineSegment(sketch, "E1318", {"start": v(36.15, -16.4) * mm, "end": v(36.13, -16.47) * mm});
            skLineSegment(sketch, "E1319", {"start": v(-26.82, -17.07) * mm, "end": v(-26.76, -17.1) * mm});
            skLineSegment(sketch, "E1320", {"start": v(39, -13.72) * mm, "end": v(39.05, -13.77) * mm});
            skLineSegment(sketch, "E1321", {"start": v(49.65, -17.1) * mm, "end": v(49.59, -17.11) * mm});
            skLineSegment(sketch, "E1322", {"start": v(-37.15, -13.46) * mm, "end": v(-37.15, -13.53) * mm});
            skLineSegment(sketch, "E1323", {"start": v(38.97, -13.66) * mm, "end": v(39, -13.72) * mm});
            skLineSegment(sketch, "E1324", {"start": v(8.98, -13.01) * mm, "end": v(8.93, -13.07) * mm});
            skLineSegment(sketch, "E1325", {"start": v(47.14, -16.82) * mm, "end": v(47.1, -16.88) * mm});
            skLineSegment(sketch, "E1326", {"start": v(49.78, -12.96) * mm, "end": v(49.83, -13) * mm});
            skLineSegment(sketch, "E1327", {"start": v(-3.15, -16.94) * mm, "end": v(-3.2, -17) * mm});
            skLineSegment(sketch, "E1328", {"start": v(9.66, -13) * mm, "end": v(9.7, -13.06) * mm});
            skLineSegment(sketch, "E1329", {"start": v(16.5, -17.12) * mm, "end": v(16.58, -17.12) * mm});
            skLineSegment(sketch, "E1330", {"start": v(-16.38, -17.1) * mm, "end": v(-16.45, -17.11) * mm});
            skLineSegment(sketch, "E1331", {"start": v(-29.9, -16.69) * mm, "end": v(-29.89, -16.75) * mm});
            skLineSegment(sketch, "E1332", {"start": v(-3.93, -16.93) * mm, "end": v(-3.88, -16.99) * mm});
            skLineSegment(sketch, "E1333", {"start": v(26.42, -17.1) * mm, "end": v(26.48, -17.11) * mm});
            skLineSegment(sketch, "E1334", {"start": v(19.08, -14.54) * mm, "end": v(19.02, -14.59) * mm});
            skLineSegment(sketch, "E1335", {"start": v(-16.65, -17.11) * mm, "end": v(-16.58, -17.12) * mm});
            skLineSegment(sketch, "E1336", {"start": v(21.26, -15.3) * mm, "end": v(21.22, -15.36) * mm});
            skLineSegment(sketch, "E1337", {"start": v(-0.75, -14.45) * mm, "end": v(-0.82, -14.46) * mm});
            skLineSegment(sketch, "E1338", {"start": v(29.74, -14.58) * mm, "end": v(29.8, -14.63) * mm});
            skLineSegment(sketch, "E1339", {"start": v(9.04, -12.97) * mm, "end": v(8.98, -13.01) * mm});
            skLineSegment(sketch, "E1340", {"start": v(-0.44, -12.96) * mm, "end": v(-0.39, -13) * mm});
            skLineSegment(sketch, "E1341", {"start": v(-15.29, -12.93) * mm, "end": v(-15.34, -12.97) * mm});
            skLineSegment(sketch, "E1342", {"start": v(-0.68, -14.45) * mm, "end": v(-0.62, -14.46) * mm});
            skLineSegment(sketch, "E1343", {"start": v(49.72, -12.93) * mm, "end": v(49.78, -12.96) * mm});
            skLineSegment(sketch, "E1344", {"start": v(-3.1, -16.88) * mm, "end": v(-3.15, -16.94) * mm});
            skLineSegment(sketch, "E1345", {"start": v(-28.9, -16.75) * mm, "end": v(-28.93, -16.82) * mm});
            skLineSegment(sketch, "E1346", {"start": v(30.4, -13.63) * mm, "end": v(30.4, -13.66) * mm});
            skLineSegment(sketch, "E1347", {"start": v(49.45, -17.12) * mm, "end": v(49.52, -17.12) * mm});
            skLineSegment(sketch, "E1348", {"start": v(26.82, -17.07) * mm, "end": v(26.76, -17.1) * mm});
            skLineSegment(sketch, "E1349", {"start": v(-37.13, -13.6) * mm, "end": v(-37.1, -13.66) * mm});
            skLineSegment(sketch, "E1350", {"start": v(-26.3, -17.03) * mm, "end": v(-26.37, -17.07) * mm});
            skLineSegment(sketch, "E1351", {"start": v(39.89, -13.7) * mm, "end": v(39.85, -13.75) * mm});
            skLineSegment(sketch, "E1352", {"start": v(-45.66, -13.18) * mm, "end": v(-45.69, -13.25) * mm});
            skLineSegment(sketch, "E1353", {"start": v(46.21, -16.82) * mm, "end": v(46.25, -16.88) * mm});
            skLineSegment(sketch, "E1354", {"start": v(-19.07, -17.03) * mm, "end": v(-19.13, -17.07) * mm});
            skLineSegment(sketch, "E1355", {"start": v(0.26, -13.25) * mm, "end": v(0.25, -13.28) * mm});
            skLineSegment(sketch, "E1356", {"start": v(11.28, -14.81) * mm, "end": v(11.3, -14.88) * mm});
            skLineSegment(sketch, "E1357", {"start": v(29.12, -14.54) * mm, "end": v(29.07, -14.59) * mm});
            skLineSegment(sketch, "E1358", {"start": v(-0.95, -12.93) * mm, "end": v(-1, -12.97) * mm});
            skLineSegment(sketch, "E1359", {"start": v(-26.7, -15.53) * mm, "end": v(-26.63, -15.54) * mm});
            skLineSegment(sketch, "E1360", {"start": v(-49.1, -16.94) * mm, "end": v(-49.15, -17) * mm});
            skLineSegment(sketch, "E1361", {"start": v(37.15, -16.53) * mm, "end": v(37.15, -16.6) * mm});
            skLineSegment(sketch, "E1362", {"start": v(26.36, -17.07) * mm, "end": v(26.42, -17.1) * mm});
            skLineSegment(sketch, "E1363", {"start": v(-26.2, -16.93) * mm, "end": v(-26.26, -16.99) * mm});
            skLineSegment(sketch, "E1364", {"start": v(-36.12, -13.38) * mm, "end": v(-36.12, -13.45) * mm});
            skLineSegment(sketch, "E1365", {"start": v(-49.77, -17.03) * mm, "end": v(-49.72, -17.07) * mm});
            skLineSegment(sketch, "E1366", {"start": v(0.27, -13.63) * mm, "end": v(0.28, -13.66) * mm});
            skLineSegment(sketch, "E1367", {"start": v(-0.34, -13.06) * mm, "end": v(-0.3, -13.11) * mm});
            skLineSegment(sketch, "E1368", {"start": v(9.3, -16.03) * mm, "end": v(9.22, -16.03) * mm});
            skLineSegment(sketch, "E1369", {"start": v(-39.2, -16.08) * mm, "end": v(-39.15, -16.12) * mm});
            skLineSegment(sketch, "E1370", {"start": v(20.35, -15.2) * mm, "end": v(20.37, -15.24) * mm});
            skLineSegment(sketch, "E1371", {"start": v(10.33, -14.76) * mm, "end": v(10.3, -14.82) * mm});
            skLineSegment(sketch, "E1372", {"start": v(19.75, -14.63) * mm, "end": v(19.79, -14.69) * mm});
            skLineSegment(sketch, "E1373", {"start": v(30.36, -15) * mm, "end": v(30.36, -15.07) * mm});
            skLineSegment(sketch, "E1374", {"start": v(-0.83, -17.11) * mm, "end": v(-0.77, -17.12) * mm});
            skLineSegment(sketch, "E1375", {"start": v(-16.57, -14.45) * mm, "end": v(-16.63, -14.46) * mm});
            skLineSegment(sketch, "E1376", {"start": v(-28.88, -16.53) * mm, "end": v(-28.88, -16.6) * mm});
            skLineSegment(sketch, "E1377", {"start": v(-27.02, -16.88) * mm, "end": v(-26.98, -16.93) * mm});
            skLineSegment(sketch, "E1378", {"start": v(-46.44, -12.93) * mm, "end": v(-46.38, -12.96) * mm});
            skLineSegment(sketch, "E1379", {"start": v(-26.87, -17.03) * mm, "end": v(-26.82, -17.07) * mm});
            skLineSegment(sketch, "E1380", {"start": v(39.95, -13.53) * mm, "end": v(39.93, -13.6) * mm});
            skLineSegment(sketch, "E1381", {"start": v(-45.69, -13.25) * mm, "end": v(-45.7, -13.31) * mm});
            skLineSegment(sketch, "E1382", {"start": v(-18.92, -16.88) * mm, "end": v(-18.97, -16.94) * mm});
            skLineSegment(sketch, "E1383", {"start": v(11.25, -14.75) * mm, "end": v(11.28, -14.81) * mm});
            skLineSegment(sketch, "E1384", {"start": v(29.07, -14.59) * mm, "end": v(29.01, -14.64) * mm});
            skLineSegment(sketch, "E1385", {"start": v(18.86, -13.25) * mm, "end": v(18.84, -13.31) * mm});
            skLineSegment(sketch, "E1386", {"start": v(-25, -12.89) * mm, "end": v(-24.94, -12.9) * mm});
            skLineSegment(sketch, "E1387", {"start": v(19.6, -14.5) * mm, "end": v(19.65, -14.54) * mm});
            skLineSegment(sketch, "E1388", {"start": v(19.87, -13.38) * mm, "end": v(19.87, -13.45) * mm});
            skLineSegment(sketch, "E1389", {"start": v(-16.43, -14.46) * mm, "end": v(-16.37, -14.48) * mm});
            skLineSegment(sketch, "E1390", {"start": v(16.26, -17.03) * mm, "end": v(16.32, -17.07) * mm});
            skLineSegment(sketch, "E1391", {"start": v(38.95, -13.6) * mm, "end": v(38.97, -13.66) * mm});
            skLineSegment(sketch, "E1392", {"start": v(-46.78, -17.11) * mm, "end": v(-46.71, -17.12) * mm});
            skLineSegment(sketch, "E1393", {"start": v(-37.15, -13.38) * mm, "end": v(-37.15, -13.46) * mm});
            skLineSegment(sketch, "E1394", {"start": v(-44.8, -13.06) * mm, "end": v(-44.77, -13.11) * mm});
            skLineSegment(sketch, "E1395", {"start": v(-49.2, -17.03) * mm, "end": v(-49.26, -17.07) * mm});
            skLineSegment(sketch, "E1396", {"start": v(29.8, -14.63) * mm, "end": v(29.83, -14.69) * mm});
            skLineSegment(sketch, "E1397", {"start": v(47.1, -16.88) * mm, "end": v(47.07, -16.94) * mm});
            skLineSegment(sketch, "E1398", {"start": v(-19.74, -16.93) * mm, "end": v(-19.7, -16.99) * mm});
            skLineSegment(sketch, "E1399", {"start": v(46.18, -16.72) * mm, "end": v(46.19, -16.75) * mm});
            skLineSegment(sketch, "E1400", {"start": v(9.22, -16.03) * mm, "end": v(9.16, -16.05) * mm});
            skLineSegment(sketch, "E1401", {"start": v(-39.66, -16.09) * mm, "end": v(-39.72, -16.12) * mm});
            skLineSegment(sketch, "E1402", {"start": v(1.23, -13.23) * mm, "end": v(1.25, -13.3) * mm});
            skLineSegment(sketch, "E1403", {"start": v(-15.45, -13.07) * mm, "end": v(-15.5, -13.12) * mm});
            skLineSegment(sketch, "E1404", {"start": v(10.3, -14.82) * mm, "end": v(10.29, -14.85) * mm});
            skLineSegment(sketch, "E1405", {"start": v(20.54, -15.45) * mm, "end": v(20.6, -15.49) * mm});
            skLineSegment(sketch, "E1406", {"start": v(-25.13, -12.88) * mm, "end": v(-25.2, -12.89) * mm});
            skLineSegment(sketch, "E1407", {"start": v(-49.87, -16.93) * mm, "end": v(-49.83, -16.99) * mm});
            skLineSegment(sketch, "E1408", {"start": v(-16.45, -17.11) * mm, "end": v(-16.51, -17.12) * mm});
            skLineSegment(sketch, "E1409", {"start": v(49.26, -17.07) * mm, "end": v(49.32, -17.1) * mm});
            skLineSegment(sketch, "E1410", {"start": v(26.88, -17.03) * mm, "end": v(26.82, -17.07) * mm});
            skLineSegment(sketch, "E1411", {"start": v(-46.9, -12.93) * mm, "end": v(-46.95, -12.97) * mm});
            skLineSegment(sketch, "E1412", {"start": v(46.25, -16.88) * mm, "end": v(46.29, -16.93) * mm});
            skLineSegment(sketch, "E1413", {"start": v(30.49, -13.77) * mm, "end": v(30.53, -13.83) * mm});
            skLineSegment(sketch, "E1414", {"start": v(-36.14, -13.23) * mm, "end": v(-36.13, -13.3) * mm});
            skLineSegment(sketch, "E1415", {"start": v(9.7, -13.06) * mm, "end": v(9.74, -13.11) * mm});
            skLineSegment(sketch, "E1416", {"start": v(6.4, -17.11) * mm, "end": v(6.46, -17.12) * mm});
            skLineSegment(sketch, "E1417", {"start": v(1.23, -13.6) * mm, "end": v(1.2, -13.66) * mm});
            skLineSegment(sketch, "E1418", {"start": v(-1.12, -13.07) * mm, "end": v(-1.16, -13.12) * mm});
            skLineSegment(sketch, "E1419", {"start": v(10.27, -15) * mm, "end": v(10.28, -15.07) * mm});
            skLineSegment(sketch, "E1420", {"start": v(30.36, -14.92) * mm, "end": v(30.36, -15) * mm});
            skLineSegment(sketch, "E1421", {"start": v(19.14, -14.5) * mm, "end": v(19.08, -14.54) * mm});
            skLineSegment(sketch, "E1422", {"start": v(18.83, -13.38) * mm, "end": v(18.83, -13.46) * mm});
            skLineSegment(sketch, "E1423", {"start": v(36.12, -16.54) * mm, "end": v(36.12, -16.62) * mm});
            skLineSegment(sketch, "E1424", {"start": v(16.83, -17.03) * mm, "end": v(16.77, -17.07) * mm});
            skLineSegment(sketch, "E1425", {"start": v(-0.63, -17.11) * mm, "end": v(-0.7, -17.12) * mm});
            skLineSegment(sketch, "E1426", {"start": v(49.77, -17.03) * mm, "end": v(49.7, -17.07) * mm});
            skLineSegment(sketch, "E1427", {"start": v(-46.56, -12.89) * mm, "end": v(-46.5, -12.9) * mm});
            skLineSegment(sketch, "E1428", {"start": v(-36.15, -13.6) * mm, "end": v(-36.17, -13.66) * mm});
            skLineSegment(sketch, "E1429", {"start": v(-44.71, -13.23) * mm, "end": v(-44.7, -13.3) * mm});
            skLineSegment(sketch, "E1430", {"start": v(31.3, -13.72) * mm, "end": v(31.26, -13.78) * mm});
            skLineSegment(sketch, "E1431", {"start": v(47.17, -16.75) * mm, "end": v(47.14, -16.82) * mm});
            skLineSegment(sketch, "E1432", {"start": v(9.1, -12.93) * mm, "end": v(9.04, -12.97) * mm});
            skLineSegment(sketch, "E1433", {"start": v(9.55, -12.93) * mm, "end": v(9.6, -12.96) * mm});
            skLineSegment(sketch, "E1434", {"start": v(19.84, -13.23) * mm, "end": v(19.86, -13.3) * mm});
            skLineSegment(sketch, "E1435", {"start": v(-39.82, -16.22) * mm, "end": v(-39.87, -16.28) * mm});
            skLineSegment(sketch, "E1436", {"start": v(31.36, -14.81) * mm, "end": v(31.38, -14.88) * mm});
            skLineSegment(sketch, "E1437", {"start": v(21.12, -15.45) * mm, "end": v(21.06, -15.49) * mm});
            skLineSegment(sketch, "E1438", {"start": v(49.88, -13.06) * mm, "end": v(49.92, -13.11) * mm});
            skLineSegment(sketch, "E1439", {"start": v(20.44, -15.35) * mm, "end": v(20.5, -15.4) * mm});
            skLineSegment(sketch, "E1440", {"start": v(-26.5, -15.53) * mm, "end": v(-26.56, -15.54) * mm});
            skLineSegment(sketch, "E1441", {"start": v(-3.26, -17.03) * mm, "end": v(-3.31, -17.07) * mm});
            skLineSegment(sketch, "E1442", {"start": v(19.47, -14.46) * mm, "end": v(19.53, -14.48) * mm});
            skLineSegment(sketch, "E1443", {"start": v(49.38, -17.11) * mm, "end": v(49.45, -17.12) * mm});
            skLineSegment(sketch, "E1444", {"start": v(-3.83, -17.03) * mm, "end": v(-3.77, -17.07) * mm});
            skLineSegment(sketch, "E1445", {"start": v(-46.58, -17.11) * mm, "end": v(-46.64, -17.12) * mm});
            skLineSegment(sketch, "E1446", {"start": v(39.85, -13.75) * mm, "end": v(39.8, -13.8) * mm});
            skLineSegment(sketch, "E1447", {"start": v(-45.58, -13.07) * mm, "end": v(-45.63, -13.12) * mm});
            skLineSegment(sketch, "E1448", {"start": v(9.43, -16.03) * mm, "end": v(9.5, -16.05) * mm});
            skLineSegment(sketch, "E1449", {"start": v(-14.9, -12.9) * mm, "end": v(-14.83, -12.93) * mm});
            skLineSegment(sketch, "E1450", {"start": v(29.64, -14.5) * mm, "end": v(29.7, -14.54) * mm});
            skLineSegment(sketch, "E1451", {"start": v(30.41, -14.76) * mm, "end": v(30.39, -14.82) * mm});
            skLineSegment(sketch, "E1452", {"start": v(18.97, -14.64) * mm, "end": v(18.92, -14.7) * mm});
            skLineSegment(sketch, "E1453", {"start": v(11.3, -14.96) * mm, "end": v(11.3, -15.03) * mm});
            skLineSegment(sketch, "E1454", {"start": v(21.32, -15.17) * mm, "end": v(21.3, -15.24) * mm});
            skLineSegment(sketch, "E1455", {"start": v(-26.7, -17.11) * mm, "end": v(-26.63, -17.12) * mm});
            skLineSegment(sketch, "E1456", {"start": v(36.17, -16.34) * mm, "end": v(36.15, -16.4) * mm});
            skLineSegment(sketch, "E1457", {"start": v(16.65, -17.11) * mm, "end": v(16.58, -17.12) * mm});
            skLineSegment(sketch, "E1458", {"start": v(39.05, -13.77) * mm, "end": v(39.1, -13.83) * mm});
            skLineSegment(sketch, "E1459", {"start": v(-44.96, -12.93) * mm, "end": v(-44.9, -12.96) * mm});
            skLineSegment(sketch, "E1460", {"start": v(31.36, -13.6) * mm, "end": v(31.34, -13.66) * mm});
            skLineSegment(sketch, "E1461", {"start": v(8.93, -13.07) * mm, "end": v(8.88, -13.12) * mm});
            skLineSegment(sketch, "E1462", {"start": v(-19.46, -17.11) * mm, "end": v(-19.4, -17.12) * mm});
            skLineSegment(sketch, "E1463", {"start": v(6.6, -17.11) * mm, "end": v(6.53, -17.12) * mm});
            skLineSegment(sketch, "E1464", {"start": v(-15.16, -12.89) * mm, "end": v(-15.22, -12.9) * mm});
            skLineSegment(sketch, "E1465", {"start": v(31.39, -14.96) * mm, "end": v(31.39, -15.03) * mm});
            skLineSegment(sketch, "E1466", {"start": v(49.6, -12.89) * mm, "end": v(49.66, -12.9) * mm});
            skLineSegment(sketch, "E1467", {"start": v(-4.03, -16.75) * mm, "end": v(-4, -16.82) * mm});
            skLineSegment(sketch, "E1468", {"start": v(-16.27, -17.03) * mm, "end": v(-16.32, -17.07) * mm});
            skLineSegment(sketch, "E1469", {"start": v(37.12, -16.39) * mm, "end": v(37.14, -16.46) * mm});
            skLineSegment(sketch, "E1470", {"start": v(26.7, -17.11) * mm, "end": v(26.62, -17.12) * mm});
            skLineSegment(sketch, "E1471", {"start": v(-28.93, -16.82) * mm, "end": v(-28.97, -16.88) * mm});
            skLineSegment(sketch, "E1472", {"start": v(-36.17, -13.17) * mm, "end": v(-36.14, -13.23) * mm});
            skLineSegment(sketch, "E1473", {"start": v(-38.94, -16.46) * mm, "end": v(-38.93, -16.53) * mm});
            skLineSegment(sketch, "E1474", {"start": v(-18.87, -16.75) * mm, "end": v(-18.9, -16.82) * mm});
            skLineSegment(sketch, "E1475", {"start": v(39.93, -13.6) * mm, "end": v(39.9, -13.66) * mm});
            skLineSegment(sketch, "E1476", {"start": v(6.22, -17.03) * mm, "end": v(6.27, -17.07) * mm});
            skLineSegment(sketch, "E1477", {"start": v(-19.19, -17.1) * mm, "end": v(-19.26, -17.11) * mm});
            skLineSegment(sketch, "E1478", {"start": v(-14.83, -12.93) * mm, "end": v(-14.78, -12.96) * mm});
            skLineSegment(sketch, "E1479", {"start": v(0.32, -13.12) * mm, "end": v(0.28, -13.18) * mm});
            skLineSegment(sketch, "E1480", {"start": v(-26.82, -15.49) * mm, "end": v(-26.76, -15.52) * mm});
            skLineSegment(sketch, "E1481", {"start": v(-16.25, -14.54) * mm, "end": v(-16.2, -14.58) * mm});
            skLineSegment(sketch, "E1482", {"start": v(-16.83, -17.03) * mm, "end": v(-16.77, -17.07) * mm});
            skLineSegment(sketch, "E1483", {"start": v(49.1, -13.07) * mm, "end": v(49.06, -13.12) * mm});
            skLineSegment(sketch, "E1484", {"start": v(-29.83, -16.88) * mm, "end": v(-29.79, -16.93) * mm});
            skLineSegment(sketch, "E1485", {"start": v(-46.38, -12.96) * mm, "end": v(-46.33, -13) * mm});
            skLineSegment(sketch, "E1486", {"start": v(-29.86, -16.82) * mm, "end": v(-29.83, -16.88) * mm});
            skLineSegment(sketch, "E1487", {"start": v(49.59, -17.11) * mm, "end": v(49.52, -17.12) * mm});
            skLineSegment(sketch, "E1488", {"start": v(-29.89, -16.75) * mm, "end": v(-29.86, -16.82) * mm});
            skLineSegment(sketch, "E1489", {"start": v(-19.58, -17.07) * mm, "end": v(-19.52, -17.1) * mm});
            skLineSegment(sketch, "E1490", {"start": v(1.2, -13.17) * mm, "end": v(1.23, -13.23) * mm});
            skLineSegment(sketch, "E1491", {"start": v(46.19, -16.75) * mm, "end": v(46.21, -16.82) * mm});
            skLineSegment(sketch, "E1492", {"start": v(-39.93, -16.4) * mm, "end": v(-39.95, -16.47) * mm});
            skLineSegment(sketch, "E1493", {"start": v(-19.84, -16.75) * mm, "end": v(-19.82, -16.82) * mm});
            skLineSegment(sketch, "E1494", {"start": v(1.18, -13.11) * mm, "end": v(1.2, -13.17) * mm});
            skLineSegment(sketch, "E1495", {"start": v(11.28, -15.17) * mm, "end": v(11.25, -15.24) * mm});
            skLineSegment(sketch, "E1496", {"start": v(-25.33, -12.93) * mm, "end": v(-25.39, -12.97) * mm});
            skLineSegment(sketch, "E1497", {"start": v(19.53, -16.05) * mm, "end": v(19.6, -16.08) * mm});
            skLineSegment(sketch, "E1498", {"start": v(-0.96, -17.07) * mm, "end": v(-0.9, -17.1) * mm});
            skLineSegment(sketch, "E1499", {"start": v(19.4, -14.45) * mm, "end": v(19.47, -14.46) * mm});
            skLineSegment(sketch, "E1500", {"start": v(-26.5, -17.11) * mm, "end": v(-26.56, -17.12) * mm});
            skLineSegment(sketch, "E1501", {"start": v(31.39, -13.45) * mm, "end": v(31.38, -13.53) * mm});
            skLineSegment(sketch, "E1502", {"start": v(9.78, -13.17) * mm, "end": v(9.8, -13.23) * mm});
            skLineSegment(sketch, "E1503", {"start": v(-45.42, -12.93) * mm, "end": v(-45.48, -12.97) * mm});
            skLineSegment(sketch, "E1504", {"start": v(-38.93, -16.53) * mm, "end": v(-38.93, -16.6) * mm});
            skLineSegment(sketch, "E1505", {"start": v(10.3, -15.2) * mm, "end": v(10.32, -15.24) * mm});
            skLineSegment(sketch, "E1506", {"start": v(0.36, -13.07) * mm, "end": v(0.32, -13.12) * mm});
            skLineSegment(sketch, "E1507", {"start": v(20.6, -15.49) * mm, "end": v(20.66, -15.52) * mm});
            skLineSegment(sketch, "E1508", {"start": v(-28.9, -16.39) * mm, "end": v(-28.9, -16.46) * mm});
            skLineSegment(sketch, "E1509", {"start": v(-24.88, -12.93) * mm, "end": v(-24.82, -12.96) * mm});
            skLineSegment(sketch, "E1510", {"start": v(-1.23, -13.25) * mm, "end": v(-1.24, -13.31) * mm});
            skLineSegment(sketch, "E1511", {"start": v(-3.05, -16.75) * mm, "end": v(-3.08, -16.82) * mm});
            skLineSegment(sketch, "E1512", {"start": v(-0.82, -14.46) * mm, "end": v(-0.88, -14.48) * mm});
            skLineSegment(sketch, "E1513", {"start": v(26.25, -16.99) * mm, "end": v(26.3, -17.03) * mm});
            skLineSegment(sketch, "E1514", {"start": v(19.27, -16.03) * mm, "end": v(19.2, -16.05) * mm});
            skLineSegment(sketch, "E1515", {"start": v(31.16, -13.88) * mm, "end": v(31.1, -13.91) * mm});
            skLineSegment(sketch, "E1516", {"start": v(-0.24, -13.23) * mm, "end": v(-0.23, -13.3) * mm});
            skLineSegment(sketch, "E1517", {"start": v(-0.62, -14.46) * mm, "end": v(-0.55, -14.48) * mm});
            skLineSegment(sketch, "E1518", {"start": v(30.4, -15.2) * mm, "end": v(30.4, -15.24) * mm});
            skLineSegment(sketch, "E1519", {"start": v(6.79, -17.03) * mm, "end": v(6.73, -17.07) * mm});
            skLineSegment(sketch, "E1520", {"start": v(-15.53, -13.18) * mm, "end": v(-15.56, -13.25) * mm});
            skLineSegment(sketch, "E1521", {"start": v(-26.43, -15.52) * mm, "end": v(-26.5, -15.53) * mm});
            skLineSegment(sketch, "E1522", {"start": v(37.03, -16.2) * mm, "end": v(37.07, -16.27) * mm});
            skLineSegment(sketch, "E1523", {"start": v(-4.05, -16.69) * mm, "end": v(-4.03, -16.75) * mm});
            skLineSegment(sketch, "E1524", {"start": v(30.38, -13.56) * mm, "end": v(30.4, -13.63) * mm});
            skLineSegment(sketch, "E1525", {"start": v(37.12, -16.75) * mm, "end": v(37.1, -16.82) * mm});
            skLineSegment(sketch, "E1526", {"start": v(19.6, -16.08) * mm, "end": v(19.65, -16.11) * mm});
            skLineSegment(sketch, "E1527", {"start": v(-38.95, -16.39) * mm, "end": v(-38.94, -16.46) * mm});
            skLineSegment(sketch, "E1528", {"start": v(26.98, -16.94) * mm, "end": v(26.93, -17) * mm});
            skLineSegment(sketch, "E1529", {"start": v(-47, -13.01) * mm, "end": v(-47.06, -13.07) * mm});
            skLineSegment(sketch, "E1530", {"start": v(30.59, -13.87) * mm, "end": v(30.64, -13.9) * mm});
            skLineSegment(sketch, "E1531", {"start": v(-45.29, -12.89) * mm, "end": v(-45.35, -12.9) * mm});
            skLineSegment(sketch, "E1532", {"start": v(38.92, -13.38) * mm, "end": v(38.92, -13.46) * mm});
            skLineSegment(sketch, "E1533", {"start": v(28.97, -14.7) * mm, "end": v(28.93, -14.76) * mm});
            skLineSegment(sketch, "E1534", {"start": v(0.28, -13.18) * mm, "end": v(0.26, -13.25) * mm});
            skLineSegment(sketch, "E1535", {"start": v(-14.64, -13.11) * mm, "end": v(-14.6, -13.17) * mm});
            skLineSegment(sketch, "E1536", {"start": v(49.47, -12.88) * mm, "end": v(49.4, -12.89) * mm});
            skLineSegment(sketch, "E1537", {"start": v(-45.08, -12.89) * mm, "end": v(-45.02, -12.9) * mm});
            skLineSegment(sketch, "E1538", {"start": v(49.47, -12.88) * mm, "end": v(49.54, -12.88) * mm});
            skLineSegment(sketch, "E1539", {"start": v(36.13, -16.69) * mm, "end": v(36.14, -16.75) * mm});
            skLineSegment(sketch, "E1540", {"start": v(-26.08, -16.6) * mm, "end": v(-26.09, -16.68) * mm});
            skLineSegment(sketch, "E1541", {"start": v(-49.06, -16.88) * mm, "end": v(-49.1, -16.94) * mm});
            skLineSegment(sketch, "E1542", {"start": v(26.3, -17.03) * mm, "end": v(26.36, -17.07) * mm});
            skLineSegment(sketch, "E1543", {"start": v(0.24, -13.56) * mm, "end": v(0.27, -13.63) * mm});
            skLineSegment(sketch, "E1544", {"start": v(39.22, -13.9) * mm, "end": v(39.28, -13.94) * mm});
            skLineSegment(sketch, "E1545", {"start": v(31.38, -13.53) * mm, "end": v(31.36, -13.6) * mm});
            skLineSegment(sketch, "E1546", {"start": v(-37.1, -13.18) * mm, "end": v(-37.13, -13.25) * mm});
            skLineSegment(sketch, "E1547", {"start": v(29.86, -14.75) * mm, "end": v(29.89, -14.81) * mm});
            skLineSegment(sketch, "E1548", {"start": v(39.96, -13.38) * mm, "end": v(39.96, -13.45) * mm});
            skLineSegment(sketch, "E1549", {"start": v(9.22, -12.89) * mm, "end": v(9.16, -12.9) * mm});
            skLineSegment(sketch, "E1550", {"start": v(29.83, -14.69) * mm, "end": v(29.86, -14.75) * mm});
            skLineSegment(sketch, "E1551", {"start": v(6.9, -16.94) * mm, "end": v(6.84, -17) * mm});
            skLineSegment(sketch, "E1552", {"start": v(-19.82, -16.82) * mm, "end": v(-19.79, -16.88) * mm});
            skLineSegment(sketch, "E1553", {"start": v(19.47, -16.03) * mm, "end": v(19.53, -16.05) * mm});
            skLineSegment(sketch, "E1554", {"start": v(21, -15.52) * mm, "end": v(20.93, -15.53) * mm});
            skLineSegment(sketch, "E1555", {"start": v(49.54, -12.88) * mm, "end": v(49.6, -12.89) * mm});
            skLineSegment(sketch, "E1556", {"start": v(-26.37, -15.49) * mm, "end": v(-26.43, -15.52) * mm});
            skLineSegment(sketch, "E1557", {"start": v(37.15, -16.6) * mm, "end": v(37.14, -16.68) * mm});
            skLineSegment(sketch, "E1558", {"start": v(49.45, -15.54) * mm, "end": v(49.52, -15.54) * mm});
            skLineSegment(sketch, "E1559", {"start": v(9.43, -12.89) * mm, "end": v(9.5, -12.9) * mm});
            skLineSegment(sketch, "E1560", {"start": v(6.11, -16.93) * mm, "end": v(6.16, -16.99) * mm});
            skLineSegment(sketch, "E1561", {"start": v(-29.89, -16.4) * mm, "end": v(-29.9, -16.47) * mm});
            skLineSegment(sketch, "E1562", {"start": v(-49.72, -17.07) * mm, "end": v(-49.66, -17.1) * mm});
            skLineSegment(sketch, "E1563", {"start": v(-46.95, -12.97) * mm, "end": v(-47, -13.01) * mm});
            skLineSegment(sketch, "E1564", {"start": v(-27.11, -16.61) * mm, "end": v(-27.1, -16.68) * mm});
            skLineSegment(sketch, "E1565", {"start": v(47.2, -16.6) * mm, "end": v(47.18, -16.68) * mm});
            skLineSegment(sketch, "E1566", {"start": v(-39.15, -16.12) * mm, "end": v(-39.1, -16.16) * mm});
            skLineSegment(sketch, "E1567", {"start": v(-14.6, -13.17) * mm, "end": v(-14.58, -13.23) * mm});
            skLineSegment(sketch, "E1568", {"start": v(29.01, -14.64) * mm, "end": v(28.97, -14.7) * mm});
            skLineSegment(sketch, "E1569", {"start": v(18.89, -13.18) * mm, "end": v(18.86, -13.25) * mm});
            skLineSegment(sketch, "E1570", {"start": v(31.36, -15.17) * mm, "end": v(31.34, -15.24) * mm});
            skLineSegment(sketch, "E1571", {"start": v(-44.69, -13.45) * mm, "end": v(-44.7, -13.53) * mm});
            skLineSegment(sketch, "E1572", {"start": v(-16.89, -16.99) * mm, "end": v(-16.83, -17.03) * mm});
            skLineSegment(sketch, "E1573", {"start": v(49.59, -15.53) * mm, "end": v(49.52, -15.54) * mm});
            skLineSegment(sketch, "E1574", {"start": v(-28.9, -16.46) * mm, "end": v(-28.88, -16.53) * mm});
            skLineSegment(sketch, "E1575", {"start": v(36.25, -16.22) * mm, "end": v(36.2, -16.28) * mm});
            skLineSegment(sketch, "E1576", {"start": v(-26.63, -17.12) * mm, "end": v(-26.56, -17.12) * mm});
            skLineSegment(sketch, "E1577", {"start": v(29.52, -14.46) * mm, "end": v(29.58, -14.48) * mm});
            skLineSegment(sketch, "E1578", {"start": v(49.4, -14.46) * mm, "end": v(49.33, -14.48) * mm});
            skLineSegment(sketch, "E1579", {"start": v(30.36, -13.42) * mm, "end": v(30.36, -13.5) * mm});
            skLineSegment(sketch, "E1580", {"start": v(-49.26, -17.07) * mm, "end": v(-49.32, -17.1) * mm});
            skLineSegment(sketch, "E1581", {"start": v(47.07, -16.94) * mm, "end": v(47.02, -17) * mm});
            skLineSegment(sketch, "E1582", {"start": v(8.84, -13.18) * mm, "end": v(8.82, -13.25) * mm});
            skLineSegment(sketch, "E1583", {"start": v(-19.79, -16.88) * mm, "end": v(-19.74, -16.93) * mm});
            skLineSegment(sketch, "E1584", {"start": v(-39.72, -16.12) * mm, "end": v(-39.77, -16.17) * mm});
            skLineSegment(sketch, "E1585", {"start": v(-15.5, -13.12) * mm, "end": v(-15.53, -13.18) * mm});
            skLineSegment(sketch, "E1586", {"start": v(-0.68, -12.88) * mm, "end": v(-0.62, -12.89) * mm});
            skLineSegment(sketch, "E1587", {"start": v(19.87, -13.45) * mm, "end": v(19.86, -13.53) * mm});
            skLineSegment(sketch, "E1588", {"start": v(11.22, -15.3) * mm, "end": v(11.18, -15.36) * mm});
            skLineSegment(sketch, "E1589", {"start": v(21.06, -15.49) * mm, "end": v(21, -15.52) * mm});
            skLineSegment(sketch, "E1590", {"start": v(19.85, -14.85) * mm, "end": v(19.87, -14.92) * mm});
            skLineSegment(sketch, "E1591", {"start": v(-0.77, -15.54) * mm, "end": v(-0.7, -15.54) * mm});
            skLineSegment(sketch, "E1592", {"start": v(-25.2, -12.89) * mm, "end": v(-25.27, -12.9) * mm});
            skLineSegment(sketch, "E1593", {"start": v(16.32, -17.07) * mm, "end": v(16.38, -17.1) * mm});
            skLineSegment(sketch, "E1594", {"start": v(49.6, -14.46) * mm, "end": v(49.66, -14.48) * mm});
            skLineSegment(sketch, "E1595", {"start": v(-45.72, -13.46) * mm, "end": v(-45.7, -13.53) * mm});
            skLineSegment(sketch, "E1596", {"start": v(46.29, -16.93) * mm, "end": v(46.34, -16.99) * mm});
            skLineSegment(sketch, "E1597", {"start": v(-49.92, -16.88) * mm, "end": v(-49.87, -16.93) * mm});
            skLineSegment(sketch, "E1598", {"start": v(-16.88, -14.59) * mm, "end": v(-16.93, -14.64) * mm});
            skLineSegment(sketch, "E1599", {"start": v(-36.97, -13.83) * mm, "end": v(-36.92, -13.87) * mm});
            skLineSegment(sketch, "E1600", {"start": v(-26.6, -14.45) * mm, "end": v(-26.54, -14.45) * mm});
            skLineSegment(sketch, "E1601", {"start": v(-27.1, -16.68) * mm, "end": v(-27.09, -16.75) * mm});
            skLineSegment(sketch, "E1602", {"start": v(9.6, -16.11) * mm, "end": v(9.66, -16.16) * mm});
            skLineSegment(sketch, "E1603", {"start": v(39.7, -13.9) * mm, "end": v(39.64, -13.92) * mm});
            skLineSegment(sketch, "E1604", {"start": v(-18.9, -16.82) * mm, "end": v(-18.92, -16.88) * mm});
            skLineSegment(sketch, "E1605", {"start": v(-24.94, -12.9) * mm, "end": v(-24.88, -12.93) * mm});
            skLineSegment(sketch, "E1606", {"start": v(-0.75, -12.88) * mm, "end": v(-0.68, -12.88) * mm});
            skLineSegment(sketch, "E1607", {"start": v(19.86, -13.53) * mm, "end": v(19.84, -13.6) * mm});
            skLineSegment(sketch, "E1608", {"start": v(18.83, -13.46) * mm, "end": v(18.84, -13.53) * mm});
            skLineSegment(sketch, "E1609", {"start": v(-39.4, -16.03) * mm, "end": v(-39.32, -16.04) * mm});
            skLineSegment(sketch, "E1610", {"start": v(16.77, -17.07) * mm, "end": v(16.71, -17.1) * mm});
            skLineSegment(sketch, "E1611", {"start": v(-0.57, -17.1) * mm, "end": v(-0.63, -17.11) * mm});
            skLineSegment(sketch, "E1612", {"start": v(-44.74, -13.17) * mm, "end": v(-44.71, -13.23) * mm});
            skLineSegment(sketch, "E1613", {"start": v(-46.71, -17.12) * mm, "end": v(-46.64, -17.12) * mm});
            skLineSegment(sketch, "E1614", {"start": v(31.26, -13.78) * mm, "end": v(31.21, -13.83) * mm});
            skLineSegment(sketch, "E1615", {"start": v(-49.32, -17.1) * mm, "end": v(-49.39, -17.11) * mm});
            skLineSegment(sketch, "E1616", {"start": v(9.04, -16.12) * mm, "end": v(8.98, -16.16) * mm});
            skLineSegment(sketch, "E1617", {"start": v(46.16, -16.58) * mm, "end": v(46.17, -16.65) * mm});
            skLineSegment(sketch, "E1618", {"start": v(19.82, -13.17) * mm, "end": v(19.84, -13.23) * mm});
            skLineSegment(sketch, "E1619", {"start": v(-39.77, -16.17) * mm, "end": v(-39.82, -16.22) * mm});
            skLineSegment(sketch, "E1620", {"start": v(-14.57, -13.53) * mm, "end": v(-14.58, -13.6) * mm});
            skLineSegment(sketch, "E1621", {"start": v(31.17, -14.54) * mm, "end": v(31.22, -14.58) * mm});
            skLineSegment(sketch, "E1622", {"start": v(19.87, -14.92) * mm, "end": v(19.87, -15) * mm});
            skLineSegment(sketch, "E1623", {"start": v(30.4, -15.24) * mm, "end": v(30.44, -15.3) * mm});
            skLineSegment(sketch, "E1624", {"start": v(-0.23, -13.3) * mm, "end": v(-0.22, -13.38) * mm});
            skLineSegment(sketch, "E1625", {"start": v(-0.55, -14.48) * mm, "end": v(-0.5, -14.5) * mm});
            skLineSegment(sketch, "E1626", {"start": v(-16.82, -14.54) * mm, "end": v(-16.88, -14.59) * mm});
            skLineSegment(sketch, "E1627", {"start": v(19.32, -17.12) * mm, "end": v(19.39, -17.12) * mm});
            skLineSegment(sketch, "E1628", {"start": v(16.12, -16.88) * mm, "end": v(16.16, -16.93) * mm});
            skLineSegment(sketch, "E1629", {"start": v(37.07, -16.27) * mm, "end": v(37.1, -16.33) * mm});
            skLineSegment(sketch, "E1630", {"start": v(-49.95, -16.82) * mm, "end": v(-49.92, -16.88) * mm});
            skLineSegment(sketch, "E1631", {"start": v(30.53, -13.83) * mm, "end": v(30.59, -13.87) * mm});
            skLineSegment(sketch, "E1632", {"start": v(-46.7, -12.88) * mm, "end": v(-46.76, -12.89) * mm});
            skLineSegment(sketch, "E1633", {"start": v(49.95, -16.82) * mm, "end": v(49.91, -16.88) * mm});
            skLineSegment(sketch, "E1634", {"start": v(-37.15, -13.53) * mm, "end": v(-37.13, -13.6) * mm});
            skLineSegment(sketch, "E1635", {"start": v(-36.2, -13.11) * mm, "end": v(-36.17, -13.17) * mm});
            skLineSegment(sketch, "E1636", {"start": v(9.36, -16.03) * mm, "end": v(9.43, -16.03) * mm});
            skLineSegment(sketch, "E1637", {"start": v(-19.13, -17.07) * mm, "end": v(-19.19, -17.1) * mm});
            skLineSegment(sketch, "E1638", {"start": v(1.25, -13.53) * mm, "end": v(1.23, -13.6) * mm});
            skLineSegment(sketch, "E1639", {"start": v(0.23, -13.5) * mm, "end": v(0.24, -13.56) * mm});
            skLineSegment(sketch, "E1640", {"start": v(10.36, -15.3) * mm, "end": v(10.4, -15.35) * mm});
            skLineSegment(sketch, "E1641", {"start": v(29.31, -14.46) * mm, "end": v(29.25, -14.48) * mm});
            skLineSegment(sketch, "E1642", {"start": v(-1, -12.97) * mm, "end": v(-1.06, -13.01) * mm});
            skLineSegment(sketch, "E1643", {"start": v(30.6, -14.54) * mm, "end": v(30.54, -14.59) * mm});
            skLineSegment(sketch, "E1644", {"start": v(-16.2, -14.58) * mm, "end": v(-16.15, -14.63) * mm});
            skLineSegment(sketch, "E1645", {"start": v(19.34, -14.45) * mm, "end": v(19.27, -14.46) * mm});
            skLineSegment(sketch, "E1646", {"start": v(-3.58, -17.12) * mm, "end": v(-3.5, -17.12) * mm});
            skLineSegment(sketch, "E1647", {"start": v(29.45, -16.03) * mm, "end": v(29.52, -16.03) * mm});
            skLineSegment(sketch, "E1648", {"start": v(16.71, -17.1) * mm, "end": v(16.65, -17.11) * mm});
            skLineSegment(sketch, "E1649", {"start": v(-49.02, -16.82) * mm, "end": v(-49.06, -16.88) * mm});
            skLineSegment(sketch, "E1650", {"start": v(26.55, -17.12) * mm, "end": v(26.62, -17.12) * mm});
            skLineSegment(sketch, "E1651", {"start": v(-26.09, -16.68) * mm, "end": v(-26.1, -16.75) * mm});
            skLineSegment(sketch, "E1652", {"start": v(-0.5, -17.07) * mm, "end": v(-0.57, -17.1) * mm});
            skLineSegment(sketch, "E1653", {"start": v(-47.02, -16.99) * mm, "end": v(-46.96, -17.03) * mm});
            skLineSegment(sketch, "E1654", {"start": v(39.95, -13.3) * mm, "end": v(39.96, -13.38) * mm});
            skLineSegment(sketch, "E1655", {"start": v(-45.02, -12.9) * mm, "end": v(-44.96, -12.93) * mm});
            skLineSegment(sketch, "E1656", {"start": v(-37.06, -13.12) * mm, "end": v(-37.1, -13.18) * mm});
            skLineSegment(sketch, "E1657", {"start": v(-44.77, -13.11) * mm, "end": v(-44.74, -13.17) * mm});
            skLineSegment(sketch, "E1658", {"start": v(-19.52, -17.1) * mm, "end": v(-19.46, -17.11) * mm});
            skLineSegment(sketch, "E1659", {"start": v(29.58, -14.48) * mm, "end": v(29.64, -14.5) * mm});
            skLineSegment(sketch, "E1660", {"start": v(-0.39, -13) * mm, "end": v(-0.34, -13.06) * mm});
            skLineSegment(sketch, "E1661", {"start": v(19.79, -13.11) * mm, "end": v(19.82, -13.17) * mm});
            skLineSegment(sketch, "E1662", {"start": v(-15.22, -12.9) * mm, "end": v(-15.29, -12.93) * mm});
            skLineSegment(sketch, "E1663", {"start": v(21.34, -14.88) * mm, "end": v(21.34, -14.96) * mm});
            skLineSegment(sketch, "E1664", {"start": v(18.84, -13.53) * mm, "end": v(18.86, -13.6) * mm});
            skLineSegment(sketch, "E1665", {"start": v(-0.75, -16.03) * mm, "end": v(-0.82, -16.03) * mm});
            skLineSegment(sketch, "E1666", {"start": v(20.37, -15.24) * mm, "end": v(20.4, -15.3) * mm});
            skLineSegment(sketch, "E1667", {"start": v(-16.21, -16.99) * mm, "end": v(-16.27, -17.03) * mm});
            skLineSegment(sketch, "E1668", {"start": v(37.1, -16.33) * mm, "end": v(37.12, -16.39) * mm});
            skLineSegment(sketch, "E1669", {"start": v(10.46, -14.59) * mm, "end": v(10.4, -14.64) * mm});
            skLineSegment(sketch, "E1670", {"start": v(-39.46, -16.03) * mm, "end": v(-39.4, -16.03) * mm});
            skLineSegment(sketch, "E1671", {"start": v(29.38, -16.03) * mm, "end": v(29.31, -16.03) * mm});
            skLineSegment(sketch, "E1672", {"start": v(-0.9, -17.1) * mm, "end": v(-0.83, -17.11) * mm});
            skLineSegment(sketch, "E1673", {"start": v(29.38, -16.03) * mm, "end": v(29.45, -16.03) * mm});
            skLineSegment(sketch, "E1674", {"start": v(-29.9, -16.47) * mm, "end": v(-29.91, -16.54) * mm});
            skLineSegment(sketch, "E1675", {"start": v(49.91, -16.88) * mm, "end": v(49.87, -16.93) * mm});
            skLineSegment(sketch, "E1676", {"start": v(-26.26, -16.99) * mm, "end": v(-26.3, -17.03) * mm});
            skLineSegment(sketch, "E1677", {"start": v(-46.7, -12.88) * mm, "end": v(-46.63, -12.88) * mm});
            skLineSegment(sketch, "E1678", {"start": v(-49.66, -17.1) * mm, "end": v(-49.6, -17.11) * mm});
            skLineSegment(sketch, "E1679", {"start": v(9.5, -12.9) * mm, "end": v(9.55, -12.93) * mm});
            skLineSegment(sketch, "E1680", {"start": v(30.36, -13.5) * mm, "end": v(30.38, -13.56) * mm});
            skLineSegment(sketch, "E1681", {"start": v(39.6, -13.94) * mm, "end": v(39.54, -13.95) * mm});
            skLineSegment(sketch, "E1682", {"start": v(-45.63, -13.12) * mm, "end": v(-45.66, -13.18) * mm});
            skLineSegment(sketch, "E1683", {"start": v(6.16, -16.99) * mm, "end": v(6.22, -17.03) * mm});
            skLineSegment(sketch, "E1684", {"start": v(-39.1, -16.16) * mm, "end": v(-39.05, -16.2) * mm});
            skLineSegment(sketch, "E1685", {"start": v(9.74, -13.11) * mm, "end": v(9.78, -13.17) * mm});
            skLineSegment(sketch, "E1686", {"start": v(18.92, -13.12) * mm, "end": v(18.89, -13.18) * mm});
            skLineSegment(sketch, "E1687", {"start": v(-19.86, -16.47) * mm, "end": v(-19.87, -16.54) * mm});
            skLineSegment(sketch, "E1688", {"start": v(11.3, -14.88) * mm, "end": v(11.3, -14.96) * mm});
            skLineSegment(sketch, "E1689", {"start": v(31.34, -15.24) * mm, "end": v(31.3, -15.3) * mm});
            skLineSegment(sketch, "E1690", {"start": v(30.54, -14.59) * mm, "end": v(30.5, -14.64) * mm});
            skLineSegment(sketch, "E1691", {"start": v(-26.76, -15.52) * mm, "end": v(-26.7, -15.53) * mm});
            skLineSegment(sketch, "E1692", {"start": v(10.32, -15.24) * mm, "end": v(10.36, -15.3) * mm});
            skLineSegment(sketch, "E1693", {"start": v(-1.24, -13.31) * mm, "end": v(-1.25, -13.38) * mm});
            skLineSegment(sketch, "E1694", {"start": v(21.3, -15.24) * mm, "end": v(21.26, -15.3) * mm});
            skLineSegment(sketch, "E1695", {"start": v(-0.88, -14.48) * mm, "end": v(-0.95, -14.5) * mm});
            skLineSegment(sketch, "E1696", {"start": v(-3.88, -16.99) * mm, "end": v(-3.83, -17.03) * mm});
            skLineSegment(sketch, "E1697", {"start": v(49.15, -13.01) * mm, "end": v(49.1, -13.07) * mm});
            skLineSegment(sketch, "E1698", {"start": v(36.2, -16.28) * mm, "end": v(36.17, -16.34) * mm});
            skLineSegment(sketch, "E1699", {"start": v(19.34, -14.45) * mm, "end": v(19.4, -14.45) * mm});
            skLineSegment(sketch, "E1700", {"start": v(-46.33, -13) * mm, "end": v(-46.28, -13.06) * mm});
            skLineSegment(sketch, "E1701", {"start": v(49.02, -16.82) * mm, "end": v(49.05, -16.88) * mm});
            skLineSegment(sketch, "E1702", {"start": v(-36.27, -13.8) * mm, "end": v(-36.33, -13.86) * mm});
            skLineSegment(sketch, "E1703", {"start": v(8.88, -13.12) * mm, "end": v(8.84, -13.18) * mm});
            skLineSegment(sketch, "E1704", {"start": v(9.3, -16.03) * mm, "end": v(9.36, -16.03) * mm});
            skLineSegment(sketch, "E1705", {"start": v(-39.95, -16.47) * mm, "end": v(-39.96, -16.54) * mm});
            skLineSegment(sketch, "E1706", {"start": v(-18.85, -16.46) * mm, "end": v(-18.84, -16.53) * mm});
            skLineSegment(sketch, "E1707", {"start": v(11.25, -15.24) * mm, "end": v(11.22, -15.3) * mm});
            skLineSegment(sketch, "E1708", {"start": v(19.7, -14.58) * mm, "end": v(19.75, -14.63) * mm});
            skLineSegment(sketch, "E1709", {"start": v(-25.27, -12.9) * mm, "end": v(-25.33, -12.93) * mm});
            skLineSegment(sketch, "E1710", {"start": v(-0.3, -14.69) * mm, "end": v(-0.28, -14.72) * mm});
            skLineSegment(sketch, "E1711", {"start": v(-4.05, -16.62) * mm, "end": v(-4.05, -16.69) * mm});
            skLineSegment(sketch, "E1712", {"start": v(-0.75, -16.03) * mm, "end": v(-0.68, -16.03) * mm});
            skLineSegment(sketch, "E1713", {"start": v(16.38, -17.1) * mm, "end": v(16.44, -17.11) * mm});
            skLineSegment(sketch, "E1714", {"start": v(49.66, -14.48) * mm, "end": v(49.72, -14.5) * mm});
            skLineSegment(sketch, "E1715", {"start": v(-46.34, -16.99) * mm, "end": v(-46.4, -17.03) * mm});
            skLineSegment(sketch, "E1716", {"start": v(-46.5, -16.05) * mm, "end": v(-46.44, -16.08) * mm});
            skLineSegment(sketch, "E1717", {"start": v(1.08, -13.83) * mm, "end": v(1.03, -13.88) * mm});
            skLineSegment(sketch, "E1718", {"start": v(46.34, -16.99) * mm, "end": v(46.4, -17.03) * mm});
            skLineSegment(sketch, "E1719", {"start": v(39.64, -13.92) * mm, "end": v(39.6, -13.94) * mm});
            skLineSegment(sketch, "E1720", {"start": v(-45.35, -12.9) * mm, "end": v(-45.42, -12.93) * mm});
            skLineSegment(sketch, "E1721", {"start": v(-16.65, -15.53) * mm, "end": v(-16.58, -15.54) * mm});
            skLineSegment(sketch, "E1722", {"start": v(20.66, -15.52) * mm, "end": v(20.72, -15.53) * mm});
            skLineSegment(sketch, "E1723", {"start": v(-16.12, -16.88) * mm, "end": v(-16.16, -16.93) * mm});
            skLineSegment(sketch, "E1724", {"start": v(18.84, -14.89) * mm, "end": v(18.83, -14.96) * mm});
            skLineSegment(sketch, "E1725", {"start": v(-3.03, -16.68) * mm, "end": v(-3.05, -16.75) * mm});
            skLineSegment(sketch, "E1726", {"start": v(20.33, -14.85) * mm, "end": v(20.32, -14.92) * mm});
            skLineSegment(sketch, "E1727", {"start": v(11.13, -14.58) * mm, "end": v(11.18, -14.63) * mm});
            skLineSegment(sketch, "E1728", {"start": v(49.21, -12.97) * mm, "end": v(49.15, -13.01) * mm});
            skLineSegment(sketch, "E1729", {"start": v(29.74, -16.16) * mm, "end": v(29.8, -16.2) * mm});
            skLineSegment(sketch, "E1730", {"start": v(36.12, -16.62) * mm, "end": v(36.13, -16.69) * mm});
            skLineSegment(sketch, "E1731", {"start": v(19.2, -16.05) * mm, "end": v(19.14, -16.08) * mm});
            skLineSegment(sketch, "E1732", {"start": v(-50, -16.47) * mm, "end": v(-50, -16.54) * mm});
            skLineSegment(sketch, "E1733", {"start": v(0.4, -13.83) * mm, "end": v(0.46, -13.87) * mm});
            skLineSegment(sketch, "E1734", {"start": v(-1.2, -16.82) * mm, "end": v(-1.17, -16.88) * mm});
            skLineSegment(sketch, "E1735", {"start": v(49.7, -17.07) * mm, "end": v(49.65, -17.1) * mm});
            skLineSegment(sketch, "E1736", {"start": v(39.28, -13.94) * mm, "end": v(39.34, -13.95) * mm});
            skLineSegment(sketch, "E1737", {"start": v(31.21, -13.83) * mm, "end": v(31.16, -13.88) * mm});
            skLineSegment(sketch, "E1738", {"start": v(9.16, -12.9) * mm, "end": v(9.1, -12.93) * mm});
            skLineSegment(sketch, "E1739", {"start": v(46.17, -16.65) * mm, "end": v(46.18, -16.72) * mm});
            skLineSegment(sketch, "E1740", {"start": v(6.84, -17) * mm, "end": v(6.79, -17.03) * mm});
            skLineSegment(sketch, "E1741", {"start": v(31.22, -14.58) * mm, "end": v(31.27, -14.63) * mm});
            skLineSegment(sketch, "E1742", {"start": v(10.29, -14.85) * mm, "end": v(10.28, -14.92) * mm});
            skLineSegment(sketch, "E1743", {"start": v(19.02, -13.83) * mm, "end": v(19.07, -13.87) * mm});
            skLineSegment(sketch, "E1744", {"start": v(49.83, -13) * mm, "end": v(49.88, -13.06) * mm});
            skLineSegment(sketch, "E1745", {"start": v(-48.98, -16.46) * mm, "end": v(-48.97, -16.53) * mm});
            skLineSegment(sketch, "E1746", {"start": v(-25.54, -13.12) * mm, "end": v(-25.58, -13.18) * mm});
            skLineSegment(sketch, "E1747", {"start": v(37.14, -16.68) * mm, "end": v(37.12, -16.75) * mm});
            skLineSegment(sketch, "E1748", {"start": v(-3.2, -17) * mm, "end": v(-3.26, -17.03) * mm});
            skLineSegment(sketch, "E1749", {"start": v(16.08, -16.82) * mm, "end": v(16.12, -16.88) * mm});
            skLineSegment(sketch, "E1750", {"start": v(-26.68, -14.46) * mm, "end": v(-26.74, -14.48) * mm});
            skLineSegment(sketch, "E1751", {"start": v(49.32, -17.1) * mm, "end": v(49.38, -17.11) * mm});
            skLineSegment(sketch, "E1752", {"start": v(16.07, -16.79) * mm, "end": v(16.08, -16.82) * mm});
            skLineSegment(sketch, "E1753", {"start": v(26.93, -17) * mm, "end": v(26.88, -17.03) * mm});
            skLineSegment(sketch, "E1754", {"start": v(-29.11, -17.03) * mm, "end": v(-29.17, -17.07) * mm});
            skLineSegment(sketch, "E1755", {"start": v(-16.71, -15.52) * mm, "end": v(-16.65, -15.53) * mm});
            skLineSegment(sketch, "E1756", {"start": v(47.18, -16.68) * mm, "end": v(47.17, -16.75) * mm});
            skLineSegment(sketch, "E1757", {"start": v(38.93, -13.31) * mm, "end": v(38.92, -13.38) * mm});
            skLineSegment(sketch, "E1758", {"start": v(19.2, -12.9) * mm, "end": v(19.14, -12.93) * mm});
            skLineSegment(sketch, "E1759", {"start": v(-19.84, -16.4) * mm, "end": v(-19.86, -16.47) * mm});
            skLineSegment(sketch, "E1760", {"start": v(29.25, -14.48) * mm, "end": v(29.18, -14.5) * mm});
            skLineSegment(sketch, "E1761", {"start": v(-29.05, -16.16) * mm, "end": v(-29, -16.2) * mm});
            skLineSegment(sketch, "E1762", {"start": v(30.38, -14.85) * mm, "end": v(30.36, -14.92) * mm});
            skLineSegment(sketch, "E1763", {"start": v(-25.19, -13.96) * mm, "end": v(-25.12, -13.96) * mm});
            skLineSegment(sketch, "E1764", {"start": v(-45.7, -13.6) * mm, "end": v(-45.67, -13.66) * mm});
            skLineSegment(sketch, "E1765", {"start": v(19.72, -13.8) * mm, "end": v(19.66, -13.86) * mm});
            skLineSegment(sketch, "E1766", {"start": v(-1.16, -14.7) * mm, "end": v(-1.2, -14.76) * mm});
            skLineSegment(sketch, "E1767", {"start": v(-26.54, -14.45) * mm, "end": v(-26.47, -14.46) * mm});
            skLineSegment(sketch, "E1768", {"start": v(-46.21, -13.17) * mm, "end": v(-46.19, -13.23) * mm});
            skLineSegment(sketch, "E1769", {"start": v(-25.05, -13.96) * mm, "end": v(-25.12, -13.96) * mm});
            skLineSegment(sketch, "E1770", {"start": v(-29.63, -17.07) * mm, "end": v(-29.57, -17.1) * mm});
            skLineSegment(sketch, "E1771", {"start": v(36.48, -16.06) * mm, "end": v(36.42, -16.09) * mm});
            skLineSegment(sketch, "E1772", {"start": v(49.33, -14.48) * mm, "end": v(49.27, -14.5) * mm});
            skLineSegment(sketch, "E1773", {"start": v(-46.76, -16.03) * mm, "end": v(-46.83, -16.05) * mm});
            skLineSegment(sketch, "E1774", {"start": v(19.53, -12.9) * mm, "end": v(19.6, -12.93) * mm});
            skLineSegment(sketch, "E1775", {"start": v(47.02, -17) * mm, "end": v(46.96, -17.03) * mm});
            skLineSegment(sketch, "E1776", {"start": v(-16.38, -15.52) * mm, "end": v(-16.45, -15.53) * mm});
            skLineSegment(sketch, "E1777", {"start": v(-0.22, -13.45) * mm, "end": v(-0.23, -13.53) * mm});
            skLineSegment(sketch, "E1778", {"start": v(-0.3, -16.88) * mm, "end": v(-0.35, -16.93) * mm});
            skLineSegment(sketch, "E1779", {"start": v(36.81, -16.06) * mm, "end": v(36.87, -16.08) * mm});
            skLineSegment(sketch, "E1780", {"start": v(-29.73, -16.17) * mm, "end": v(-29.78, -16.22) * mm});
            skLineSegment(sketch, "E1781", {"start": v(-36.34, -12.96) * mm, "end": v(-36.29, -13) * mm});
            skLineSegment(sketch, "E1782", {"start": v(9.7, -16.2) * mm, "end": v(9.74, -16.26) * mm});
            skLineSegment(sketch, "E1783", {"start": v(-45.7, -13.53) * mm, "end": v(-45.7, -13.6) * mm});
            skLineSegment(sketch, "E1784", {"start": v(6.55, -16.03) * mm, "end": v(6.62, -16.04) * mm});
            skLineSegment(sketch, "E1785", {"start": v(-16.58, -15.54) * mm, "end": v(-16.51, -15.54) * mm});
            skLineSegment(sketch, "E1786", {"start": v(-24.65, -13.17) * mm, "end": v(-24.63, -13.23) * mm});
            skLineSegment(sketch, "E1787", {"start": v(-0.23, -13.53) * mm, "end": v(-0.24, -13.6) * mm});
            skLineSegment(sketch, "E1788", {"start": v(48.97, -13.31) * mm, "end": v(48.96, -13.38) * mm});
            skLineSegment(sketch, "E1789", {"start": v(17.01, -16.82) * mm, "end": v(16.98, -16.88) * mm});
            skLineSegment(sketch, "E1790", {"start": v(-29.68, -17.03) * mm, "end": v(-29.63, -17.07) * mm});
            skLineSegment(sketch, "E1791", {"start": v(16.53, -16.03) * mm, "end": v(16.6, -16.03) * mm});
            skLineSegment(sketch, "E1792", {"start": v(39.9, -13.17) * mm, "end": v(39.93, -13.23) * mm});
            skLineSegment(sketch, "E1793", {"start": v(-36.97, -13.01) * mm, "end": v(-37.02, -13.07) * mm});
            skLineSegment(sketch, "E1794", {"start": v(-1.24, -13.53) * mm, "end": v(-1.23, -13.6) * mm});
            skLineSegment(sketch, "E1795", {"start": v(46.25, -16.28) * mm, "end": v(46.22, -16.34) * mm});
            skLineSegment(sketch, "E1796", {"start": v(-15.59, -13.46) * mm, "end": v(-15.58, -13.53) * mm});
            skLineSegment(sketch, "E1797", {"start": v(50, -13.3) * mm, "end": v(50, -13.38) * mm});
            skLineSegment(sketch, "E1798", {"start": v(6.49, -16.03) * mm, "end": v(6.55, -16.03) * mm});
            skLineSegment(sketch, "E1799", {"start": v(-4.03, -16.4) * mm, "end": v(-4.05, -16.47) * mm});
            skLineSegment(sketch, "E1800", {"start": v(-44.7, -13.53) * mm, "end": v(-44.71, -13.6) * mm});
            skLineSegment(sketch, "E1801", {"start": v(-36.29, -13) * mm, "end": v(-36.24, -13.06) * mm});
            skLineSegment(sketch, "E1802", {"start": v(10.57, -14.5) * mm, "end": v(10.51, -14.54) * mm});
            skLineSegment(sketch, "E1803", {"start": v(9.66, -16.16) * mm, "end": v(9.7, -16.2) * mm});
            skLineSegment(sketch, "E1804", {"start": v(19.13, -17.07) * mm, "end": v(19.19, -17.1) * mm});
            skLineSegment(sketch, "E1805", {"start": v(27.08, -16.75) * mm, "end": v(27.05, -16.82) * mm});
            skLineSegment(sketch, "E1806", {"start": v(16.6, -16.03) * mm, "end": v(16.66, -16.04) * mm});
            skLineSegment(sketch, "E1807", {"start": v(-26.35, -14.5) * mm, "end": v(-26.3, -14.54) * mm});
            skLineSegment(sketch, "E1808", {"start": v(-29.17, -17.07) * mm, "end": v(-29.23, -17.1) * mm});
            skLineSegment(sketch, "E1809", {"start": v(0.97, -13.91) * mm, "end": v(0.94, -13.92) * mm});
            skLineSegment(sketch, "E1810", {"start": v(46.64, -17.12) * mm, "end": v(46.7, -17.12) * mm});
            skLineSegment(sketch, "E1811", {"start": v(8.8, -13.53) * mm, "end": v(8.82, -13.6) * mm});
            skLineSegment(sketch, "E1812", {"start": v(31.26, -15.36) * mm, "end": v(31.21, -15.41) * mm});
            skLineSegment(sketch, "E1813", {"start": v(-3.07, -16.33) * mm, "end": v(-3.05, -16.39) * mm});
            skLineSegment(sketch, "E1814", {"start": v(27.1, -16.68) * mm, "end": v(27.08, -16.75) * mm});
            skLineSegment(sketch, "E1815", {"start": v(-1.25, -13.46) * mm, "end": v(-1.24, -13.53) * mm});
            skLineSegment(sketch, "E1816", {"start": v(11.08, -14.54) * mm, "end": v(11.13, -14.58) * mm});
            skLineSegment(sketch, "E1817", {"start": v(19.52, -17.1) * mm, "end": v(19.46, -17.11) * mm});
            skLineSegment(sketch, "E1818", {"start": v(36.55, -16.04) * mm, "end": v(36.48, -16.06) * mm});
            skLineSegment(sketch, "E1819", {"start": v(29.23, -17.1) * mm, "end": v(29.3, -17.11) * mm});
            skLineSegment(sketch, "E1820", {"start": v(-36.9, -12.97) * mm, "end": v(-36.97, -13.01) * mm});
            skLineSegment(sketch, "E1821", {"start": v(28.88, -15.03) * mm, "end": v(28.89, -15.1) * mm});
            skLineSegment(sketch, "E1822", {"start": v(8.98, -16.16) * mm, "end": v(8.93, -16.22) * mm});
            skLineSegment(sketch, "E1823", {"start": v(30.44, -15.3) * mm, "end": v(30.49, -15.35) * mm});
            skLineSegment(sketch, "E1824", {"start": v(19.19, -17.1) * mm, "end": v(19.25, -17.11) * mm});
            skLineSegment(sketch, "E1825", {"start": v(9.82, -13.53) * mm, "end": v(9.8, -13.6) * mm});
            skLineSegment(sketch, "E1826", {"start": v(-17.03, -16.78) * mm, "end": v(-17.02, -16.82) * mm});
            skLineSegment(sketch, "E1827", {"start": v(26.08, -16.69) * mm, "end": v(26.1, -16.75) * mm});
            skLineSegment(sketch, "E1828", {"start": v(49.78, -14.54) * mm, "end": v(49.83, -14.58) * mm});
            skLineSegment(sketch, "E1829", {"start": v(47.14, -16.33) * mm, "end": v(47.17, -16.39) * mm});
            skLineSegment(sketch, "E1830", {"start": v(9.74, -16.26) * mm, "end": v(9.76, -16.3) * mm});
            skLineSegment(sketch, "E1831", {"start": v(-14.56, -13.45) * mm, "end": v(-14.57, -13.53) * mm});
            skLineSegment(sketch, "E1832", {"start": v(20.8, -15.54) * mm, "end": v(20.86, -15.54) * mm});
            skLineSegment(sketch, "E1833", {"start": v(29.56, -17.1) * mm, "end": v(29.5, -17.11) * mm});
            skLineSegment(sketch, "E1834", {"start": v(-16.06, -16.75) * mm, "end": v(-16.08, -16.82) * mm});
            skLineSegment(sketch, "E1835", {"start": v(11.03, -14.5) * mm, "end": v(11.08, -14.54) * mm});
            skLineSegment(sketch, "E1836", {"start": v(19.58, -17.07) * mm, "end": v(19.52, -17.1) * mm});
            skLineSegment(sketch, "E1837", {"start": v(-26.3, -14.54) * mm, "end": v(-26.25, -14.58) * mm});
            skLineSegment(sketch, "E1838", {"start": v(-29, -16.2) * mm, "end": v(-28.97, -16.27) * mm});
            skLineSegment(sketch, "E1839", {"start": v(49.15, -14.59) * mm, "end": v(49.1, -14.64) * mm});
            skLineSegment(sketch, "E1840", {"start": v(9.54, -17.07) * mm, "end": v(9.47, -17.1) * mm});
            skLineSegment(sketch, "E1841", {"start": v(-15.59, -13.38) * mm, "end": v(-15.59, -13.46) * mm});
            skLineSegment(sketch, "E1842", {"start": v(49.83, -14.58) * mm, "end": v(49.88, -14.63) * mm});
            skLineSegment(sketch, "E1843", {"start": v(-16.94, -16.93) * mm, "end": v(-16.89, -16.99) * mm});
            skLineSegment(sketch, "E1844", {"start": v(-3.03, -16.53) * mm, "end": v(-3.03, -16.6) * mm});
            skLineSegment(sketch, "E1845", {"start": v(10.51, -14.54) * mm, "end": v(10.46, -14.59) * mm});
            skLineSegment(sketch, "E1846", {"start": v(29.12, -16.12) * mm, "end": v(29.07, -16.16) * mm});
            skLineSegment(sketch, "E1847", {"start": v(-26.8, -14.5) * mm, "end": v(-26.87, -14.54) * mm});
            skLineSegment(sketch, "E1848", {"start": v(0.66, -12.89) * mm, "end": v(0.6, -12.9) * mm});
            skLineSegment(sketch, "E1849", {"start": v(29.91, -15.03) * mm, "end": v(29.9, -15.1) * mm});
            skLineSegment(sketch, "E1850", {"start": v(-14.95, -12.89) * mm, "end": v(-14.9, -12.9) * mm});
            skLineSegment(sketch, "E1851", {"start": v(30.59, -15.45) * mm, "end": v(30.64, -15.49) * mm});
            skLineSegment(sketch, "E1852", {"start": v(-27.07, -15.2) * mm, "end": v(-27.06, -15.24) * mm});
            skLineSegment(sketch, "E1853", {"start": v(-16.16, -16.93) * mm, "end": v(-16.21, -16.99) * mm});
            skLineSegment(sketch, "E1854", {"start": v(-46.28, -13.06) * mm, "end": v(-46.24, -13.11) * mm});
            skLineSegment(sketch, "E1855", {"start": v(49.21, -14.54) * mm, "end": v(49.15, -14.59) * mm});
            skLineSegment(sketch, "E1856", {"start": v(0.86, -12.89) * mm, "end": v(0.92, -12.9) * mm});
            skLineSegment(sketch, "E1857", {"start": v(46.22, -16.34) * mm, "end": v(46.2, -16.37) * mm});
            skLineSegment(sketch, "E1858", {"start": v(-18.87, -16.39) * mm, "end": v(-18.85, -16.46) * mm});
            skLineSegment(sketch, "E1859", {"start": v(-1.23, -13.6) * mm, "end": v(-1.2, -13.66) * mm});
            skLineSegment(sketch, "E1860", {"start": v(-0.34, -14.63) * mm, "end": v(-0.3, -14.69) * mm});
            skLineSegment(sketch, "E1861", {"start": v(-16.98, -16.88) * mm, "end": v(-16.94, -16.93) * mm});
            skLineSegment(sketch, "E1862", {"start": v(-49, -16.75) * mm, "end": v(-49.02, -16.82) * mm});
            skLineSegment(sketch, "E1863", {"start": v(-26.6, -14.45) * mm, "end": v(-26.68, -14.46) * mm});
            skLineSegment(sketch, "E1864", {"start": v(-47.17, -13.25) * mm, "end": v(-47.19, -13.31) * mm});
            skLineSegment(sketch, "E1865", {"start": v(-37.02, -13.77) * mm, "end": v(-36.97, -13.83) * mm});
            skLineSegment(sketch, "E1866", {"start": v(-28.97, -16.88) * mm, "end": v(-29.01, -16.94) * mm});
            skLineSegment(sketch, "E1867", {"start": v(9.09, -17.07) * mm, "end": v(9.15, -17.1) * mm});
            skLineSegment(sketch, "E1868", {"start": v(-46.56, -16.03) * mm, "end": v(-46.5, -16.05) * mm});
            skLineSegment(sketch, "E1869", {"start": v(-36.24, -13.06) * mm, "end": v(-36.2, -13.11) * mm});
            skLineSegment(sketch, "E1870", {"start": v(1.03, -13.88) * mm, "end": v(0.97, -13.91) * mm});
            skLineSegment(sketch, "E1871", {"start": v(0.46, -13.87) * mm, "end": v(0.51, -13.9) * mm});
            skLineSegment(sketch, "E1872", {"start": v(-16.76, -16.08) * mm, "end": v(-16.82, -16.12) * mm});
            skLineSegment(sketch, "E1873", {"start": v(-19.82, -16.34) * mm, "end": v(-19.84, -16.4) * mm});
            skLineSegment(sketch, "E1874", {"start": v(20.72, -15.53) * mm, "end": v(20.8, -15.54) * mm});
            skLineSegment(sketch, "E1875", {"start": v(-16.3, -16.08) * mm, "end": v(-16.25, -16.11) * mm});
            skLineSegment(sketch, "E1876", {"start": v(-0.75, -12.88) * mm, "end": v(-0.82, -12.89) * mm});
            skLineSegment(sketch, "E1877", {"start": v(18.86, -14.82) * mm, "end": v(18.84, -14.89) * mm});
            skLineSegment(sketch, "E1878", {"start": v(-1.25, -13.38) * mm, "end": v(-1.25, -13.46) * mm});
            skLineSegment(sketch, "E1879", {"start": v(-3.03, -16.6) * mm, "end": v(-3.03, -16.68) * mm});
            skLineSegment(sketch, "E1880", {"start": v(8.82, -13.6) * mm, "end": v(8.84, -13.66) * mm});
            skLineSegment(sketch, "E1881", {"start": v(-45.6, -13.77) * mm, "end": v(-45.54, -13.83) * mm});
            skLineSegment(sketch, "E1882", {"start": v(-0.22, -13.38) * mm, "end": v(-0.22, -13.45) * mm});
            skLineSegment(sketch, "E1883", {"start": v(20.32, -14.92) * mm, "end": v(20.32, -15) * mm});
            skLineSegment(sketch, "E1884", {"start": v(-0.95, -14.5) * mm, "end": v(-1, -14.54) * mm});
            skLineSegment(sketch, "E1885", {"start": v(-25.25, -13.95) * mm, "end": v(-25.19, -13.96) * mm});
            skLineSegment(sketch, "E1886", {"start": v(-0.5, -14.5) * mm, "end": v(-0.44, -14.54) * mm});
            skLineSegment(sketch, "E1887", {"start": v(29.7, -16.11) * mm, "end": v(29.74, -16.16) * mm});
            skLineSegment(sketch, "E1888", {"start": v(-50, -16.54) * mm, "end": v(-50, -16.62) * mm});
            skLineSegment(sketch, "E1889", {"start": v(-26.47, -14.46) * mm, "end": v(-26.41, -14.48) * mm});
            skLineSegment(sketch, "E1890", {"start": v(-46.19, -13.23) * mm, "end": v(-46.17, -13.3) * mm});
            skLineSegment(sketch, "E1891", {"start": v(-48.97, -16.53) * mm, "end": v(-48.97, -16.6) * mm});
            skLineSegment(sketch, "E1892", {"start": v(-29.79, -16.93) * mm, "end": v(-29.74, -16.99) * mm});
            skLineSegment(sketch, "E1893", {"start": v(-1.17, -16.88) * mm, "end": v(-1.12, -16.93) * mm});
            skLineSegment(sketch, "E1894", {"start": v(-36.23, -13.75) * mm, "end": v(-36.27, -13.8) * mm});
            skLineSegment(sketch, "E1895", {"start": v(9.6, -17.03) * mm, "end": v(9.54, -17.07) * mm});
            skLineSegment(sketch, "E1896", {"start": v(-36.85, -12.93) * mm, "end": v(-36.9, -12.97) * mm});
            skLineSegment(sketch, "E1897", {"start": v(39.83, -13.06) * mm, "end": v(39.88, -13.11) * mm});
            skLineSegment(sketch, "E1898", {"start": v(-36.4, -12.93) * mm, "end": v(-36.34, -12.96) * mm});
            skLineSegment(sketch, "E1899", {"start": v(-39.01, -16.88) * mm, "end": v(-39.05, -16.94) * mm});
            skLineSegment(sketch, "E1900", {"start": v(19.75, -13.06) * mm, "end": v(19.79, -13.11) * mm});
            skLineSegment(sketch, "E1901", {"start": v(30.64, -15.49) * mm, "end": v(30.7, -15.52) * mm});
            skLineSegment(sketch, "E1902", {"start": v(29.3, -17.11) * mm, "end": v(29.36, -17.12) * mm});
            skLineSegment(sketch, "E1903", {"start": v(-16.45, -15.53) * mm, "end": v(-16.51, -15.54) * mm});
            skLineSegment(sketch, "E1904", {"start": v(6.42, -16.04) * mm, "end": v(6.35, -16.06) * mm});
            skLineSegment(sketch, "E1905", {"start": v(18.96, -13.77) * mm, "end": v(19.02, -13.83) * mm});
            skLineSegment(sketch, "E1906", {"start": v(-4.05, -16.54) * mm, "end": v(-4.05, -16.62) * mm});
            skLineSegment(sketch, "E1907", {"start": v(-25.58, -13.18) * mm, "end": v(-25.6, -13.25) * mm});
            skLineSegment(sketch, "E1908", {"start": v(-17.05, -16.72) * mm, "end": v(-17.03, -16.78) * mm});
            skLineSegment(sketch, "E1909", {"start": v(19.25, -17.11) * mm, "end": v(19.32, -17.12) * mm});
            skLineSegment(sketch, "E1910", {"start": v(-24.83, -13.88) * mm, "end": v(-24.89, -13.91) * mm});
            skLineSegment(sketch, "E1911", {"start": v(-25.4, -13.87) * mm, "end": v(-25.34, -13.9) * mm});
            skLineSegment(sketch, "E1912", {"start": v(17.04, -16.75) * mm, "end": v(17.01, -16.82) * mm});
            skLineSegment(sketch, "E1913", {"start": v(29.18, -16.08) * mm, "end": v(29.12, -16.12) * mm});
            skLineSegment(sketch, "E1914", {"start": v(-0.35, -16.93) * mm, "end": v(-0.4, -16.99) * mm});
            skLineSegment(sketch, "E1915", {"start": v(-29.78, -16.22) * mm, "end": v(-29.82, -16.28) * mm});
            skLineSegment(sketch, "E1916", {"start": v(-14.58, -13.23) * mm, "end": v(-14.57, -13.3) * mm});
            skLineSegment(sketch, "E1917", {"start": v(-47.14, -13.18) * mm, "end": v(-47.17, -13.25) * mm});
            skLineSegment(sketch, "E1918", {"start": v(-46.4, -17.03) * mm, "end": v(-46.45, -17.07) * mm});
            skLineSegment(sketch, "E1919", {"start": v(-46.96, -17.03) * mm, "end": v(-46.9, -17.07) * mm});
            skLineSegment(sketch, "E1920", {"start": v(9.79, -16.36) * mm, "end": v(9.8, -16.42) * mm});
            skLineSegment(sketch, "E1921", {"start": v(38.95, -13.25) * mm, "end": v(38.93, -13.31) * mm});
            skLineSegment(sketch, "E1922", {"start": v(19.14, -12.93) * mm, "end": v(19.08, -12.97) * mm});
            skLineSegment(sketch, "E1923", {"start": v(6.62, -16.04) * mm, "end": v(6.68, -16.06) * mm});
            skLineSegment(sketch, "E1924", {"start": v(19.6, -12.93) * mm, "end": v(19.65, -12.96) * mm});
            skLineSegment(sketch, "E1925", {"start": v(31.16, -15.45) * mm, "end": v(31.1, -15.49) * mm});
            skLineSegment(sketch, "E1926", {"start": v(-0.24, -13.6) * mm, "end": v(-0.27, -13.66) * mm});
            skLineSegment(sketch, "E1927", {"start": v(-24.63, -13.23) * mm, "end": v(-24.6, -13.3) * mm});
            skLineSegment(sketch, "E1928", {"start": v(19.76, -13.75) * mm, "end": v(19.72, -13.8) * mm});
            skLineSegment(sketch, "E1929", {"start": v(-1.12, -14.64) * mm, "end": v(-1.16, -14.7) * mm});
            skLineSegment(sketch, "E1930", {"start": v(-3.65, -17.11) * mm, "end": v(-3.58, -17.12) * mm});
            skLineSegment(sketch, "E1931", {"start": v(18.89, -16.34) * mm, "end": v(18.86, -16.4) * mm});
            skLineSegment(sketch, "E1932", {"start": v(49.87, -15.36) * mm, "end": v(49.82, -15.41) * mm});
            skLineSegment(sketch, "E1933", {"start": v(-26.1, -16.75) * mm, "end": v(-26.13, -16.82) * mm});
            skLineSegment(sketch, "E1934", {"start": v(19.64, -17.03) * mm, "end": v(19.58, -17.07) * mm});
            skLineSegment(sketch, "E1935", {"start": v(-49.97, -16.75) * mm, "end": v(-49.95, -16.82) * mm});
            skLineSegment(sketch, "E1936", {"start": v(19.07, -17.03) * mm, "end": v(19.13, -17.07) * mm});
            skLineSegment(sketch, "E1937", {"start": v(26.2, -16.93) * mm, "end": v(26.25, -16.99) * mm});
            skLineSegment(sketch, "E1938", {"start": v(17.06, -16.53) * mm, "end": v(17.06, -16.6) * mm});
            skLineSegment(sketch, "E1939", {"start": v(16.53, -16.03) * mm, "end": v(16.46, -16.04) * mm});
            skLineSegment(sketch, "E1940", {"start": v(-0.62, -12.89) * mm, "end": v(-0.55, -12.9) * mm});
            skLineSegment(sketch, "E1941", {"start": v(-37.02, -13.07) * mm, "end": v(-37.06, -13.12) * mm});
            skLineSegment(sketch, "E1942", {"start": v(39.93, -13.23) * mm, "end": v(39.95, -13.3) * mm});
            skLineSegment(sketch, "E1943", {"start": v(-18.96, -16.2) * mm, "end": v(-18.92, -16.27) * mm});
            skLineSegment(sketch, "E1944", {"start": v(31.27, -13.06) * mm, "end": v(31.3, -13.11) * mm});
            skLineSegment(sketch, "E1945", {"start": v(6.49, -16.03) * mm, "end": v(6.42, -16.04) * mm});
            skLineSegment(sketch, "E1946", {"start": v(49, -13.6) * mm, "end": v(49.02, -13.66) * mm});
            skLineSegment(sketch, "E1947", {"start": v(-4, -16.34) * mm, "end": v(-4.03, -16.4) * mm});
            skLineSegment(sketch, "E1948", {"start": v(19.83, -16.36) * mm, "end": v(19.85, -16.42) * mm});
            skLineSegment(sketch, "E1949", {"start": v(-44.71, -13.6) * mm, "end": v(-44.74, -13.66) * mm});
            skLineSegment(sketch, "E1950", {"start": v(-26.1, -15.17) * mm, "end": v(-26.13, -15.24) * mm});
            skLineSegment(sketch, "E1951", {"start": v(21.34, -14.96) * mm, "end": v(21.34, -15.03) * mm});
            skLineSegment(sketch, "E1952", {"start": v(49.1, -15.35) * mm, "end": v(49.15, -15.4) * mm});
            skLineSegment(sketch, "E1953", {"start": v(10.77, -14.45) * mm, "end": v(10.7, -14.46) * mm});
            skLineSegment(sketch, "E1954", {"start": v(-39.83, -16.93) * mm, "end": v(-39.78, -16.99) * mm});
            skLineSegment(sketch, "E1955", {"start": v(-24.98, -13.95) * mm, "end": v(-25.05, -13.96) * mm});
            skLineSegment(sketch, "E1956", {"start": v(36.75, -16.04) * mm, "end": v(36.81, -16.06) * mm});
            skLineSegment(sketch, "E1957", {"start": v(-49.6, -17.11) * mm, "end": v(-49.53, -17.12) * mm});
            skLineSegment(sketch, "E1958", {"start": v(16.66, -16.04) * mm, "end": v(16.73, -16.06) * mm});
            skLineSegment(sketch, "E1959", {"start": v(-47.06, -13.07) * mm, "end": v(-47.1, -13.12) * mm});
            skLineSegment(sketch, "E1960", {"start": v(-27.09, -16.75) * mm, "end": v(-27.06, -16.82) * mm});
            skLineSegment(sketch, "E1961", {"start": v(49.88, -14.63) * mm, "end": v(49.92, -14.69) * mm});
            skLineSegment(sketch, "E1962", {"start": v(46.57, -17.11) * mm, "end": v(46.64, -17.12) * mm});
            skLineSegment(sketch, "E1963", {"start": v(38.98, -13.18) * mm, "end": v(38.95, -13.25) * mm});
            skLineSegment(sketch, "E1964", {"start": v(28.93, -14.76) * mm, "end": v(28.9, -14.82) * mm});
            skLineSegment(sketch, "E1965", {"start": v(18.97, -13.07) * mm, "end": v(18.92, -13.12) * mm});
            skLineSegment(sketch, "E1966", {"start": v(-19.74, -16.22) * mm, "end": v(-19.78, -16.28) * mm});
            skLineSegment(sketch, "E1967", {"start": v(31.3, -15.3) * mm, "end": v(31.26, -15.36) * mm});
            skLineSegment(sketch, "E1968", {"start": v(-3.05, -16.39) * mm, "end": v(-3.03, -16.46) * mm});
            skLineSegment(sketch, "E1969", {"start": v(48.96, -13.38) * mm, "end": v(48.96, -13.46) * mm});
            skLineSegment(sketch, "E1970", {"start": v(50, -13.38) * mm, "end": v(50, -13.45) * mm});
            skLineSegment(sketch, "E1971", {"start": v(10.9, -14.46) * mm, "end": v(10.97, -14.48) * mm});
            skLineSegment(sketch, "E1972", {"start": v(-28.93, -16.33) * mm, "end": v(-28.9, -16.39) * mm});
            skLineSegment(sketch, "E1973", {"start": v(19.46, -17.11) * mm, "end": v(19.39, -17.12) * mm});
            skLineSegment(sketch, "E1974", {"start": v(36.92, -17.03) * mm, "end": v(36.86, -17.07) * mm});
            skLineSegment(sketch, "E1975", {"start": v(16.05, -16.72) * mm, "end": v(16.07, -16.79) * mm});
            skLineSegment(sketch, "E1976", {"start": v(36.35, -17.03) * mm, "end": v(36.4, -17.07) * mm});
            skLineSegment(sketch, "E1977", {"start": v(49.05, -16.88) * mm, "end": v(49.1, -16.93) * mm});
            skLineSegment(sketch, "E1978", {"start": v(49.27, -14.5) * mm, "end": v(49.21, -14.54) * mm});
            skLineSegment(sketch, "E1979", {"start": v(0.8, -12.88) * mm, "end": v(0.86, -12.89) * mm});
            skLineSegment(sketch, "E1980", {"start": v(-49.39, -17.11) * mm, "end": v(-49.46, -17.12) * mm});
            skLineSegment(sketch, "E1981", {"start": v(49.72, -14.5) * mm, "end": v(49.78, -14.54) * mm});
            skLineSegment(sketch, "E1982", {"start": v(46.96, -17.03) * mm, "end": v(46.9, -17.07) * mm});
            skLineSegment(sketch, "E1983", {"start": v(8.93, -16.22) * mm, "end": v(8.88, -16.28) * mm});
            skLineSegment(sketch, "E1984", {"start": v(46.4, -17.03) * mm, "end": v(46.45, -17.07) * mm});
            skLineSegment(sketch, "E1985", {"start": v(29.89, -14.81) * mm, "end": v(29.9, -14.88) * mm});
            skLineSegment(sketch, "E1986", {"start": v(46.2, -16.37) * mm, "end": v(46.18, -16.44) * mm});
            skLineSegment(sketch, "E1987", {"start": v(-15.56, -13.25) * mm, "end": v(-15.58, -13.31) * mm});
            skLineSegment(sketch, "E1988", {"start": v(30.49, -15.35) * mm, "end": v(30.53, -15.4) * mm});
            skLineSegment(sketch, "E1989", {"start": v(28.88, -14.96) * mm, "end": v(28.88, -15.03) * mm});
            skLineSegment(sketch, "E1990", {"start": v(29.91, -14.96) * mm, "end": v(29.91, -15.03) * mm});
            skLineSegment(sketch, "E1991", {"start": v(18.86, -13.6) * mm, "end": v(18.89, -13.66) * mm});
            skLineSegment(sketch, "E1992", {"start": v(20.93, -15.53) * mm, "end": v(20.86, -15.54) * mm});
            skLineSegment(sketch, "E1993", {"start": v(9.8, -13.6) * mm, "end": v(9.77, -13.66) * mm});
            skLineSegment(sketch, "E1994", {"start": v(-3.44, -17.11) * mm, "end": v(-3.5, -17.12) * mm});
            skLineSegment(sketch, "E1995", {"start": v(-16.76, -14.5) * mm, "end": v(-16.82, -14.54) * mm});
            skLineSegment(sketch, "E1996", {"start": v(-37.07, -13.72) * mm, "end": v(-37.02, -13.77) * mm});
            skLineSegment(sketch, "E1997", {"start": v(26.1, -16.75) * mm, "end": v(26.13, -16.82) * mm});
            skLineSegment(sketch, "E1998", {"start": v(47.17, -16.39) * mm, "end": v(47.18, -16.46) * mm});
            skLineSegment(sketch, "E1999", {"start": v(0.73, -12.88) * mm, "end": v(0.66, -12.89) * mm});
            skLineSegment(sketch, "E2000", {"start": v(39.06, -13.07) * mm, "end": v(39.01, -13.12) * mm});
            skLineSegment(sketch, "E2001", {"start": v(0.73, -12.88) * mm, "end": v(0.8, -12.88) * mm});
            skLineSegment(sketch, "E2002", {"start": v(29.5, -17.11) * mm, "end": v(29.43, -17.12) * mm});
            skLineSegment(sketch, "E2003", {"start": v(29.52, -16.03) * mm, "end": v(29.58, -16.05) * mm});
            skLineSegment(sketch, "E2004", {"start": v(-17.07, -15) * mm, "end": v(-17.06, -15.07) * mm});
            skLineSegment(sketch, "E2005", {"start": v(-0.82, -12.89) * mm, "end": v(-0.88, -12.9) * mm});
            skLineSegment(sketch, "E2006", {"start": v(-27.1, -15.07) * mm, "end": v(-27.1, -15.14) * mm});
            skLineSegment(sketch, "E2007", {"start": v(30.5, -13.07) * mm, "end": v(30.45, -13.12) * mm});
            skLineSegment(sketch, "E2008", {"start": v(10.68, -15.53) * mm, "end": v(10.75, -15.54) * mm});
            skLineSegment(sketch, "E2009", {"start": v(49.97, -13.6) * mm, "end": v(49.95, -13.66) * mm});
            skLineSegment(sketch, "E2010", {"start": v(19.84, -13.6) * mm, "end": v(19.82, -13.66) * mm});
            skLineSegment(sketch, "E2011", {"start": v(-0.45, -17.03) * mm, "end": v(-0.5, -17.07) * mm});
            skLineSegment(sketch, "E2012", {"start": v(49.1, -14.64) * mm, "end": v(49.06, -14.7) * mm});
            skLineSegment(sketch, "E2013", {"start": v(46.78, -17.11) * mm, "end": v(46.7, -17.12) * mm});
            skLineSegment(sketch, "E2014", {"start": v(-39.05, -16.94) * mm, "end": v(-39.1, -17) * mm});
            skLineSegment(sketch, "E2015", {"start": v(-16.25, -16.11) * mm, "end": v(-16.2, -16.16) * mm});
            skLineSegment(sketch, "E2016", {"start": v(31.27, -14.63) * mm, "end": v(31.3, -14.69) * mm});
            skLineSegment(sketch, "E2017", {"start": v(19.83, -14.78) * mm, "end": v(19.85, -14.85) * mm});
            skLineSegment(sketch, "E2018", {"start": v(20.32, -15.07) * mm, "end": v(20.33, -15.14) * mm});
            skLineSegment(sketch, "E2019", {"start": v(19.85, -16.42) * mm, "end": v(19.87, -16.5) * mm});
            skLineSegment(sketch, "E2020", {"start": v(-25.63, -13.38) * mm, "end": v(-25.63, -13.46) * mm});
            skLineSegment(sketch, "E2021", {"start": v(49.38, -13.95) * mm, "end": v(49.45, -13.96) * mm});
            skLineSegment(sketch, "E2022", {"start": v(10.89, -15.53) * mm, "end": v(10.82, -15.54) * mm});
            skLineSegment(sketch, "E2023", {"start": v(0.88, -13.95) * mm, "end": v(0.8, -13.96) * mm});
            skLineSegment(sketch, "E2024", {"start": v(-14.56, -13.38) * mm, "end": v(-14.56, -13.45) * mm});
            skLineSegment(sketch, "E2025", {"start": v(-16.88, -16.16) * mm, "end": v(-16.93, -16.22) * mm});
            skLineSegment(sketch, "E2026", {"start": v(8.88, -13.72) * mm, "end": v(8.92, -13.77) * mm});
            skLineSegment(sketch, "E2027", {"start": v(30.5, -14.64) * mm, "end": v(30.45, -14.7) * mm});
            skLineSegment(sketch, "E2028", {"start": v(-27.11, -15) * mm, "end": v(-27.1, -15.07) * mm});
            skLineSegment(sketch, "E2029", {"start": v(19.82, -13.66) * mm, "end": v(19.8, -13.7) * mm});
            skLineSegment(sketch, "E2030", {"start": v(0.6, -13.95) * mm, "end": v(0.67, -13.96) * mm});
            skLineSegment(sketch, "E2031", {"start": v(18.86, -16.4) * mm, "end": v(18.84, -16.47) * mm});
            skLineSegment(sketch, "E2032", {"start": v(-16.3, -14.5) * mm, "end": v(-16.25, -14.54) * mm});
            skLineSegment(sketch, "E2033", {"start": v(49.59, -13.95) * mm, "end": v(49.52, -13.96) * mm});
            skLineSegment(sketch, "E2034", {"start": v(-16.2, -16.16) * mm, "end": v(-16.15, -16.2) * mm});
            skLineSegment(sketch, "E2035", {"start": v(-46.9, -17.07) * mm, "end": v(-46.84, -17.1) * mm});
            skLineSegment(sketch, "E2036", {"start": v(16.33, -16.09) * mm, "end": v(16.27, -16.12) * mm});
            skLineSegment(sketch, "E2037", {"start": v(-0.77, -13.96) * mm, "end": v(-0.7, -13.96) * mm});
            skLineSegment(sketch, "E2038", {"start": v(29.45, -14.45) * mm, "end": v(29.52, -14.46) * mm});
            skLineSegment(sketch, "E2039", {"start": v(-0.5, -12.93) * mm, "end": v(-0.44, -12.96) * mm});
            skLineSegment(sketch, "E2040", {"start": v(20.32, -15) * mm, "end": v(20.32, -15.07) * mm});
            skLineSegment(sketch, "E2041", {"start": v(49.05, -15.3) * mm, "end": v(49.1, -15.35) * mm});
            skLineSegment(sketch, "E2042", {"start": v(-26.09, -15.1) * mm, "end": v(-26.1, -15.17) * mm});
            skLineSegment(sketch, "E2043", {"start": v(29.31, -16.03) * mm, "end": v(29.25, -16.05) * mm});
            skLineSegment(sketch, "E2044", {"start": v(-1.02, -17.03) * mm, "end": v(-0.96, -17.07) * mm});
            skLineSegment(sketch, "E2045", {"start": v(-29.86, -16.34) * mm, "end": v(-29.89, -16.4) * mm});
            skLineSegment(sketch, "E2046", {"start": v(-1.12, -16.93) * mm, "end": v(-1.07, -16.99) * mm});
            skLineSegment(sketch, "E2047", {"start": v(-46.37, -13.86) * mm, "end": v(-46.42, -13.9) * mm});
            skLineSegment(sketch, "E2048", {"start": v(-46.51, -17.1) * mm, "end": v(-46.58, -17.11) * mm});
            skLineSegment(sketch, "E2049", {"start": v(-49.53, -17.12) * mm, "end": v(-49.46, -17.12) * mm});
            skLineSegment(sketch, "E2050", {"start": v(-39.73, -17.03) * mm, "end": v(-39.67, -17.07) * mm});
            skLineSegment(sketch, "E2051", {"start": v(-27.1, -15.14) * mm, "end": v(-27.07, -15.2) * mm});
            skLineSegment(sketch, "E2052", {"start": v(29.38, -14.45) * mm, "end": v(29.31, -14.46) * mm});
            skLineSegment(sketch, "E2053", {"start": v(-15.02, -12.88) * mm, "end": v(-14.95, -12.89) * mm});
            skLineSegment(sketch, "E2054", {"start": v(-16.82, -16.12) * mm, "end": v(-16.88, -16.16) * mm});
            skLineSegment(sketch, "E2055", {"start": v(29.38, -14.45) * mm, "end": v(29.45, -14.45) * mm});
            skLineSegment(sketch, "E2056", {"start": v(-0.3, -15.3) * mm, "end": v(-0.35, -15.36) * mm});
            skLineSegment(sketch, "E2057", {"start": v(-46.84, -17.1) * mm, "end": v(-46.78, -17.11) * mm});
            skLineSegment(sketch, "E2058", {"start": v(-24.6, -13.38) * mm, "end": v(-24.6, -13.45) * mm});
            skLineSegment(sketch, "E2059", {"start": v(21.34, -15.1) * mm, "end": v(21.32, -15.17) * mm});
            skLineSegment(sketch, "E2060", {"start": v(-26.25, -16.16) * mm, "end": v(-26.2, -16.2) * mm});
            skLineSegment(sketch, "E2061", {"start": v(-3.77, -17.07) * mm, "end": v(-3.7, -17.1) * mm});
            skLineSegment(sketch, "E2062", {"start": v(-26.16, -16.88) * mm, "end": v(-26.2, -16.93) * mm});
            skLineSegment(sketch, "E2063", {"start": v(-46.96, -13.87) * mm, "end": v(-46.9, -13.9) * mm});
            skLineSegment(sketch, "E2064", {"start": v(-36.19, -13.7) * mm, "end": v(-36.23, -13.75) * mm});
            skLineSegment(sketch, "E2065", {"start": v(0.57, -13.94) * mm, "end": v(0.6, -13.95) * mm});
            skLineSegment(sketch, "E2066", {"start": v(20.33, -15.14) * mm, "end": v(20.35, -15.2) * mm});
            skLineSegment(sketch, "E2067", {"start": v(-39.9, -16.34) * mm, "end": v(-39.93, -16.4) * mm});
            skLineSegment(sketch, "E2068", {"start": v(-18.89, -16.33) * mm, "end": v(-18.87, -16.39) * mm});
            skLineSegment(sketch, "E2069", {"start": v(31.17, -12.96) * mm, "end": v(31.22, -13) * mm});
            skLineSegment(sketch, "E2070", {"start": v(19.79, -14.69) * mm, "end": v(19.8, -14.72) * mm});
            skLineSegment(sketch, "E2071", {"start": v(-1.17, -15.3) * mm, "end": v(-1.12, -15.35) * mm});
            skLineSegment(sketch, "E2072", {"start": v(-16.03, -15.03) * mm, "end": v(-16.04, -15.1) * mm});
            skLineSegment(sketch, "E2073", {"start": v(6, -16.5) * mm, "end": v(5.99, -16.58) * mm});
            skLineSegment(sketch, "E2074", {"start": v(-0.39, -14.58) * mm, "end": v(-0.34, -14.63) * mm});
            skLineSegment(sketch, "E2075", {"start": v(-44.77, -13.72) * mm, "end": v(-44.81, -13.78) * mm});
            skLineSegment(sketch, "E2076", {"start": v(-26.08, -15.03) * mm, "end": v(-26.09, -15.1) * mm});
            skLineSegment(sketch, "E2077", {"start": v(-26.87, -16.12) * mm, "end": v(-26.92, -16.16) * mm});
            skLineSegment(sketch, "E2078", {"start": v(-3.37, -17.1) * mm, "end": v(-3.44, -17.11) * mm});
            skLineSegment(sketch, "E2079", {"start": v(-48.98, -16.68) * mm, "end": v(-49, -16.75) * mm});
            skLineSegment(sketch, "E2080", {"start": v(-24.89, -13.91) * mm, "end": v(-24.92, -13.92) * mm});
            skLineSegment(sketch, "E2081", {"start": v(-16.63, -14.46) * mm, "end": v(-16.7, -14.48) * mm});
            skLineSegment(sketch, "E2082", {"start": v(36.4, -17.07) * mm, "end": v(36.46, -17.1) * mm});
            skLineSegment(sketch, "E2083", {"start": v(16.79, -16.08) * mm, "end": v(16.84, -16.12) * mm});
            skLineSegment(sketch, "E2084", {"start": v(-27.06, -16.82) * mm, "end": v(-27.02, -16.88) * mm});
            skLineSegment(sketch, "E2085", {"start": v(-29.01, -16.94) * mm, "end": v(-29.06, -17) * mm});
            skLineSegment(sketch, "E2086", {"start": v(10.29, -15.14) * mm, "end": v(10.3, -15.2) * mm});
            skLineSegment(sketch, "E2087", {"start": v(9.03, -17.03) * mm, "end": v(9.09, -17.07) * mm});
            skLineSegment(sketch, "E2088", {"start": v(-46.45, -17.07) * mm, "end": v(-46.51, -17.1) * mm});
            skLineSegment(sketch, "E2089", {"start": v(-46.63, -16.03) * mm, "end": v(-46.56, -16.03) * mm});
            skLineSegment(sketch, "E2090", {"start": v(8.92, -16.93) * mm, "end": v(8.97, -16.99) * mm});
            skLineSegment(sketch, "E2091", {"start": v(39.75, -13.86) * mm, "end": v(39.7, -13.9) * mm});
            skLineSegment(sketch, "E2092", {"start": v(-38.98, -16.33) * mm, "end": v(-38.95, -16.39) * mm});
            skLineSegment(sketch, "E2093", {"start": v(-3.7, -17.1) * mm, "end": v(-3.65, -17.11) * mm});
            skLineSegment(sketch, "E2094", {"start": v(-17.06, -15.07) * mm, "end": v(-17.05, -15.14) * mm});
            skLineSegment(sketch, "E2095", {"start": v(-19.78, -16.28) * mm, "end": v(-19.82, -16.34) * mm});
            skLineSegment(sketch, "E2096", {"start": v(7.02, -16.53) * mm, "end": v(7.02, -16.6) * mm});
            skLineSegment(sketch, "E2097", {"start": v(30.54, -13.01) * mm, "end": v(30.5, -13.07) * mm});
            skLineSegment(sketch, "E2098", {"start": v(18.89, -14.76) * mm, "end": v(18.86, -14.82) * mm});
            skLineSegment(sketch, "E2099", {"start": v(-45.63, -13.72) * mm, "end": v(-45.6, -13.77) * mm});
            skLineSegment(sketch, "E2100", {"start": v(21.34, -15.03) * mm, "end": v(21.34, -15.1) * mm});
            skLineSegment(sketch, "E2101", {"start": v(-1, -14.54) * mm, "end": v(-1.06, -14.59) * mm});
            skLineSegment(sketch, "E2102", {"start": v(10.75, -15.54) * mm, "end": v(10.82, -15.54) * mm});
            skLineSegment(sketch, "E2103", {"start": v(9.7, -16.93) * mm, "end": v(9.65, -16.99) * mm});
            skLineSegment(sketch, "E2104", {"start": v(-25.28, -13.94) * mm, "end": v(-25.25, -13.95) * mm});
            skLineSegment(sketch, "E2105", {"start": v(29.64, -16.08) * mm, "end": v(29.7, -16.11) * mm});
            skLineSegment(sketch, "E2106", {"start": v(-50, -16.62) * mm, "end": v(-50, -16.69) * mm});
            skLineSegment(sketch, "E2107", {"start": v(36.8, -17.1) * mm, "end": v(36.73, -17.11) * mm});
            skLineSegment(sketch, "E2108", {"start": v(0.51, -13.9) * mm, "end": v(0.57, -13.94) * mm});
            skLineSegment(sketch, "E2109", {"start": v(16.03, -16.58) * mm, "end": v(16.04, -16.65) * mm});
            skLineSegment(sketch, "E2110", {"start": v(31.22, -13) * mm, "end": v(31.27, -13.06) * mm});
            skLineSegment(sketch, "E2111", {"start": v(39.16, -13.87) * mm, "end": v(39.22, -13.9) * mm});
            skLineSegment(sketch, "E2112", {"start": v(-44.86, -13) * mm, "end": v(-44.8, -13.06) * mm});
            skLineSegment(sketch, "E2113", {"start": v(-49.57, -16.04) * mm, "end": v(-49.64, -16.06) * mm});
            skLineSegment(sketch, "E2114", {"start": v(8.84, -16.34) * mm, "end": v(8.82, -16.4) * mm});
            skLineSegment(sketch, "E2115", {"start": v(46.17, -16.5) * mm, "end": v(46.16, -16.58) * mm});
            skLineSegment(sketch, "E2116", {"start": v(19.7, -13) * mm, "end": v(19.75, -13.06) * mm});
            skLineSegment(sketch, "E2117", {"start": v(-39.87, -16.28) * mm, "end": v(-39.9, -16.34) * mm});
            skLineSegment(sketch, "E2118", {"start": v(29.36, -17.12) * mm, "end": v(29.43, -17.12) * mm});
            skLineSegment(sketch, "E2119", {"start": v(-15.09, -12.88) * mm, "end": v(-15.16, -12.89) * mm});
            skLineSegment(sketch, "E2120", {"start": v(36.46, -17.1) * mm, "end": v(36.53, -17.11) * mm});
            skLineSegment(sketch, "E2121", {"start": v(-15.09, -12.88) * mm, "end": v(-15.02, -12.88) * mm});
            skLineSegment(sketch, "E2122", {"start": v(-0.44, -14.54) * mm, "end": v(-0.39, -14.58) * mm});
            skLineSegment(sketch, "E2123", {"start": v(-16.04, -15.1) * mm, "end": v(-16.06, -15.17) * mm});
            skLineSegment(sketch, "E2124", {"start": v(18.92, -13.72) * mm, "end": v(18.96, -13.77) * mm});
            skLineSegment(sketch, "E2125", {"start": v(-48.97, -16.6) * mm, "end": v(-48.98, -16.68) * mm});
            skLineSegment(sketch, "E2126", {"start": v(9.76, -13.7) * mm, "end": v(9.72, -13.75) * mm});
            skLineSegment(sketch, "E2127", {"start": v(-44.74, -13.66) * mm, "end": v(-44.77, -13.72) * mm});
            skLineSegment(sketch, "E2128", {"start": v(-25.6, -13.25) * mm, "end": v(-25.62, -13.31) * mm});
            skLineSegment(sketch, "E2129", {"start": v(-26.92, -16.16) * mm, "end": v(-26.98, -16.22) * mm});
            skLineSegment(sketch, "E2130", {"start": v(-17.02, -16.82) * mm, "end": v(-16.98, -16.88) * mm});
            skLineSegment(sketch, "E2131", {"start": v(-3.31, -17.07) * mm, "end": v(-3.37, -17.1) * mm});
            skLineSegment(sketch, "E2132", {"start": v(19.4, -16.03) * mm, "end": v(19.47, -16.03) * mm});
            skLineSegment(sketch, "E2133", {"start": v(49.45, -13.96) * mm, "end": v(49.52, -13.96) * mm});
            skLineSegment(sketch, "E2134", {"start": v(17.05, -16.68) * mm, "end": v(17.04, -16.75) * mm});
            skLineSegment(sketch, "E2135", {"start": v(-29.82, -16.28) * mm, "end": v(-29.86, -16.34) * mm});
            skLineSegment(sketch, "E2136", {"start": v(49.2, -17.03) * mm, "end": v(49.26, -17.07) * mm});
            skLineSegment(sketch, "E2137", {"start": v(27.02, -16.88) * mm, "end": v(26.98, -16.94) * mm});
            skLineSegment(sketch, "E2138", {"start": v(49.1, -16.93) * mm, "end": v(49.15, -16.99) * mm});
            skLineSegment(sketch, "E2139", {"start": v(0.94, -13.92) * mm, "end": v(0.88, -13.95) * mm});
            skLineSegment(sketch, "E2140", {"start": v(-45.48, -12.97) * mm, "end": v(-45.53, -13.01) * mm});
            skLineSegment(sketch, "E2141", {"start": v(-14.57, -13.3) * mm, "end": v(-14.56, -13.38) * mm});
            skLineSegment(sketch, "E2142", {"start": v(47.2, -16.53) * mm, "end": v(47.2, -16.6) * mm});
            skLineSegment(sketch, "E2143", {"start": v(6.33, -17.1) * mm, "end": v(6.4, -17.11) * mm});
            skLineSegment(sketch, "E2144", {"start": v(19.08, -12.97) * mm, "end": v(19.02, -13.01) * mm});
            skLineSegment(sketch, "E2145", {"start": v(19.74, -15.36) * mm, "end": v(19.7, -15.41) * mm});
            skLineSegment(sketch, "E2146", {"start": v(30.6, -12.97) * mm, "end": v(30.54, -13.01) * mm});
            skLineSegment(sketch, "E2147", {"start": v(49.87, -16.93) * mm, "end": v(49.82, -16.99) * mm});
            skLineSegment(sketch, "E2148", {"start": v(-25.34, -13.9) * mm, "end": v(-25.28, -13.94) * mm});
            skLineSegment(sketch, "E2149", {"start": v(-16.37, -14.48) * mm, "end": v(-16.3, -14.5) * mm});
            skLineSegment(sketch, "E2150", {"start": v(19.8, -13.7) * mm, "end": v(19.76, -13.75) * mm});
            skLineSegment(sketch, "E2151", {"start": v(-1.06, -14.59) * mm, "end": v(-1.12, -14.64) * mm});
            skLineSegment(sketch, "E2152", {"start": v(-3.49, -16.03) * mm, "end": v(-3.42, -16.04) * mm});
            skLineSegment(sketch, "E2153", {"start": v(-26.41, -14.48) * mm, "end": v(-26.35, -14.5) * mm});
            skLineSegment(sketch, "E2154", {"start": v(-16.08, -16.82) * mm, "end": v(-16.12, -16.88) * mm});
            skLineSegment(sketch, "E2155", {"start": v(49.91, -15.3) * mm, "end": v(49.87, -15.36) * mm});
            skLineSegment(sketch, "E2156", {"start": v(-29.74, -16.99) * mm, "end": v(-29.68, -17.03) * mm});
            skLineSegment(sketch, "E2157", {"start": v(-50, -16.69) * mm, "end": v(-49.97, -16.75) * mm});
            skLineSegment(sketch, "E2158", {"start": v(26.16, -16.88) * mm, "end": v(26.2, -16.93) * mm});
            skLineSegment(sketch, "E2159", {"start": v(36.86, -17.07) * mm, "end": v(36.8, -17.1) * mm});
            skLineSegment(sketch, "E2160", {"start": v(-44.9, -12.96) * mm, "end": v(-44.86, -13) * mm});
            skLineSegment(sketch, "E2161", {"start": v(-28.97, -16.27) * mm, "end": v(-28.93, -16.33) * mm});
            skLineSegment(sketch, "E2162", {"start": v(26.94, -16.16) * mm, "end": v(26.98, -16.2) * mm});
            skLineSegment(sketch, "E2163", {"start": v(16.46, -16.04) * mm, "end": v(16.4, -16.06) * mm});
            skLineSegment(sketch, "E2164", {"start": v(-36.17, -13.66) * mm, "end": v(-36.19, -13.7) * mm});
            skLineSegment(sketch, "E2165", {"start": v(-46.7, -16.03) * mm, "end": v(-46.76, -16.03) * mm});
            skLineSegment(sketch, "E2166", {"start": v(-26.13, -16.82) * mm, "end": v(-26.16, -16.88) * mm});
            skLineSegment(sketch, "E2167", {"start": v(49.02, -16.34) * mm, "end": v(49, -16.4) * mm});
            skLineSegment(sketch, "E2168", {"start": v(-19.7, -16.99) * mm, "end": v(-19.64, -17.03) * mm});
            skLineSegment(sketch, "E2169", {"start": v(-46.7, -16.03) * mm, "end": v(-46.63, -16.03) * mm});
            skLineSegment(sketch, "E2170", {"start": v(19.65, -12.96) * mm, "end": v(19.7, -13) * mm});
            skLineSegment(sketch, "E2171", {"start": v(29.23, -15.52) * mm, "end": v(29.3, -15.53) * mm});
            skLineSegment(sketch, "E2172", {"start": v(1.25, -13.3) * mm, "end": v(1.26, -13.38) * mm});
            skLineSegment(sketch, "E2173", {"start": v(8.88, -16.28) * mm, "end": v(8.84, -16.34) * mm});
            skLineSegment(sketch, "E2174", {"start": v(-0.55, -12.9) * mm, "end": v(-0.5, -12.93) * mm});
            skLineSegment(sketch, "E2175", {"start": v(6.73, -17.07) * mm, "end": v(6.67, -17.1) * mm});
            skLineSegment(sketch, "E2176", {"start": v(-18.92, -16.27) * mm, "end": v(-18.89, -16.33) * mm});
            skLineSegment(sketch, "E2177", {"start": v(31.34, -14.75) * mm, "end": v(31.36, -14.81) * mm});
            skLineSegment(sketch, "E2178", {"start": v(11.3, -15.03) * mm, "end": v(11.3, -15.1) * mm});
            skLineSegment(sketch, "E2179", {"start": v(-1.2, -15.24) * mm, "end": v(-1.17, -15.3) * mm});
            skLineSegment(sketch, "E2180", {"start": v(17.06, -16.6) * mm, "end": v(17.05, -16.68) * mm});
            skLineSegment(sketch, "E2181", {"start": v(-1.07, -16.99) * mm, "end": v(-1.02, -17.03) * mm});
            skLineSegment(sketch, "E2182", {"start": v(10.7, -14.46) * mm, "end": v(10.64, -14.48) * mm});
            skLineSegment(sketch, "E2183", {"start": v(-24.92, -13.92) * mm, "end": v(-24.98, -13.95) * mm});
            skLineSegment(sketch, "E2184", {"start": v(36.69, -16.03) * mm, "end": v(36.75, -16.04) * mm});
            skLineSegment(sketch, "E2185", {"start": v(-49.3, -16.06) * mm, "end": v(-49.25, -16.08) * mm});
            skLineSegment(sketch, "E2186", {"start": v(27.05, -16.82) * mm, "end": v(27.02, -16.88) * mm});
            skLineSegment(sketch, "E2187", {"start": v(-47.1, -13.12) * mm, "end": v(-47.14, -13.18) * mm});
            skLineSegment(sketch, "E2188", {"start": v(-39.78, -16.99) * mm, "end": v(-39.73, -17.03) * mm});
            skLineSegment(sketch, "E2189", {"start": v(26.32, -16.12) * mm, "end": v(26.26, -16.17) * mm});
            skLineSegment(sketch, "E2190", {"start": v(-37.1, -13.66) * mm, "end": v(-37.07, -13.72) * mm});
            skLineSegment(sketch, "E2191", {"start": v(6.27, -17.07) * mm, "end": v(6.33, -17.1) * mm});
            skLineSegment(sketch, "E2192", {"start": v(46.5, -17.1) * mm, "end": v(46.57, -17.11) * mm});
            skLineSegment(sketch, "E2193", {"start": v(-45.53, -13.01) * mm, "end": v(-45.58, -13.07) * mm});
            skLineSegment(sketch, "E2194", {"start": v(29.62, -15.49) * mm, "end": v(29.56, -15.52) * mm});
            skLineSegment(sketch, "E2195", {"start": v(10.28, -15.07) * mm, "end": v(10.29, -15.14) * mm});
            skLineSegment(sketch, "E2196", {"start": v(28.9, -14.82) * mm, "end": v(28.89, -14.89) * mm});
            skLineSegment(sketch, "E2197", {"start": v(19.02, -13.01) * mm, "end": v(18.97, -13.07) * mm});
            skLineSegment(sketch, "E2198", {"start": v(-39, -16.27) * mm, "end": v(-38.98, -16.33) * mm});
            skLineSegment(sketch, "E2199", {"start": v(-24.6, -13.3) * mm, "end": v(-24.6, -13.38) * mm});
            skLineSegment(sketch, "E2200", {"start": v(30.45, -14.7) * mm, "end": v(30.41, -14.76) * mm});
            skLineSegment(sketch, "E2201", {"start": v(18.92, -14.7) * mm, "end": v(18.89, -14.76) * mm});
            skLineSegment(sketch, "E2202", {"start": v(50, -13.53) * mm, "end": v(49.97, -13.6) * mm});
            skLineSegment(sketch, "E2203", {"start": v(48.96, -13.46) * mm, "end": v(48.97, -13.53) * mm});
            skLineSegment(sketch, "E2204", {"start": v(49.4, -12.89) * mm, "end": v(49.33, -12.9) * mm});
            skLineSegment(sketch, "E2205", {"start": v(-45.67, -13.66) * mm, "end": v(-45.63, -13.72) * mm});
            skLineSegment(sketch, "E2206", {"start": v(19.34, -16.03) * mm, "end": v(19.27, -16.03) * mm});
            skLineSegment(sketch, "E2207", {"start": v(19.34, -16.03) * mm, "end": v(19.4, -16.03) * mm});
            skLineSegment(sketch, "E2208", {"start": v(26.88, -16.12) * mm, "end": v(26.94, -16.16) * mm});
            skLineSegment(sketch, "E2209", {"start": v(-47.02, -13.83) * mm, "end": v(-46.96, -13.87) * mm});
            skLineSegment(sketch, "E2210", {"start": v(16.04, -16.65) * mm, "end": v(16.05, -16.72) * mm});
            skLineSegment(sketch, "E2211", {"start": v(-46.24, -13.11) * mm, "end": v(-46.21, -13.17) * mm});
            skLineSegment(sketch, "E2212", {"start": v(29.17, -15.49) * mm, "end": v(29.23, -15.52) * mm});
            skLineSegment(sketch, "E2213", {"start": v(49.06, -16.28) * mm, "end": v(49.02, -16.34) * mm});
            skLineSegment(sketch, "E2214", {"start": v(31.34, -13.66) * mm, "end": v(31.3, -13.72) * mm});
            skLineSegment(sketch, "E2215", {"start": v(46.9, -17.07) * mm, "end": v(46.84, -17.1) * mm});
            skLineSegment(sketch, "E2216", {"start": v(19.02, -15.4) * mm, "end": v(19.07, -15.45) * mm});
            skLineSegment(sketch, "E2217", {"start": v(6.67, -17.1) * mm, "end": v(6.6, -17.11) * mm});
            skLineSegment(sketch, "E2218", {"start": v(-15.58, -13.31) * mm, "end": v(-15.59, -13.38) * mm});
            skLineSegment(sketch, "E2219", {"start": v(21.01, -14.48) * mm, "end": v(21.07, -14.5) * mm});
            skLineSegment(sketch, "E2220", {"start": v(50, -13.45) * mm, "end": v(50, -13.53) * mm});
            skLineSegment(sketch, "E2221", {"start": v(11.3, -15.1) * mm, "end": v(11.28, -15.17) * mm});
            skLineSegment(sketch, "E2222", {"start": v(19.87, -16.5) * mm, "end": v(19.87, -16.57) * mm});
            skLineSegment(sketch, "E2223", {"start": v(19.8, -14.72) * mm, "end": v(19.83, -14.78) * mm});
            skLineSegment(sketch, "E2224", {"start": v(48.97, -13.53) * mm, "end": v(49, -13.6) * mm});
            skLineSegment(sketch, "E2225", {"start": v(9.77, -13.66) * mm, "end": v(9.76, -13.7) * mm});
            skLineSegment(sketch, "E2226", {"start": v(-3.56, -16.03) * mm, "end": v(-3.63, -16.04) * mm});
            skLineSegment(sketch, "E2227", {"start": v(18.89, -13.66) * mm, "end": v(18.92, -13.72) * mm});
            skLineSegment(sketch, "E2228", {"start": v(-3.56, -16.03) * mm, "end": v(-3.49, -16.03) * mm});
            skLineSegment(sketch, "E2229", {"start": v(-16.7, -14.48) * mm, "end": v(-16.76, -14.5) * mm});
            skLineSegment(sketch, "E2230", {"start": v(16.73, -16.06) * mm, "end": v(16.79, -16.08) * mm});
            skLineSegment(sketch, "E2231", {"start": v(-26.74, -14.48) * mm, "end": v(-26.8, -14.5) * mm});
            skLineSegment(sketch, "E2232", {"start": v(8.97, -16.99) * mm, "end": v(9.03, -17.03) * mm});
            skLineSegment(sketch, "E2233", {"start": v(46.45, -17.07) * mm, "end": v(46.5, -17.1) * mm});
            skLineSegment(sketch, "E2234", {"start": v(-29.06, -17) * mm, "end": v(-29.11, -17.03) * mm});
            skLineSegment(sketch, "E2235", {"start": v(26.26, -16.17) * mm, "end": v(26.2, -16.22) * mm});
            skLineSegment(sketch, "E2236", {"start": v(30.4, -13.66) * mm, "end": v(30.44, -13.72) * mm});
            skLineSegment(sketch, "E2237", {"start": v(29.56, -15.52) * mm, "end": v(29.5, -15.53) * mm});
            skLineSegment(sketch, "E2238", {"start": v(39.01, -13.12) * mm, "end": v(38.98, -13.18) * mm});
            skLineSegment(sketch, "E2239", {"start": v(9.76, -16.3) * mm, "end": v(9.79, -16.36) * mm});
            skLineSegment(sketch, "E2240", {"start": v(-19.02, -17) * mm, "end": v(-19.07, -17.03) * mm});
            skLineSegment(sketch, "E2241", {"start": v(0.25, -13.28) * mm, "end": v(0.23, -13.35) * mm});
            skLineSegment(sketch, "E2242", {"start": v(7, -16.46) * mm, "end": v(7.02, -16.53) * mm});
            skLineSegment(sketch, "E2243", {"start": v(-17.02, -15.24) * mm, "end": v(-16.98, -15.3) * mm});
            skLineSegment(sketch, "E2244", {"start": v(-0.88, -12.9) * mm, "end": v(-0.95, -12.93) * mm});
            skLineSegment(sketch, "E2245", {"start": v(-3.03, -16.46) * mm, "end": v(-3.03, -16.53) * mm});
            skLineSegment(sketch, "E2246", {"start": v(10.97, -14.48) * mm, "end": v(11.03, -14.5) * mm});
            skLineSegment(sketch, "E2247", {"start": v(29.58, -16.05) * mm, "end": v(29.64, -16.08) * mm});
            skLineSegment(sketch, "E2248", {"start": v(8.84, -13.66) * mm, "end": v(8.88, -13.72) * mm});
            skLineSegment(sketch, "E2249", {"start": v(49.95, -15.24) * mm, "end": v(49.91, -15.3) * mm});
            skLineSegment(sketch, "E2250", {"start": v(36.62, -16.03) * mm, "end": v(36.55, -16.04) * mm});
            skLineSegment(sketch, "E2251", {"start": v(36.62, -16.03) * mm, "end": v(36.69, -16.03) * mm});
            skLineSegment(sketch, "E2252", {"start": v(-26.1, -14.81) * mm, "end": v(-26.09, -14.88) * mm});
            skLineSegment(sketch, "E2253", {"start": v(-15.24, -13.94) * mm, "end": v(-15.2, -13.95) * mm});
            skLineSegment(sketch, "E2254", {"start": v(-0.4, -16.99) * mm, "end": v(-0.45, -17.03) * mm});
            skLineSegment(sketch, "E2255", {"start": v(39.1, -13.83) * mm, "end": v(39.16, -13.87) * mm});
            skLineSegment(sketch, "E2256", {"start": v(26.13, -16.82) * mm, "end": v(26.16, -16.88) * mm});
            skLineSegment(sketch, "E2257", {"start": v(-47.19, -16.47) * mm, "end": v(-47.2, -16.54) * mm});
            skLineSegment(sketch, "E2258", {"start": v(-26.35, -16.08) * mm, "end": v(-26.3, -16.11) * mm});
            skLineSegment(sketch, "E2259", {"start": v(-49.64, -16.06) * mm, "end": v(-49.7, -16.09) * mm});
            skLineSegment(sketch, "E2260", {"start": v(29.9, -14.88) * mm, "end": v(29.91, -14.96) * mm});
            skLineSegment(sketch, "E2261", {"start": v(46.84, -17.1) * mm, "end": v(46.78, -17.11) * mm});
            skLineSegment(sketch, "E2262", {"start": v(-39.1, -17) * mm, "end": v(-39.16, -17.03) * mm});
            skLineSegment(sketch, "E2263", {"start": v(30.53, -15.4) * mm, "end": v(30.59, -15.45) * mm});
            skLineSegment(sketch, "E2264", {"start": v(-49.25, -16.08) * mm, "end": v(-49.2, -16.12) * mm});
            skLineSegment(sketch, "E2265", {"start": v(39.88, -13.11) * mm, "end": v(39.9, -13.17) * mm});
            skLineSegment(sketch, "E2266", {"start": v(49.66, -12.9) * mm, "end": v(49.72, -12.93) * mm});
            skLineSegment(sketch, "E2267", {"start": v(-16.06, -15.17) * mm, "end": v(-16.08, -15.24) * mm});
            skLineSegment(sketch, "E2268", {"start": v(31.3, -14.69) * mm, "end": v(31.34, -14.75) * mm});
            skLineSegment(sketch, "E2269", {"start": v(37.14, -16.46) * mm, "end": v(37.15, -16.53) * mm});
            skLineSegment(sketch, "E2270", {"start": v(-46.19, -16.39) * mm, "end": v(-46.17, -16.46) * mm});
            skLineSegment(sketch, "E2271", {"start": v(-25.62, -13.31) * mm, "end": v(-25.63, -13.38) * mm});
            skLineSegment(sketch, "E2272", {"start": v(49.15, -16.99) * mm, "end": v(49.2, -17.03) * mm});
            skLineSegment(sketch, "E2273", {"start": v(-17.01, -16.34) * mm, "end": v(-17.04, -16.4) * mm});
            skLineSegment(sketch, "E2274", {"start": v(49.02, -15.24) * mm, "end": v(49.05, -15.3) * mm});
            skLineSegment(sketch, "E2275", {"start": v(-39.61, -17.1) * mm, "end": v(-39.55, -17.11) * mm});
            skLineSegment(sketch, "E2276", {"start": v(-0.28, -16.3) * mm, "end": v(-0.25, -16.36) * mm});
            skLineSegment(sketch, "E2277", {"start": v(-27.06, -14.76) * mm, "end": v(-27.08, -14.82) * mm});
            skLineSegment(sketch, "E2278", {"start": v(-46.32, -13.8) * mm, "end": v(-46.37, -13.86) * mm});
            skLineSegment(sketch, "E2279", {"start": v(47.18, -16.46) * mm, "end": v(47.2, -16.53) * mm});
            skLineSegment(sketch, "E2280", {"start": v(-26.74, -16.05) * mm, "end": v(-26.8, -16.08) * mm});
            skLineSegment(sketch, "E2281", {"start": v(49.94, -16.3) * mm, "end": v(49.96, -16.36) * mm});
            skLineSegment(sketch, "E2282", {"start": v(-17.03, -15.2) * mm, "end": v(-17.02, -15.24) * mm});
            skLineSegment(sketch, "E2283", {"start": v(-0.54, -13.92) * mm, "end": v(-0.57, -13.94) * mm});
            skLineSegment(sketch, "E2284", {"start": v(19.7, -15.41) * mm, "end": v(19.64, -15.45) * mm});
            skLineSegment(sketch, "E2285", {"start": v(-19.5, -16.06) * mm, "end": v(-19.57, -16.09) * mm});
            skLineSegment(sketch, "E2286", {"start": v(19.07, -15.45) * mm, "end": v(19.13, -15.49) * mm});
            skLineSegment(sketch, "E2287", {"start": v(20.68, -14.48) * mm, "end": v(20.62, -14.5) * mm});
            skLineSegment(sketch, "E2288", {"start": v(-45.34, -13.95) * mm, "end": v(-45.28, -13.96) * mm});
            skLineSegment(sketch, "E2289", {"start": v(-0.26, -15.2) * mm, "end": v(-0.27, -15.24) * mm});
            skLineSegment(sketch, "E2290", {"start": v(18.84, -16.47) * mm, "end": v(18.83, -16.54) * mm});
            skLineSegment(sketch, "E2291", {"start": v(-16.08, -16.32) * mm, "end": v(-16.06, -16.39) * mm});
            skLineSegment(sketch, "E2292", {"start": v(-25.58, -13.66) * mm, "end": v(-25.55, -13.72) * mm});
            skLineSegment(sketch, "E2293", {"start": v(-26.41, -16.05) * mm, "end": v(-26.35, -16.08) * mm});
            skLineSegment(sketch, "E2294", {"start": v(-1.16, -16.28) * mm, "end": v(-1.2, -16.34) * mm});
            skLineSegment(sketch, "E2295", {"start": v(16.4, -16.06) * mm, "end": v(16.33, -16.09) * mm});
            skLineSegment(sketch, "E2296", {"start": v(9.65, -16.99) * mm, "end": v(9.6, -17.03) * mm});
            skLineSegment(sketch, "E2297", {"start": v(-47.15, -13.66) * mm, "end": v(-47.11, -13.72) * mm});
            skLineSegment(sketch, "E2298", {"start": v(20.95, -14.46) * mm, "end": v(21.01, -14.48) * mm});
            skLineSegment(sketch, "E2299", {"start": v(-0.96, -13.9) * mm, "end": v(-0.9, -13.94) * mm});
            skLineSegment(sketch, "E2300", {"start": v(-19.18, -16.06) * mm, "end": v(-19.12, -16.08) * mm});
            skLineSegment(sketch, "E2301", {"start": v(19.85, -16.72) * mm, "end": v(19.83, -16.78) * mm});
            skLineSegment(sketch, "E2302", {"start": v(-16.08, -15.24) * mm, "end": v(-16.12, -15.3) * mm});
            skLineSegment(sketch, "E2303", {"start": v(6, -16.44) * mm, "end": v(6, -16.5) * mm});
            skLineSegment(sketch, "E2304", {"start": v(-1.23, -15.17) * mm, "end": v(-1.2, -15.24) * mm});
            skLineSegment(sketch, "E2305", {"start": v(-4.05, -16.47) * mm, "end": v(-4.05, -16.54) * mm});
            skLineSegment(sketch, "E2306", {"start": v(-45.07, -13.95) * mm, "end": v(-45.14, -13.96) * mm});
            skLineSegment(sketch, "E2307", {"start": v(-0.25, -16.36) * mm, "end": v(-0.23, -16.42) * mm});
            skLineSegment(sketch, "E2308", {"start": v(10.64, -14.48) * mm, "end": v(10.57, -14.5) * mm});
            skLineSegment(sketch, "E2309", {"start": v(-17.04, -16.4) * mm, "end": v(-17.05, -16.43) * mm});
            skLineSegment(sketch, "E2310", {"start": v(29.25, -16.05) * mm, "end": v(29.18, -16.08) * mm});
            skLineSegment(sketch, "E2311", {"start": v(-27.08, -14.82) * mm, "end": v(-27.1, -14.85) * mm});
            skLineSegment(sketch, "E2312", {"start": v(-14.87, -13.92) * mm, "end": v(-14.94, -13.95) * mm});
            skLineSegment(sketch, "E2313", {"start": v(-46.17, -16.46) * mm, "end": v(-46.16, -16.53) * mm});
            skLineSegment(sketch, "E2314", {"start": v(16.98, -16.27) * mm, "end": v(17.01, -16.33) * mm});
            skLineSegment(sketch, "E2315", {"start": v(-26.8, -16.08) * mm, "end": v(-26.87, -16.12) * mm});
            skLineSegment(sketch, "E2316", {"start": v(39.8, -13.8) * mm, "end": v(39.75, -13.86) * mm});
            skLineSegment(sketch, "E2317", {"start": v(-46.23, -13.7) * mm, "end": v(-46.27, -13.75) * mm});
            skLineSegment(sketch, "E2318", {"start": v(-49.2, -16.12) * mm, "end": v(-49.14, -16.16) * mm});
            skLineSegment(sketch, "E2319", {"start": v(9.8, -16.72) * mm, "end": v(9.79, -16.78) * mm});
            skLineSegment(sketch, "E2320", {"start": v(-39.55, -17.11) * mm, "end": v(-39.48, -17.12) * mm});
            skLineSegment(sketch, "E2321", {"start": v(28.89, -14.89) * mm, "end": v(28.88, -14.96) * mm});
            skLineSegment(sketch, "E2322", {"start": v(-15.3, -13.9) * mm, "end": v(-15.24, -13.94) * mm});
            skLineSegment(sketch, "E2323", {"start": v(-16.06, -16.39) * mm, "end": v(-16.04, -16.46) * mm});
            skLineSegment(sketch, "E2324", {"start": v(-0.57, -13.94) * mm, "end": v(-0.63, -13.95) * mm});
            skLineSegment(sketch, "E2325", {"start": v(31.21, -15.41) * mm, "end": v(31.16, -15.45) * mm});
            skLineSegment(sketch, "E2326", {"start": v(19.64, -15.45) * mm, "end": v(19.58, -15.49) * mm});
            skLineSegment(sketch, "E2327", {"start": v(-19.57, -16.09) * mm, "end": v(-19.63, -16.12) * mm});
            skLineSegment(sketch, "E2328", {"start": v(-45.28, -13.96) * mm, "end": v(-45.2, -13.96) * mm});
            skLineSegment(sketch, "E2329", {"start": v(6.94, -16.27) * mm, "end": v(6.97, -16.33) * mm});
            skLineSegment(sketch, "E2330", {"start": v(-0.27, -15.24) * mm, "end": v(-0.3, -15.3) * mm});
            skLineSegment(sketch, "E2331", {"start": v(9.09, -13.9) * mm, "end": v(9.15, -13.94) * mm});
            skLineSegment(sketch, "E2332", {"start": v(49.33, -12.9) * mm, "end": v(49.27, -12.93) * mm});
            skLineSegment(sketch, "E2333", {"start": v(20.74, -14.46) * mm, "end": v(20.68, -14.48) * mm});
            skLineSegment(sketch, "E2334", {"start": v(-3.36, -16.06) * mm, "end": v(-3.3, -16.08) * mm});
            skLineSegment(sketch, "E2335", {"start": v(36.13, -16.47) * mm, "end": v(36.12, -16.54) * mm});
            skLineSegment(sketch, "E2336", {"start": v(18.84, -16.68) * mm, "end": v(18.86, -16.75) * mm});
            skLineSegment(sketch, "E2337", {"start": v(-26.13, -14.75) * mm, "end": v(-26.1, -14.81) * mm});
            skLineSegment(sketch, "E2338", {"start": v(-0.9, -13.94) * mm, "end": v(-0.83, -13.95) * mm});
            skLineSegment(sketch, "E2339", {"start": v(29.9, -16.68) * mm, "end": v(29.89, -16.75) * mm});
            skLineSegment(sketch, "E2340", {"start": v(49.82, -16.99) * mm, "end": v(49.77, -17.03) * mm});
            skLineSegment(sketch, "E2341", {"start": v(-26.3, -16.11) * mm, "end": v(-26.25, -16.16) * mm});
            skLineSegment(sketch, "E2342", {"start": v(-19.24, -16.04) * mm, "end": v(-19.18, -16.06) * mm});
            skLineSegment(sketch, "E2343", {"start": v(27.02, -16.27) * mm, "end": v(27.06, -16.33) * mm});
            skLineSegment(sketch, "E2344", {"start": v(-47.11, -13.72) * mm, "end": v(-47.07, -13.77) * mm});
            skLineSegment(sketch, "E2345", {"start": v(-47.17, -16.4) * mm, "end": v(-47.19, -16.47) * mm});
            skLineSegment(sketch, "E2346", {"start": v(-49.7, -16.09) * mm, "end": v(-49.76, -16.12) * mm});
            skLineSegment(sketch, "E2347", {"start": v(-1.24, -15.1) * mm, "end": v(-1.23, -15.17) * mm});
            skLineSegment(sketch, "E2348", {"start": v(29.11, -15.45) * mm, "end": v(29.17, -15.49) * mm});
            skLineSegment(sketch, "E2349", {"start": v(46.18, -16.44) * mm, "end": v(46.17, -16.5) * mm});
            skLineSegment(sketch, "E2350", {"start": v(8.8, -16.68) * mm, "end": v(8.82, -16.75) * mm});
            skLineSegment(sketch, "E2351", {"start": v(-39.28, -17.1) * mm, "end": v(-39.34, -17.11) * mm});
            skLineSegment(sketch, "E2352", {"start": v(19.13, -15.49) * mm, "end": v(19.19, -15.52) * mm});
            skSolve(sketch);
        }
        {
            var Q0;
            Q0 = qSketchRegion(id + "F4", true);
            extrude(context, id + "F5", {"entities" : qUnion([Q0]), "operationType" : NewBodyOperationType.ADD, "depth" : 1 * mm});
        }
    });
